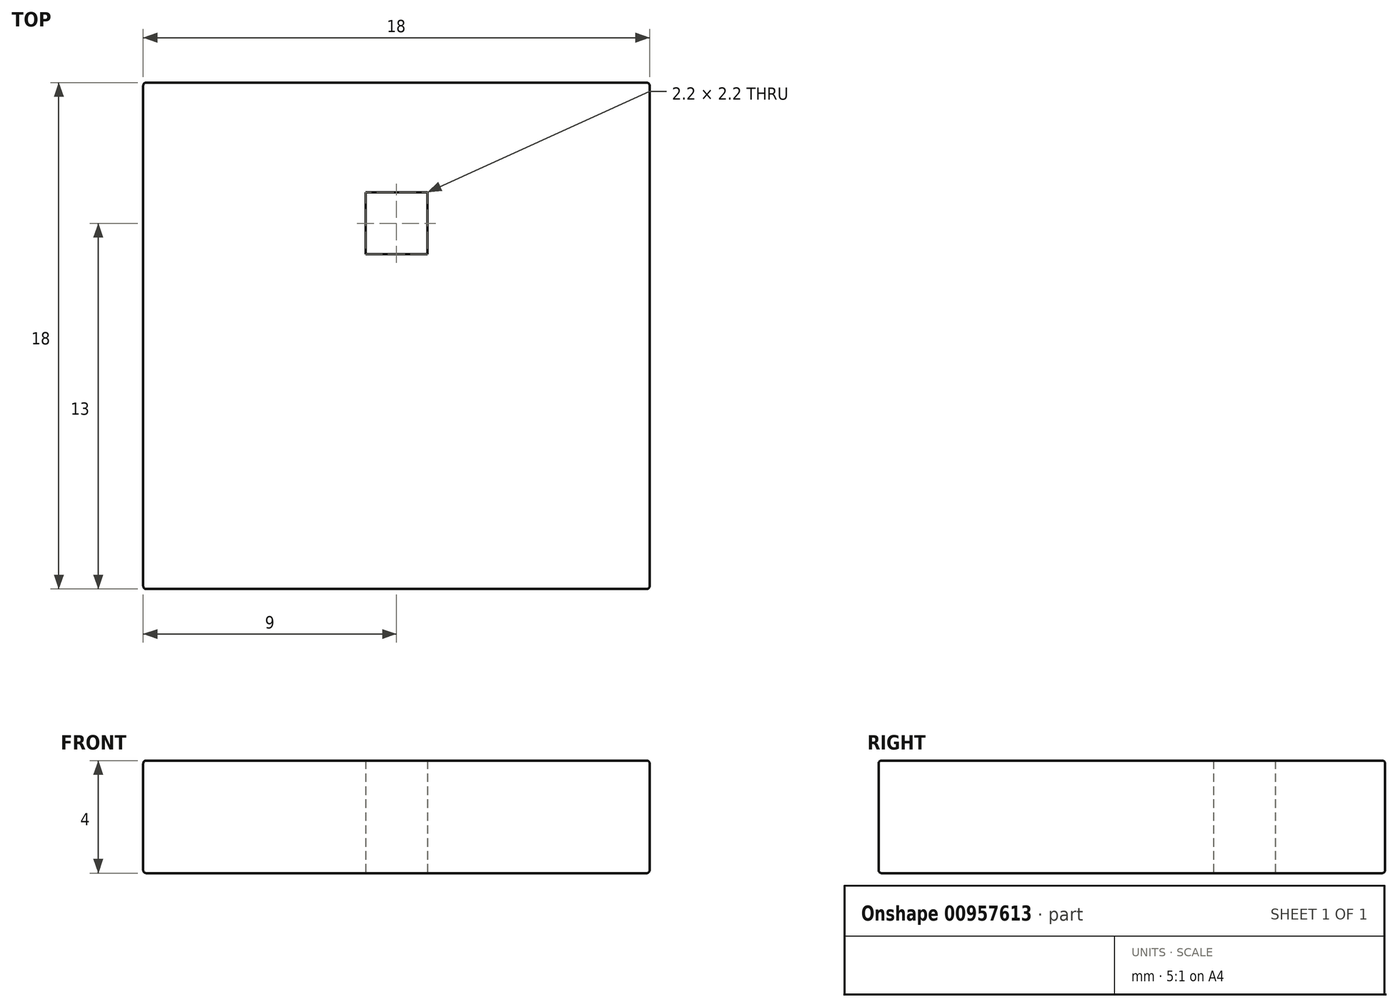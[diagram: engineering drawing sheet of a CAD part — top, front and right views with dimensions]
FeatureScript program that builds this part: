
annotation { "Feature Type Name" : "Feature", "Feature Type Description" : "" }
export const myFeature = defineFeature(function(context is Context, id is Id, definition is map)
    precondition{}
    {
        {
            var Q0;
            Q0=qCreatedBy(makeId("Top.planeOp"),FACE);
            var sketch = newSketch(context, id + "F0", { "sketchPlane" : qUnion([Q0])});
            skLineSegment(sketch, "E0.bottom", {"start": v(-9, 9) * mm, "end": v(9, 9) * mm});
            skLineSegment(sketch, "E0.top", {"start": v(-9, -9) * mm, "end": v(9, -9) * mm});
            skLineSegment(sketch, "E0.left", {"start": v(-9, 9) * mm, "end": v(-9, -9) * mm});
            skLineSegment(sketch, "E0.right", {"start": v(9, 9) * mm, "end": v(9, -9) * mm});
            skPoint(sketch, "E0.middle", {"position": v(0, 0) * mm});
            skLineSegment(sketch, "E1", {"start": v(-8, 9) * mm, "end": v(-8, -9) * mm});
            skLineSegment(sketch, "E2", {"start": v(-7.1, 9) * mm, "end": v(-7.1, -9) * mm});
            skLineSegment(sketch, "E3", {"start": v(-6.9, 9) * mm, "end": v(-6.9, -9) * mm});
            skLineSegment(sketch, "E4", {"start": v(-5.1, 9) * mm, "end": v(-5.1, -9) * mm});
            skLineSegment(sketch, "E5", {"start": v(-4.9, 9) * mm, "end": v(-4.9, -9) * mm});
            skLineSegment(sketch, "E6", {"start": v(-3.1, 9) * mm, "end": v(-3.1, -9) * mm});
            skLineSegment(sketch, "E7", {"start": v(-2.9, 9) * mm, "end": v(-2.9, -9) * mm});
            skLineSegment(sketch, "E8", {"start": v(-1.1, 9) * mm, "end": v(-1.1, -9) * mm});
            skLineSegment(sketch, "E9", {"start": v(-0.9, 9) * mm, "end": v(-0.9, -9) * mm});
            skLineSegment(sketch, "E10", {"start": v(0.9, 9) * mm, "end": v(0.9, -9) * mm});
            skLineSegment(sketch, "E11", {"start": v(1.1, 9) * mm, "end": v(1.1, -9) * mm});
            skLineSegment(sketch, "E12", {"start": v(2.9, 9) * mm, "end": v(2.9, -9) * mm});
            skLineSegment(sketch, "E13", {"start": v(3.1, 9) * mm, "end": v(3.1, -9) * mm});
            skLineSegment(sketch, "E14", {"start": v(4.9, 9) * mm, "end": v(4.9, -9) * mm});
            skLineSegment(sketch, "E15", {"start": v(5.1, 9) * mm, "end": v(5.1, -9) * mm});
            skLineSegment(sketch, "E16", {"start": v(6.9, 9) * mm, "end": v(6.9, -9) * mm});
            skLineSegment(sketch, "E17", {"start": v(7.1, 9) * mm, "end": v(7.1, -9) * mm});
            skLineSegment(sketch, "E18", {"start": v(8, 9) * mm, "end": v(8, -9) * mm});
            skLineSegment(sketch, "E19", {"start": v(9, 8) * mm, "end": v(-9, 8) * mm});
            skLineSegment(sketch, "E20", {"start": v(9, 7.1) * mm, "end": v(-9, 7.1) * mm});
            skLineSegment(sketch, "E21", {"start": v(9, 6.9) * mm, "end": v(-9, 6.9) * mm});
            skLineSegment(sketch, "E22", {"start": v(9, 5.1) * mm, "end": v(-9, 5.1) * mm});
            skLineSegment(sketch, "E23", {"start": v(9, 4.9) * mm, "end": v(-9, 4.9) * mm});
            skLineSegment(sketch, "E24", {"start": v(9, 3.1) * mm, "end": v(-9, 3.1) * mm});
            skLineSegment(sketch, "E25", {"start": v(9, 2.9) * mm, "end": v(-9, 2.9) * mm});
            skLineSegment(sketch, "E26", {"start": v(9, 1.1) * mm, "end": v(-9, 1.1) * mm});
            skLineSegment(sketch, "E27", {"start": v(9, 0.9) * mm, "end": v(-9, 0.9) * mm});
            skLineSegment(sketch, "E28", {"start": v(9, -0.9) * mm, "end": v(-9, -0.9) * mm});
            skLineSegment(sketch, "E29", {"start": v(9, -1.1) * mm, "end": v(-9, -1.1) * mm});
            skLineSegment(sketch, "E30", {"start": v(9, -2.9) * mm, "end": v(-9, -2.9) * mm});
            skLineSegment(sketch, "E31", {"start": v(9, -3.1) * mm, "end": v(-9, -3.1) * mm});
            skLineSegment(sketch, "E32", {"start": v(9, -4.9) * mm, "end": v(-9, -4.9) * mm});
            skLineSegment(sketch, "E33", {"start": v(9, -5.1) * mm, "end": v(-9, -5.1) * mm});
            skLineSegment(sketch, "E34", {"start": v(9, -6.9) * mm, "end": v(-9, -6.9) * mm});
            skLineSegment(sketch, "E35", {"start": v(9, -7.1) * mm, "end": v(-9, -7.1) * mm});
            skLineSegment(sketch, "E36", {"start": v(9, -8) * mm, "end": v(-9, -8) * mm});
            skSolve(sketch);
        }
        {
            var Q0;
            {var subQ0=sQuery(id+"F0.wireOp",EDGE,"E30");var subQ1=sQuery(id+"F0.wireOp",EDGE,"E10");var subQ2=makeQuery(id+"F0.imprint","INTERSECT",VERTEX,{"derivedFrom":[subQ1,subQ0]});Q0=makeQuery(id+"F0.imprint","IMPRINT",FACE,{"disambiguationData":[TD([[makeQuery(id+"F0.imprint","IMPRINT",EDGE,{"disambiguationData":[TD([[subQ2,-1.0]])],"derivedFrom":subQ1}),1.0]])]});}
            var Q1;
            {var subQ0=sQuery(id+"F0.wireOp",EDGE,"E26");var subQ1=sQuery(id+"F0.wireOp",EDGE,"E11");var subQ2=makeQuery(id+"F0.imprint","INTERSECT",VERTEX,{"derivedFrom":[subQ1,subQ0]});Q1=makeQuery(id+"F0.imprint","IMPRINT",FACE,{"disambiguationData":[TD([[makeQuery(id+"F0.imprint","IMPRINT",EDGE,{"disambiguationData":[TD([[subQ2,-1.0]])],"derivedFrom":subQ1}),1.0]])]});}
            var Q2;
            {var subQ0=sQuery(id+"F0.wireOp",EDGE,"E25");var subQ1=sQuery(id+"F0.wireOp",EDGE,"E8");var subQ2=makeQuery(id+"F0.imprint","INTERSECT",VERTEX,{"derivedFrom":[subQ1,subQ0]});Q2=makeQuery(id+"F0.imprint","IMPRINT",FACE,{"disambiguationData":[TD([[makeQuery(id+"F0.imprint","IMPRINT",EDGE,{"disambiguationData":[TD([[subQ2,-1.0]])],"derivedFrom":subQ1}),1.0]])]});}
            var Q3;
            {var subQ0=sQuery(id+"F0.wireOp",EDGE,"E30");var subQ1=sQuery(id+"F0.wireOp",EDGE,"E15");var subQ2=makeQuery(id+"F0.imprint","INTERSECT",VERTEX,{"derivedFrom":[subQ1,subQ0]});Q3=makeQuery(id+"F0.imprint","IMPRINT",FACE,{"disambiguationData":[TD([[makeQuery(id+"F0.imprint","IMPRINT",EDGE,{"disambiguationData":[TD([[subQ2,-1.0]])],"derivedFrom":subQ1}),1.0]])]});}
            var Q4;
            {var subQ0=sQuery(id+"F0.wireOp",EDGE,"E35");var subQ1=sQuery(id+"F0.wireOp",EDGE,"E12");var subQ2=makeQuery(id+"F0.imprint","INTERSECT",VERTEX,{"derivedFrom":[subQ1,subQ0]});Q4=makeQuery(id+"F0.imprint","IMPRINT",FACE,{"disambiguationData":[TD([[makeQuery(id+"F0.imprint","IMPRINT",EDGE,{"disambiguationData":[TD([[subQ2,-1.0]])],"derivedFrom":subQ1}),1.0]])]});}
            var Q5;
            {var subQ0=sQuery(id+"F0.wireOp",EDGE,"E35");var subQ1=sQuery(id+"F0.wireOp",EDGE,"E14");var subQ2=makeQuery(id+"F0.imprint","INTERSECT",VERTEX,{"derivedFrom":[subQ1,subQ0]});Q5=makeQuery(id+"F0.imprint","IMPRINT",FACE,{"disambiguationData":[TD([[makeQuery(id+"F0.imprint","IMPRINT",EDGE,{"disambiguationData":[TD([[subQ2,-1.0]])],"derivedFrom":subQ1}),1.0]])]});}
            var Q6;
            {var subQ0=sQuery(id+"F0.wireOp",EDGE,"E32");var subQ1=sQuery(id+"F0.wireOp",EDGE,"E10");var subQ2=makeQuery(id+"F0.imprint","INTERSECT",VERTEX,{"derivedFrom":[subQ1,subQ0]});Q6=makeQuery(id+"F0.imprint","IMPRINT",FACE,{"disambiguationData":[TD([[makeQuery(id+"F0.imprint","IMPRINT",EDGE,{"disambiguationData":[TD([[subQ2,-1.0]])],"derivedFrom":subQ1}),1.0]])]});}
            var Q7;
            {var subQ0=sQuery(id+"F0.wireOp",EDGE,"E23");var subQ1=sQuery(id+"F0.wireOp",EDGE,"E14");var subQ2=makeQuery(id+"F0.imprint","INTERSECT",VERTEX,{"derivedFrom":[subQ1,subQ0]});Q7=makeQuery(id+"F0.imprint","IMPRINT",FACE,{"disambiguationData":[TD([[makeQuery(id+"F0.imprint","IMPRINT",EDGE,{"disambiguationData":[TD([[subQ2,-1.0]])],"derivedFrom":subQ1}),1.0]])]});}
            var Q8;
            {var subQ0=sQuery(id+"F0.wireOp",EDGE,"E23");var subQ1=sQuery(id+"F0.wireOp",EDGE,"E16");var subQ2=makeQuery(id+"F0.imprint","INTERSECT",VERTEX,{"derivedFrom":[subQ1,subQ0]});Q8=makeQuery(id+"F0.imprint","IMPRINT",FACE,{"disambiguationData":[TD([[makeQuery(id+"F0.imprint","IMPRINT",EDGE,{"disambiguationData":[TD([[subQ2,-1.0]])],"derivedFrom":subQ1}),1.0]])]});}
            var Q9;
            {var subQ0=sQuery(id+"F0.wireOp",EDGE,"E27");var subQ1=sQuery(id+"F0.wireOp",EDGE,"E10");var subQ2=makeQuery(id+"F0.imprint","INTERSECT",VERTEX,{"derivedFrom":[subQ1,subQ0]});Q9=makeQuery(id+"F0.imprint","IMPRINT",FACE,{"disambiguationData":[TD([[makeQuery(id+"F0.imprint","IMPRINT",EDGE,{"disambiguationData":[TD([[subQ2,-1.0]])],"derivedFrom":subQ1}),1.0]])]});}
            var Q10;
            {var subQ0=sQuery(id+"F0.wireOp",EDGE,"E31");var subQ1=sQuery(id+"F0.wireOp",EDGE,"E2");var subQ2=makeQuery(id+"F0.imprint","INTERSECT",VERTEX,{"derivedFrom":[subQ1,subQ0]});Q10=makeQuery(id+"F0.imprint","IMPRINT",FACE,{"disambiguationData":[TD([[makeQuery(id+"F0.imprint","IMPRINT",EDGE,{"disambiguationData":[TD([[subQ2,-1.0]])],"derivedFrom":subQ1}),1.0]])]});}
            var Q11;
            {var subQ0=sQuery(id+"F0.wireOp",EDGE,"E30");var subQ1=sQuery(id+"F0.wireOp",EDGE,"E13");var subQ2=makeQuery(id+"F0.imprint","INTERSECT",VERTEX,{"derivedFrom":[subQ1,subQ0]});Q11=makeQuery(id+"F0.imprint","IMPRINT",FACE,{"disambiguationData":[TD([[makeQuery(id+"F0.imprint","IMPRINT",EDGE,{"disambiguationData":[TD([[subQ2,-1.0]])],"derivedFrom":subQ1}),1.0]])]});}
            var Q12;
            {var subQ0=sQuery(id+"F0.wireOp",EDGE,"E33");var subQ1=sQuery(id+"F0.wireOp",EDGE,"E16");var subQ2=makeQuery(id+"F0.imprint","INTERSECT",VERTEX,{"derivedFrom":[subQ1,subQ0]});Q12=makeQuery(id+"F0.imprint","IMPRINT",FACE,{"disambiguationData":[TD([[makeQuery(id+"F0.imprint","IMPRINT",EDGE,{"disambiguationData":[TD([[subQ2,-1.0]])],"derivedFrom":subQ1}),1.0]])]});}
            var Q13;
            {var subQ0=sQuery(id+"F0.wireOp",EDGE,"E29");var subQ1=sQuery(id+"F0.wireOp",EDGE,"E8");var subQ2=makeQuery(id+"F0.imprint","INTERSECT",VERTEX,{"derivedFrom":[subQ1,subQ0]});Q13=makeQuery(id+"F0.imprint","IMPRINT",FACE,{"disambiguationData":[TD([[makeQuery(id+"F0.imprint","IMPRINT",EDGE,{"disambiguationData":[TD([[subQ2,-1.0]])],"derivedFrom":subQ1}),1.0]])]});}
            var Q14;
            {var subQ0=sQuery(id+"F0.wireOp",EDGE,"E26");var subQ1=sQuery(id+"F0.wireOp",EDGE,"E1");var subQ2=makeQuery(id+"F0.imprint","INTERSECT",VERTEX,{"derivedFrom":[subQ1,subQ0]});Q14=makeQuery(id+"F0.imprint","IMPRINT",FACE,{"disambiguationData":[TD([[makeQuery(id+"F0.imprint","IMPRINT",EDGE,{"disambiguationData":[TD([[subQ2,-1.0]])],"derivedFrom":subQ1}),1.0]])]});}
            var Q15;
            {var subQ0=sQuery(id+"F0.wireOp",EDGE,"E30");var subQ1=sQuery(id+"F0.wireOp",EDGE,"E12");var subQ2=makeQuery(id+"F0.imprint","INTERSECT",VERTEX,{"derivedFrom":[subQ1,subQ0]});Q15=makeQuery(id+"F0.imprint","IMPRINT",FACE,{"disambiguationData":[TD([[makeQuery(id+"F0.imprint","IMPRINT",EDGE,{"disambiguationData":[TD([[subQ2,-1.0]])],"derivedFrom":subQ1}),1.0]])]});}
            var Q16;
            {var subQ0=sQuery(id+"F0.wireOp",EDGE,"E29");var subQ1=sQuery(id+"F0.wireOp",EDGE,"E12");var subQ2=makeQuery(id+"F0.imprint","INTERSECT",VERTEX,{"derivedFrom":[subQ1,subQ0]});Q16=makeQuery(id+"F0.imprint","IMPRINT",FACE,{"disambiguationData":[TD([[makeQuery(id+"F0.imprint","IMPRINT",EDGE,{"disambiguationData":[TD([[subQ2,-1.0]])],"derivedFrom":subQ1}),1.0]])]});}
            var Q17;
            {var subQ0=sQuery(id+"F0.wireOp",EDGE,"E31");var subQ1=sQuery(id+"F0.wireOp",EDGE,"E6");var subQ2=makeQuery(id+"F0.imprint","INTERSECT",VERTEX,{"derivedFrom":[subQ1,subQ0]});Q17=makeQuery(id+"F0.imprint","IMPRINT",FACE,{"disambiguationData":[TD([[makeQuery(id+"F0.imprint","IMPRINT",EDGE,{"disambiguationData":[TD([[subQ2,-1.0]])],"derivedFrom":subQ1}),1.0]])]});}
            var Q18;
            {var subQ0=sQuery(id+"F0.wireOp",EDGE,"E29");var subQ1=sQuery(id+"F0.wireOp",EDGE,"E10");var subQ2=makeQuery(id+"F0.imprint","INTERSECT",VERTEX,{"derivedFrom":[subQ1,subQ0]});Q18=makeQuery(id+"F0.imprint","IMPRINT",FACE,{"disambiguationData":[TD([[makeQuery(id+"F0.imprint","IMPRINT",EDGE,{"disambiguationData":[TD([[subQ2,-1.0]])],"derivedFrom":subQ1}),1.0]])]});}
            var Q19;
            {var subQ0=sQuery(id+"F0.wireOp",EDGE,"E25");var subQ1=sQuery(id+"F0.wireOp",EDGE,"E16");var subQ2=makeQuery(id+"F0.imprint","INTERSECT",VERTEX,{"derivedFrom":[subQ1,subQ0]});Q19=makeQuery(id+"F0.imprint","IMPRINT",FACE,{"disambiguationData":[TD([[makeQuery(id+"F0.imprint","IMPRINT",EDGE,{"disambiguationData":[TD([[subQ2,-1.0]])],"derivedFrom":subQ1}),1.0]])]});}
            var Q20;
            {var subQ0=sQuery(id+"F0.wireOp",EDGE,"E35");var subQ1=sQuery(id+"F0.wireOp",EDGE,"E16");var subQ2=makeQuery(id+"F0.imprint","INTERSECT",VERTEX,{"derivedFrom":[subQ1,subQ0]});Q20=makeQuery(id+"F0.imprint","IMPRINT",FACE,{"disambiguationData":[TD([[makeQuery(id+"F0.imprint","IMPRINT",EDGE,{"disambiguationData":[TD([[subQ2,-1.0]])],"derivedFrom":subQ1}),1.0]])]});}
            var Q21;
            {var subQ0=sQuery(id+"F0.wireOp",EDGE,"E31");var subQ1=sQuery(id+"F0.wireOp",EDGE,"E12");var subQ2=makeQuery(id+"F0.imprint","INTERSECT",VERTEX,{"derivedFrom":[subQ1,subQ0]});Q21=makeQuery(id+"F0.imprint","IMPRINT",FACE,{"disambiguationData":[TD([[makeQuery(id+"F0.imprint","IMPRINT",EDGE,{"disambiguationData":[TD([[subQ2,-1.0]])],"derivedFrom":subQ1}),1.0]])]});}
            var Q22;
            {var subQ0=sQuery(id+"F0.wireOp",EDGE,"E24");var subQ1=sQuery(id+"F0.wireOp",EDGE,"E1");var subQ2=makeQuery(id+"F0.imprint","INTERSECT",VERTEX,{"derivedFrom":[subQ1,subQ0]});Q22=makeQuery(id+"F0.imprint","IMPRINT",FACE,{"disambiguationData":[TD([[makeQuery(id+"F0.imprint","IMPRINT",EDGE,{"disambiguationData":[TD([[subQ2,-1.0]])],"derivedFrom":subQ1}),1.0]])]});}
            var Q23;
            {var subQ0=sQuery(id+"F0.wireOp",EDGE,"E27");var subQ1=sQuery(id+"F0.wireOp",EDGE,"E16");var subQ2=makeQuery(id+"F0.imprint","INTERSECT",VERTEX,{"derivedFrom":[subQ1,subQ0]});Q23=makeQuery(id+"F0.imprint","IMPRINT",FACE,{"disambiguationData":[TD([[makeQuery(id+"F0.imprint","IMPRINT",EDGE,{"disambiguationData":[TD([[subQ2,-1.0]])],"derivedFrom":subQ1}),1.0]])]});}
            var Q24;
            {var subQ0=sQuery(id+"F0.wireOp",EDGE,"E26");var subQ1=sQuery(id+"F0.wireOp",EDGE,"E9");var subQ2=makeQuery(id+"F0.imprint","INTERSECT",VERTEX,{"derivedFrom":[subQ1,subQ0]});Q24=makeQuery(id+"F0.imprint","IMPRINT",FACE,{"disambiguationData":[TD([[makeQuery(id+"F0.imprint","IMPRINT",EDGE,{"disambiguationData":[TD([[subQ2,-1.0]])],"derivedFrom":subQ1}),1.0]])]});}
            var Q25;
            {var subQ0=sQuery(id+"F0.wireOp",EDGE,"E35");var subQ1=sQuery(id+"F0.wireOp",EDGE,"E2");var subQ2=makeQuery(id+"F0.imprint","INTERSECT",VERTEX,{"derivedFrom":[subQ1,subQ0]});Q25=makeQuery(id+"F0.imprint","IMPRINT",FACE,{"disambiguationData":[TD([[makeQuery(id+"F0.imprint","IMPRINT",EDGE,{"disambiguationData":[TD([[subQ2,-1.0]])],"derivedFrom":subQ1}),1.0]])]});}
            var Q26;
            {var subQ0=sQuery(id+"F0.wireOp",EDGE,"E22");var subQ1=sQuery(id+"F0.wireOp",EDGE,"E16");var subQ2=makeQuery(id+"F0.imprint","INTERSECT",VERTEX,{"derivedFrom":[subQ1,subQ0]});Q26=makeQuery(id+"F0.imprint","IMPRINT",FACE,{"disambiguationData":[TD([[makeQuery(id+"F0.imprint","IMPRINT",EDGE,{"disambiguationData":[TD([[subQ2,-1.0]])],"derivedFrom":subQ1}),1.0]])]});}
            var Q27;
            {var subQ0=sQuery(id+"F0.wireOp",EDGE,"E35");var subQ1=sQuery(id+"F0.wireOp",EDGE,"E8");var subQ2=makeQuery(id+"F0.imprint","INTERSECT",VERTEX,{"derivedFrom":[subQ1,subQ0]});Q27=makeQuery(id+"F0.imprint","IMPRINT",FACE,{"disambiguationData":[TD([[makeQuery(id+"F0.imprint","IMPRINT",EDGE,{"disambiguationData":[TD([[subQ2,-1.0]])],"derivedFrom":subQ1}),1.0]])]});}
            var Q28;
            {var subQ0=sQuery(id+"F0.wireOp",EDGE,"E24");var subQ1=sQuery(id+"F0.wireOp",EDGE,"E7");var subQ2=makeQuery(id+"F0.imprint","INTERSECT",VERTEX,{"derivedFrom":[subQ1,subQ0]});Q28=makeQuery(id+"F0.imprint","IMPRINT",FACE,{"disambiguationData":[TD([[makeQuery(id+"F0.imprint","IMPRINT",EDGE,{"disambiguationData":[TD([[subQ2,-1.0]])],"derivedFrom":subQ1}),1.0]])]});}
            var Q29;
            {var subQ0=sQuery(id+"F0.wireOp",EDGE,"E21");var subQ1=sQuery(id+"F0.wireOp",EDGE,"E16");var subQ2=makeQuery(id+"F0.imprint","INTERSECT",VERTEX,{"derivedFrom":[subQ1,subQ0]});Q29=makeQuery(id+"F0.imprint","IMPRINT",FACE,{"disambiguationData":[TD([[makeQuery(id+"F0.imprint","IMPRINT",EDGE,{"disambiguationData":[TD([[subQ2,-1.0]])],"derivedFrom":subQ1}),1.0]])]});}
            var Q30;
            {var subQ0=sQuery(id+"F0.wireOp",EDGE,"E32");var subQ1=sQuery(id+"F0.wireOp",EDGE,"E11");var subQ2=makeQuery(id+"F0.imprint","INTERSECT",VERTEX,{"derivedFrom":[subQ1,subQ0]});Q30=makeQuery(id+"F0.imprint","IMPRINT",FACE,{"disambiguationData":[TD([[makeQuery(id+"F0.imprint","IMPRINT",EDGE,{"disambiguationData":[TD([[subQ2,-1.0]])],"derivedFrom":subQ1}),1.0]])]});}
            var Q31;
            {var subQ0=sQuery(id+"F0.wireOp",EDGE,"E33");var subQ1=sQuery(id+"F0.wireOp",EDGE,"E8");var subQ2=makeQuery(id+"F0.imprint","INTERSECT",VERTEX,{"derivedFrom":[subQ1,subQ0]});Q31=makeQuery(id+"F0.imprint","IMPRINT",FACE,{"disambiguationData":[TD([[makeQuery(id+"F0.imprint","IMPRINT",EDGE,{"disambiguationData":[TD([[subQ2,-1.0]])],"derivedFrom":subQ1}),1.0]])]});}
            var Q32;
            {var subQ0=sQuery(id+"F0.wireOp",EDGE,"E30");var subQ1=sQuery(id+"F0.wireOp",EDGE,"E9");var subQ2=makeQuery(id+"F0.imprint","INTERSECT",VERTEX,{"derivedFrom":[subQ1,subQ0]});Q32=makeQuery(id+"F0.imprint","IMPRINT",FACE,{"disambiguationData":[TD([[makeQuery(id+"F0.imprint","IMPRINT",EDGE,{"disambiguationData":[TD([[subQ2,-1.0]])],"derivedFrom":subQ1}),1.0]])]});}
            var Q33;
            {var subQ0=sQuery(id+"F0.wireOp",EDGE,"E27");var subQ1=sQuery(id+"F0.wireOp",EDGE,"E2");var subQ2=makeQuery(id+"F0.imprint","INTERSECT",VERTEX,{"derivedFrom":[subQ1,subQ0]});Q33=makeQuery(id+"F0.imprint","IMPRINT",FACE,{"disambiguationData":[TD([[makeQuery(id+"F0.imprint","IMPRINT",EDGE,{"disambiguationData":[TD([[subQ2,-1.0]])],"derivedFrom":subQ1}),1.0]])]});}
            var Q34;
            {var subQ0=sQuery(id+"F0.wireOp",EDGE,"E30");var subQ1=sQuery(id+"F0.wireOp",EDGE,"E11");var subQ2=makeQuery(id+"F0.imprint","INTERSECT",VERTEX,{"derivedFrom":[subQ1,subQ0]});Q34=makeQuery(id+"F0.imprint","IMPRINT",FACE,{"disambiguationData":[TD([[makeQuery(id+"F0.imprint","IMPRINT",EDGE,{"disambiguationData":[TD([[subQ2,-1.0]])],"derivedFrom":subQ1}),1.0]])]});}
            var Q35;
            {var subQ0=sQuery(id+"F0.wireOp",EDGE,"E26");var subQ1=sQuery(id+"F0.wireOp",EDGE,"E5");var subQ2=makeQuery(id+"F0.imprint","INTERSECT",VERTEX,{"derivedFrom":[subQ1,subQ0]});Q35=makeQuery(id+"F0.imprint","IMPRINT",FACE,{"disambiguationData":[TD([[makeQuery(id+"F0.imprint","IMPRINT",EDGE,{"disambiguationData":[TD([[subQ2,-1.0]])],"derivedFrom":subQ1}),1.0]])]});}
            var Q36;
            {var subQ0=sQuery(id+"F0.wireOp",EDGE,"E31");var subQ1=sQuery(id+"F0.wireOp",EDGE,"E8");var subQ2=makeQuery(id+"F0.imprint","INTERSECT",VERTEX,{"derivedFrom":[subQ1,subQ0]});Q36=makeQuery(id+"F0.imprint","IMPRINT",FACE,{"disambiguationData":[TD([[makeQuery(id+"F0.imprint","IMPRINT",EDGE,{"disambiguationData":[TD([[subQ2,-1.0]])],"derivedFrom":subQ1}),1.0]])]});}
            var Q37;
            {var subQ0=sQuery(id+"F0.wireOp",EDGE,"E32");var subQ1=sQuery(id+"F0.wireOp",EDGE,"E7");var subQ2=makeQuery(id+"F0.imprint","INTERSECT",VERTEX,{"derivedFrom":[subQ1,subQ0]});Q37=makeQuery(id+"F0.imprint","IMPRINT",FACE,{"disambiguationData":[TD([[makeQuery(id+"F0.imprint","IMPRINT",EDGE,{"disambiguationData":[TD([[subQ2,-1.0]])],"derivedFrom":subQ1}),1.0]])]});}
            var Q38;
            {var subQ0=sQuery(id+"F0.wireOp",EDGE,"E24");var subQ1=sQuery(id+"F0.wireOp",EDGE,"E17");var subQ2=makeQuery(id+"F0.imprint","INTERSECT",VERTEX,{"derivedFrom":[subQ1,subQ0]});Q38=makeQuery(id+"F0.imprint","IMPRINT",FACE,{"disambiguationData":[TD([[makeQuery(id+"F0.imprint","IMPRINT",EDGE,{"disambiguationData":[TD([[subQ2,-1.0]])],"derivedFrom":subQ1}),1.0]])]});}
            var Q39;
            {var subQ0=sQuery(id+"F0.wireOp",EDGE,"E26");var subQ1=sQuery(id+"F0.wireOp",EDGE,"E14");var subQ2=makeQuery(id+"F0.imprint","INTERSECT",VERTEX,{"derivedFrom":[subQ1,subQ0]});Q39=makeQuery(id+"F0.imprint","IMPRINT",FACE,{"disambiguationData":[TD([[makeQuery(id+"F0.imprint","IMPRINT",EDGE,{"disambiguationData":[TD([[subQ2,-1.0]])],"derivedFrom":subQ1}),1.0]])]});}
            var Q40;
            {var subQ0=sQuery(id+"F0.wireOp",EDGE,"E31");var subQ1=sQuery(id+"F0.wireOp",EDGE,"E14");var subQ2=makeQuery(id+"F0.imprint","INTERSECT",VERTEX,{"derivedFrom":[subQ1,subQ0]});Q40=makeQuery(id+"F0.imprint","IMPRINT",FACE,{"disambiguationData":[TD([[makeQuery(id+"F0.imprint","IMPRINT",EDGE,{"disambiguationData":[TD([[subQ2,-1.0]])],"derivedFrom":subQ1}),1.0]])]});}
            var Q41;
            {var subQ0=sQuery(id+"F0.wireOp",EDGE,"E24");var subQ1=sQuery(id+"F0.wireOp",EDGE,"E5");var subQ2=makeQuery(id+"F0.imprint","INTERSECT",VERTEX,{"derivedFrom":[subQ1,subQ0]});Q41=makeQuery(id+"F0.imprint","IMPRINT",FACE,{"disambiguationData":[TD([[makeQuery(id+"F0.imprint","IMPRINT",EDGE,{"disambiguationData":[TD([[subQ2,-1.0]])],"derivedFrom":subQ1}),1.0]])]});}
            var Q42;
            {var subQ0=sQuery(id+"F0.wireOp",EDGE,"E26");var subQ1=sQuery(id+"F0.wireOp",EDGE,"E12");var subQ2=makeQuery(id+"F0.imprint","INTERSECT",VERTEX,{"derivedFrom":[subQ1,subQ0]});Q42=makeQuery(id+"F0.imprint","IMPRINT",FACE,{"disambiguationData":[TD([[makeQuery(id+"F0.imprint","IMPRINT",EDGE,{"disambiguationData":[TD([[subQ2,-1.0]])],"derivedFrom":subQ1}),1.0]])]});}
            var Q43;
            {var subQ0=sQuery(id+"F0.wireOp",EDGE,"E30");var subQ1=sQuery(id+"F0.wireOp",EDGE,"E5");var subQ2=makeQuery(id+"F0.imprint","INTERSECT",VERTEX,{"derivedFrom":[subQ1,subQ0]});Q43=makeQuery(id+"F0.imprint","IMPRINT",FACE,{"disambiguationData":[TD([[makeQuery(id+"F0.imprint","IMPRINT",EDGE,{"disambiguationData":[TD([[subQ2,-1.0]])],"derivedFrom":subQ1}),1.0]])]});}
            var Q44;
            {var subQ0=sQuery(id+"F0.wireOp",EDGE,"E33");var subQ1=sQuery(id+"F0.wireOp",EDGE,"E14");var subQ2=makeQuery(id+"F0.imprint","INTERSECT",VERTEX,{"derivedFrom":[subQ1,subQ0]});Q44=makeQuery(id+"F0.imprint","IMPRINT",FACE,{"disambiguationData":[TD([[makeQuery(id+"F0.imprint","IMPRINT",EDGE,{"disambiguationData":[TD([[subQ2,-1.0]])],"derivedFrom":subQ1}),1.0]])]});}
            var Q45;
            {var subQ0=sQuery(id+"F0.wireOp",EDGE,"E32");var subQ1=sQuery(id+"F0.wireOp",EDGE,"E9");var subQ2=makeQuery(id+"F0.imprint","INTERSECT",VERTEX,{"derivedFrom":[subQ1,subQ0]});Q45=makeQuery(id+"F0.imprint","IMPRINT",FACE,{"disambiguationData":[TD([[makeQuery(id+"F0.imprint","IMPRINT",EDGE,{"disambiguationData":[TD([[subQ2,-1.0]])],"derivedFrom":subQ1}),1.0]])]});}
            var Q46;
            {var subQ0=sQuery(id+"F0.wireOp",EDGE,"E25");var subQ1=sQuery(id+"F0.wireOp",EDGE,"E6");var subQ2=makeQuery(id+"F0.imprint","INTERSECT",VERTEX,{"derivedFrom":[subQ1,subQ0]});Q46=makeQuery(id+"F0.imprint","IMPRINT",FACE,{"disambiguationData":[TD([[makeQuery(id+"F0.imprint","IMPRINT",EDGE,{"disambiguationData":[TD([[subQ2,-1.0]])],"derivedFrom":subQ1}),1.0]])]});}
            var Q47;
            {var subQ0=sQuery(id+"F0.wireOp",EDGE,"E19");var subQ1=sQuery(id+"F0.wireOp",EDGE,"E16");var subQ2=makeQuery(id+"F0.imprint","INTERSECT",VERTEX,{"derivedFrom":[subQ1,subQ0]});Q47=makeQuery(id+"F0.imprint","IMPRINT",FACE,{"disambiguationData":[TD([[makeQuery(id+"F0.imprint","IMPRINT",EDGE,{"disambiguationData":[TD([[subQ2,-1.0]])],"derivedFrom":subQ1}),1.0]])]});}
            var Q48;
            {var subQ0=sQuery(id+"F0.wireOp",EDGE,"E19");var subQ1=sQuery(id+"F0.wireOp",EDGE,"E10");var subQ2=makeQuery(id+"F0.imprint","INTERSECT",VERTEX,{"derivedFrom":[subQ1,subQ0]});Q48=makeQuery(id+"F0.imprint","IMPRINT",FACE,{"disambiguationData":[TD([[makeQuery(id+"F0.imprint","IMPRINT",EDGE,{"disambiguationData":[TD([[subQ2,-1.0]])],"derivedFrom":subQ1}),1.0]])]});}
            var Q49;
            {var subQ0=sQuery(id+"F0.wireOp",EDGE,"E19");var subQ1=sQuery(id+"F0.wireOp",EDGE,"E2");var subQ2=makeQuery(id+"F0.imprint","INTERSECT",VERTEX,{"derivedFrom":[subQ1,subQ0]});Q49=makeQuery(id+"F0.imprint","IMPRINT",FACE,{"disambiguationData":[TD([[makeQuery(id+"F0.imprint","IMPRINT",EDGE,{"disambiguationData":[TD([[subQ2,-1.0]])],"derivedFrom":subQ1}),1.0]])]});}
            var Q50;
            {var subQ0=sQuery(id+"F0.wireOp",EDGE,"E32");var subQ1=sQuery(id+"F0.wireOp",EDGE,"E17");var subQ2=makeQuery(id+"F0.imprint","INTERSECT",VERTEX,{"derivedFrom":[subQ1,subQ0]});Q50=makeQuery(id+"F0.imprint","IMPRINT",FACE,{"disambiguationData":[TD([[makeQuery(id+"F0.imprint","IMPRINT",EDGE,{"disambiguationData":[TD([[subQ2,-1.0]])],"derivedFrom":subQ1}),1.0]])]});}
            var Q51;
            {var subQ0=sQuery(id+"F0.wireOp",EDGE,"E30");var subQ1=sQuery(id+"F0.wireOp",EDGE,"E17");var subQ2=makeQuery(id+"F0.imprint","INTERSECT",VERTEX,{"derivedFrom":[subQ1,subQ0]});Q51=makeQuery(id+"F0.imprint","IMPRINT",FACE,{"disambiguationData":[TD([[makeQuery(id+"F0.imprint","IMPRINT",EDGE,{"disambiguationData":[TD([[subQ2,-1.0]])],"derivedFrom":subQ1}),1.0]])]});}
            var Q52;
            {var subQ0=sQuery(id+"F0.wireOp",EDGE,"E33");var subQ1=sQuery(id+"F0.wireOp",EDGE,"E12");var subQ2=makeQuery(id+"F0.imprint","INTERSECT",VERTEX,{"derivedFrom":[subQ1,subQ0]});Q52=makeQuery(id+"F0.imprint","IMPRINT",FACE,{"disambiguationData":[TD([[makeQuery(id+"F0.imprint","IMPRINT",EDGE,{"disambiguationData":[TD([[subQ2,-1.0]])],"derivedFrom":subQ1}),1.0]])]});}
            var Q53;
            {var subQ0=sQuery(id+"F0.wireOp",EDGE,"E22");var subQ1=sQuery(id+"F0.wireOp",EDGE,"E13");var subQ2=makeQuery(id+"F0.imprint","INTERSECT",VERTEX,{"derivedFrom":[subQ1,subQ0]});Q53=makeQuery(id+"F0.imprint","IMPRINT",FACE,{"disambiguationData":[TD([[makeQuery(id+"F0.imprint","IMPRINT",EDGE,{"disambiguationData":[TD([[subQ2,-1.0]])],"derivedFrom":subQ1}),1.0]])]});}
            var Q54;
            {var subQ0=sQuery(id+"F0.wireOp",EDGE,"E19");var subQ1=sQuery(id+"F0.wireOp",EDGE,"E14");var subQ2=makeQuery(id+"F0.imprint","INTERSECT",VERTEX,{"derivedFrom":[subQ1,subQ0]});Q54=makeQuery(id+"F0.imprint","IMPRINT",FACE,{"disambiguationData":[TD([[makeQuery(id+"F0.imprint","IMPRINT",EDGE,{"disambiguationData":[TD([[subQ2,-1.0]])],"derivedFrom":subQ1}),1.0]])]});}
            var Q55;
            {var subQ0=sQuery(id+"F0.wireOp",EDGE,"E32");var subQ1=sQuery(id+"F0.wireOp",EDGE,"E16");var subQ2=makeQuery(id+"F0.imprint","INTERSECT",VERTEX,{"derivedFrom":[subQ1,subQ0]});Q55=makeQuery(id+"F0.imprint","IMPRINT",FACE,{"disambiguationData":[TD([[makeQuery(id+"F0.imprint","IMPRINT",EDGE,{"disambiguationData":[TD([[subQ2,-1.0]])],"derivedFrom":subQ1}),1.0]])]});}
            var Q56;
            {var subQ0=sQuery(id+"F0.wireOp",EDGE,"E32");var subQ1=sQuery(id+"F0.wireOp",EDGE,"E3");var subQ2=makeQuery(id+"F0.imprint","INTERSECT",VERTEX,{"derivedFrom":[subQ1,subQ0]});Q56=makeQuery(id+"F0.imprint","IMPRINT",FACE,{"disambiguationData":[TD([[makeQuery(id+"F0.imprint","IMPRINT",EDGE,{"disambiguationData":[TD([[subQ2,-1.0]])],"derivedFrom":subQ1}),1.0]])]});}
            var Q57;
            {var subQ0=sQuery(id+"F0.wireOp",EDGE,"E32");var subQ1=sQuery(id+"F0.wireOp",EDGE,"E6");var subQ2=makeQuery(id+"F0.imprint","INTERSECT",VERTEX,{"derivedFrom":[subQ1,subQ0]});Q57=makeQuery(id+"F0.imprint","IMPRINT",FACE,{"disambiguationData":[TD([[makeQuery(id+"F0.imprint","IMPRINT",EDGE,{"disambiguationData":[TD([[subQ2,-1.0]])],"derivedFrom":subQ1}),1.0]])]});}
            var Q58;
            {var subQ0=sQuery(id+"F0.wireOp",EDGE,"E35");var subQ1=sQuery(id+"F0.wireOp",EDGE,"E10");var subQ2=makeQuery(id+"F0.imprint","INTERSECT",VERTEX,{"derivedFrom":[subQ1,subQ0]});Q58=makeQuery(id+"F0.imprint","IMPRINT",FACE,{"disambiguationData":[TD([[makeQuery(id+"F0.imprint","IMPRINT",EDGE,{"disambiguationData":[TD([[subQ2,-1.0]])],"derivedFrom":subQ1}),1.0]])]});}
            var Q59;
            {var subQ0=sQuery(id+"F0.wireOp",EDGE,"E23");var subQ1=sQuery(id+"F0.wireOp",EDGE,"E12");var subQ2=makeQuery(id+"F0.imprint","INTERSECT",VERTEX,{"derivedFrom":[subQ1,subQ0]});Q59=makeQuery(id+"F0.imprint","IMPRINT",FACE,{"disambiguationData":[TD([[makeQuery(id+"F0.imprint","IMPRINT",EDGE,{"disambiguationData":[TD([[subQ2,-1.0]])],"derivedFrom":subQ1}),1.0]])]});}
            var Q60;
            {var subQ0=sQuery(id+"F0.wireOp",EDGE,"E32");var subQ1=sQuery(id+"F0.wireOp",EDGE,"E5");var subQ2=makeQuery(id+"F0.imprint","INTERSECT",VERTEX,{"derivedFrom":[subQ1,subQ0]});Q60=makeQuery(id+"F0.imprint","IMPRINT",FACE,{"disambiguationData":[TD([[makeQuery(id+"F0.imprint","IMPRINT",EDGE,{"disambiguationData":[TD([[subQ2,-1.0]])],"derivedFrom":subQ1}),1.0]])]});}
            var Q61;
            {var subQ0=sQuery(id+"F0.wireOp",EDGE,"E33");var subQ1=sQuery(id+"F0.wireOp",EDGE,"E6");var subQ2=makeQuery(id+"F0.imprint","INTERSECT",VERTEX,{"derivedFrom":[subQ1,subQ0]});Q61=makeQuery(id+"F0.imprint","IMPRINT",FACE,{"disambiguationData":[TD([[makeQuery(id+"F0.imprint","IMPRINT",EDGE,{"disambiguationData":[TD([[subQ2,-1.0]])],"derivedFrom":subQ1}),1.0]])]});}
            var Q62;
            {var subQ0=sQuery(id+"F0.wireOp",EDGE,"E30");var subQ1=sQuery(id+"F0.wireOp",EDGE,"E7");var subQ2=makeQuery(id+"F0.imprint","INTERSECT",VERTEX,{"derivedFrom":[subQ1,subQ0]});Q62=makeQuery(id+"F0.imprint","IMPRINT",FACE,{"disambiguationData":[TD([[makeQuery(id+"F0.imprint","IMPRINT",EDGE,{"disambiguationData":[TD([[subQ2,-1.0]])],"derivedFrom":subQ1}),1.0]])]});}
            var Q63;
            {var subQ0=sQuery(id+"F0.wireOp",EDGE,"E33");var subQ1=sQuery(id+"F0.wireOp",EDGE,"E10");var subQ2=makeQuery(id+"F0.imprint","INTERSECT",VERTEX,{"derivedFrom":[subQ1,subQ0]});Q63=makeQuery(id+"F0.imprint","IMPRINT",FACE,{"disambiguationData":[TD([[makeQuery(id+"F0.imprint","IMPRINT",EDGE,{"disambiguationData":[TD([[subQ2,-1.0]])],"derivedFrom":subQ1}),1.0]])]});}
            var Q64;
            {var subQ0=sQuery(id+"F0.wireOp",EDGE,"E30");var subQ1=sQuery(id+"F0.wireOp",EDGE,"E14");var subQ2=makeQuery(id+"F0.imprint","INTERSECT",VERTEX,{"derivedFrom":[subQ1,subQ0]});Q64=makeQuery(id+"F0.imprint","IMPRINT",FACE,{"disambiguationData":[TD([[makeQuery(id+"F0.imprint","IMPRINT",EDGE,{"disambiguationData":[TD([[subQ2,-1.0]])],"derivedFrom":subQ1}),1.0]])]});}
            var Q65;
            {var subQ0=sQuery(id+"F0.wireOp",EDGE,"E26");var subQ1=sQuery(id+"F0.wireOp",EDGE,"E13");var subQ2=makeQuery(id+"F0.imprint","INTERSECT",VERTEX,{"derivedFrom":[subQ1,subQ0]});Q65=makeQuery(id+"F0.imprint","IMPRINT",FACE,{"disambiguationData":[TD([[makeQuery(id+"F0.imprint","IMPRINT",EDGE,{"disambiguationData":[TD([[subQ2,-1.0]])],"derivedFrom":subQ1}),1.0]])]});}
            var Q66;
            {var subQ0=sQuery(id+"F0.wireOp",EDGE,"E26");var subQ1=sQuery(id+"F0.wireOp",EDGE,"E16");var subQ2=makeQuery(id+"F0.imprint","INTERSECT",VERTEX,{"derivedFrom":[subQ1,subQ0]});Q66=makeQuery(id+"F0.imprint","IMPRINT",FACE,{"disambiguationData":[TD([[makeQuery(id+"F0.imprint","IMPRINT",EDGE,{"disambiguationData":[TD([[subQ2,-1.0]])],"derivedFrom":subQ1}),1.0]])]});}
            var Q67;
            {var subQ0=sQuery(id+"F0.wireOp",EDGE,"E32");var subQ1=sQuery(id+"F0.wireOp",EDGE,"E14");var subQ2=makeQuery(id+"F0.imprint","INTERSECT",VERTEX,{"derivedFrom":[subQ1,subQ0]});Q67=makeQuery(id+"F0.imprint","IMPRINT",FACE,{"disambiguationData":[TD([[makeQuery(id+"F0.imprint","IMPRINT",EDGE,{"disambiguationData":[TD([[subQ2,-1.0]])],"derivedFrom":subQ1}),1.0]])]});}
            var Q68;
            {var subQ0=sQuery(id+"F0.wireOp",EDGE,"E24");var subQ1=sQuery(id+"F0.wireOp",EDGE,"E11");var subQ2=makeQuery(id+"F0.imprint","INTERSECT",VERTEX,{"derivedFrom":[subQ1,subQ0]});Q68=makeQuery(id+"F0.imprint","IMPRINT",FACE,{"disambiguationData":[TD([[makeQuery(id+"F0.imprint","IMPRINT",EDGE,{"disambiguationData":[TD([[subQ2,-1.0]])],"derivedFrom":subQ1}),1.0]])]});}
            var Q69;
            {var subQ0=sQuery(id+"F0.wireOp",EDGE,"E30");var subQ1=sQuery(id+"F0.wireOp",EDGE,"E3");var subQ2=makeQuery(id+"F0.imprint","INTERSECT",VERTEX,{"derivedFrom":[subQ1,subQ0]});Q69=makeQuery(id+"F0.imprint","IMPRINT",FACE,{"disambiguationData":[TD([[makeQuery(id+"F0.imprint","IMPRINT",EDGE,{"disambiguationData":[TD([[subQ2,-1.0]])],"derivedFrom":subQ1}),1.0]])]});}
            var Q70;
            {var subQ0=sQuery(id+"F0.wireOp",EDGE,"E22");var subQ1=sQuery(id+"F0.wireOp",EDGE,"E14");var subQ2=makeQuery(id+"F0.imprint","INTERSECT",VERTEX,{"derivedFrom":[subQ1,subQ0]});Q70=makeQuery(id+"F0.imprint","IMPRINT",FACE,{"disambiguationData":[TD([[makeQuery(id+"F0.imprint","IMPRINT",EDGE,{"disambiguationData":[TD([[subQ2,-1.0]])],"derivedFrom":subQ1}),1.0]])]});}
            var Q71;
            {var subQ0=sQuery(id+"F0.wireOp",EDGE,"E22");var subQ1=sQuery(id+"F0.wireOp",EDGE,"E15");var subQ2=makeQuery(id+"F0.imprint","INTERSECT",VERTEX,{"derivedFrom":[subQ1,subQ0]});Q71=makeQuery(id+"F0.imprint","IMPRINT",FACE,{"disambiguationData":[TD([[makeQuery(id+"F0.imprint","IMPRINT",EDGE,{"disambiguationData":[TD([[subQ2,-1.0]])],"derivedFrom":subQ1}),1.0]])]});}
            var Q72;
            {var subQ0=sQuery(id+"F0.wireOp",EDGE,"E29");var subQ1=sQuery(id+"F0.wireOp",EDGE,"E16");var subQ2=makeQuery(id+"F0.imprint","INTERSECT",VERTEX,{"derivedFrom":[subQ1,subQ0]});Q72=makeQuery(id+"F0.imprint","IMPRINT",FACE,{"disambiguationData":[TD([[makeQuery(id+"F0.imprint","IMPRINT",EDGE,{"disambiguationData":[TD([[subQ2,-1.0]])],"derivedFrom":subQ1}),1.0]])]});}
            var Q73;
            {var subQ0=sQuery(id+"F0.wireOp",EDGE,"E22");var subQ1=sQuery(id+"F0.wireOp",EDGE,"E17");var subQ2=makeQuery(id+"F0.imprint","INTERSECT",VERTEX,{"derivedFrom":[subQ1,subQ0]});Q73=makeQuery(id+"F0.imprint","IMPRINT",FACE,{"disambiguationData":[TD([[makeQuery(id+"F0.imprint","IMPRINT",EDGE,{"disambiguationData":[TD([[subQ2,-1.0]])],"derivedFrom":subQ1}),1.0]])]});}
            var Q74;
            {var subQ0=sQuery(id+"F0.wireOp",EDGE,"E30");var subQ1=sQuery(id+"F0.wireOp",EDGE,"E6");var subQ2=makeQuery(id+"F0.imprint","INTERSECT",VERTEX,{"derivedFrom":[subQ1,subQ0]});Q74=makeQuery(id+"F0.imprint","IMPRINT",FACE,{"disambiguationData":[TD([[makeQuery(id+"F0.imprint","IMPRINT",EDGE,{"disambiguationData":[TD([[subQ2,-1.0]])],"derivedFrom":subQ1}),1.0]])]});}
            var Q75;
            {var subQ0=sQuery(id+"F0.wireOp",EDGE,"E21");var subQ1=sQuery(id+"F0.wireOp",EDGE,"E10");var subQ2=makeQuery(id+"F0.imprint","INTERSECT",VERTEX,{"derivedFrom":[subQ1,subQ0]});Q75=makeQuery(id+"F0.imprint","IMPRINT",FACE,{"disambiguationData":[TD([[makeQuery(id+"F0.imprint","IMPRINT",EDGE,{"disambiguationData":[TD([[subQ2,-1.0]])],"derivedFrom":subQ1}),1.0]])]});}
            var Q76;
            {var subQ0=sQuery(id+"F0.wireOp",EDGE,"E24");var subQ1=sQuery(id+"F0.wireOp",EDGE,"E6");var subQ2=makeQuery(id+"F0.imprint","INTERSECT",VERTEX,{"derivedFrom":[subQ1,subQ0]});Q76=makeQuery(id+"F0.imprint","IMPRINT",FACE,{"disambiguationData":[TD([[makeQuery(id+"F0.imprint","IMPRINT",EDGE,{"disambiguationData":[TD([[subQ2,-1.0]])],"derivedFrom":subQ1}),1.0]])]});}
            var Q77;
            {var subQ0=sQuery(id+"F0.wireOp",EDGE,"E32");var subQ1=sQuery(id+"F0.wireOp",EDGE,"E1");var subQ2=makeQuery(id+"F0.imprint","INTERSECT",VERTEX,{"derivedFrom":[subQ1,subQ0]});Q77=makeQuery(id+"F0.imprint","IMPRINT",FACE,{"disambiguationData":[TD([[makeQuery(id+"F0.imprint","IMPRINT",EDGE,{"disambiguationData":[TD([[subQ2,-1.0]])],"derivedFrom":subQ1}),1.0]])]});}
            var Q78;
            {var subQ0=sQuery(id+"F0.wireOp",EDGE,"E24");var subQ1=sQuery(id+"F0.wireOp",EDGE,"E12");var subQ2=makeQuery(id+"F0.imprint","INTERSECT",VERTEX,{"derivedFrom":[subQ1,subQ0]});Q78=makeQuery(id+"F0.imprint","IMPRINT",FACE,{"disambiguationData":[TD([[makeQuery(id+"F0.imprint","IMPRINT",EDGE,{"disambiguationData":[TD([[subQ2,-1.0]])],"derivedFrom":subQ1}),1.0]])]});}
            var Q79;
            {var subQ0=sQuery(id+"F0.wireOp",EDGE,"E25");var subQ1=sQuery(id+"F0.wireOp",EDGE,"E14");var subQ2=makeQuery(id+"F0.imprint","INTERSECT",VERTEX,{"derivedFrom":[subQ1,subQ0]});Q79=makeQuery(id+"F0.imprint","IMPRINT",FACE,{"disambiguationData":[TD([[makeQuery(id+"F0.imprint","IMPRINT",EDGE,{"disambiguationData":[TD([[subQ2,-1.0]])],"derivedFrom":subQ1}),1.0]])]});}
            var Q80;
            {var subQ0=sQuery(id+"F0.wireOp",EDGE,"E26");var subQ1=sQuery(id+"F0.wireOp",EDGE,"E6");var subQ2=makeQuery(id+"F0.imprint","INTERSECT",VERTEX,{"derivedFrom":[subQ1,subQ0]});Q80=makeQuery(id+"F0.imprint","IMPRINT",FACE,{"disambiguationData":[TD([[makeQuery(id+"F0.imprint","IMPRINT",EDGE,{"disambiguationData":[TD([[subQ2,-1.0]])],"derivedFrom":subQ1}),1.0]])]});}
            var Q81;
            {var subQ0=sQuery(id+"F0.wireOp",EDGE,"E24");var subQ1=sQuery(id+"F0.wireOp",EDGE,"E13");var subQ2=makeQuery(id+"F0.imprint","INTERSECT",VERTEX,{"derivedFrom":[subQ1,subQ0]});Q81=makeQuery(id+"F0.imprint","IMPRINT",FACE,{"disambiguationData":[TD([[makeQuery(id+"F0.imprint","IMPRINT",EDGE,{"disambiguationData":[TD([[subQ2,-1.0]])],"derivedFrom":subQ1}),1.0]])]});}
            var Q82;
            {var subQ0=sQuery(id+"F0.wireOp",EDGE,"E31");var subQ1=sQuery(id+"F0.wireOp",EDGE,"E10");var subQ2=makeQuery(id+"F0.imprint","INTERSECT",VERTEX,{"derivedFrom":[subQ1,subQ0]});Q82=makeQuery(id+"F0.imprint","IMPRINT",FACE,{"disambiguationData":[TD([[makeQuery(id+"F0.imprint","IMPRINT",EDGE,{"disambiguationData":[TD([[subQ2,-1.0]])],"derivedFrom":subQ1}),1.0]])]});}
            var Q83;
            {var subQ0=sQuery(id+"F0.wireOp",EDGE,"E26");var subQ1=sQuery(id+"F0.wireOp",EDGE,"E8");var subQ2=makeQuery(id+"F0.imprint","INTERSECT",VERTEX,{"derivedFrom":[subQ1,subQ0]});Q83=makeQuery(id+"F0.imprint","IMPRINT",FACE,{"disambiguationData":[TD([[makeQuery(id+"F0.imprint","IMPRINT",EDGE,{"disambiguationData":[TD([[subQ2,-1.0]])],"derivedFrom":subQ1}),1.0]])]});}
            var Q84;
            {var subQ0=sQuery(id+"F0.wireOp",EDGE,"E32");var subQ1=sQuery(id+"F0.wireOp",EDGE,"E12");var subQ2=makeQuery(id+"F0.imprint","INTERSECT",VERTEX,{"derivedFrom":[subQ1,subQ0]});Q84=makeQuery(id+"F0.imprint","IMPRINT",FACE,{"disambiguationData":[TD([[makeQuery(id+"F0.imprint","IMPRINT",EDGE,{"disambiguationData":[TD([[subQ2,-1.0]])],"derivedFrom":subQ1}),1.0]])]});}
            var Q85;
            {var subQ0=sQuery(id+"F0.wireOp",EDGE,"E23");var subQ1=sQuery(id+"F0.wireOp",EDGE,"E6");var subQ2=makeQuery(id+"F0.imprint","INTERSECT",VERTEX,{"derivedFrom":[subQ1,subQ0]});Q85=makeQuery(id+"F0.imprint","IMPRINT",FACE,{"disambiguationData":[TD([[makeQuery(id+"F0.imprint","IMPRINT",EDGE,{"disambiguationData":[TD([[subQ2,-1.0]])],"derivedFrom":subQ1}),1.0]])]});}
            var Q86;
            {var subQ0=sQuery(id+"F0.wireOp",EDGE,"E32");var subQ1=sQuery(id+"F0.wireOp",EDGE,"E8");var subQ2=makeQuery(id+"F0.imprint","INTERSECT",VERTEX,{"derivedFrom":[subQ1,subQ0]});Q86=makeQuery(id+"F0.imprint","IMPRINT",FACE,{"disambiguationData":[TD([[makeQuery(id+"F0.imprint","IMPRINT",EDGE,{"disambiguationData":[TD([[subQ2,-1.0]])],"derivedFrom":subQ1}),1.0]])]});}
            var Q87;
            {var subQ0=sQuery(id+"F0.wireOp",EDGE,"E27");var subQ1=sQuery(id+"F0.wireOp",EDGE,"E14");var subQ2=makeQuery(id+"F0.imprint","INTERSECT",VERTEX,{"derivedFrom":[subQ1,subQ0]});Q87=makeQuery(id+"F0.imprint","IMPRINT",FACE,{"disambiguationData":[TD([[makeQuery(id+"F0.imprint","IMPRINT",EDGE,{"disambiguationData":[TD([[subQ2,-1.0]])],"derivedFrom":subQ1}),1.0]])]});}
            var Q88;
            {var subQ0=sQuery(id+"F0.wireOp",EDGE,"E22");var subQ1=sQuery(id+"F0.wireOp",EDGE,"E1");var subQ2=makeQuery(id+"F0.imprint","INTERSECT",VERTEX,{"derivedFrom":[subQ1,subQ0]});Q88=makeQuery(id+"F0.imprint","IMPRINT",FACE,{"disambiguationData":[TD([[makeQuery(id+"F0.imprint","IMPRINT",EDGE,{"disambiguationData":[TD([[subQ2,-1.0]])],"derivedFrom":subQ1}),1.0]])]});}
            var Q89;
            {var subQ0=sQuery(id+"F0.wireOp",EDGE,"E26");var subQ1=sQuery(id+"F0.wireOp",EDGE,"E17");var subQ2=makeQuery(id+"F0.imprint","INTERSECT",VERTEX,{"derivedFrom":[subQ1,subQ0]});Q89=makeQuery(id+"F0.imprint","IMPRINT",FACE,{"disambiguationData":[TD([[makeQuery(id+"F0.imprint","IMPRINT",EDGE,{"disambiguationData":[TD([[subQ2,-1.0]])],"derivedFrom":subQ1}),1.0]])]});}
            var Q90;
            {var subQ0=sQuery(id+"F0.wireOp",EDGE,"E32");var subQ1=sQuery(id+"F0.wireOp",EDGE,"E15");var subQ2=makeQuery(id+"F0.imprint","INTERSECT",VERTEX,{"derivedFrom":[subQ1,subQ0]});Q90=makeQuery(id+"F0.imprint","IMPRINT",FACE,{"disambiguationData":[TD([[makeQuery(id+"F0.imprint","IMPRINT",EDGE,{"disambiguationData":[TD([[subQ2,-1.0]])],"derivedFrom":subQ1}),1.0]])]});}
            var Q91;
            {var subQ0=sQuery(id+"F0.wireOp",EDGE,"E25");var subQ1=sQuery(id+"F0.wireOp",EDGE,"E12");var subQ2=makeQuery(id+"F0.imprint","INTERSECT",VERTEX,{"derivedFrom":[subQ1,subQ0]});Q91=makeQuery(id+"F0.imprint","IMPRINT",FACE,{"disambiguationData":[TD([[makeQuery(id+"F0.imprint","IMPRINT",EDGE,{"disambiguationData":[TD([[subQ2,-1.0]])],"derivedFrom":subQ1}),1.0]])]});}
            var Q92;
            {var subQ0=sQuery(id+"F0.wireOp",EDGE,"E26");var subQ1=sQuery(id+"F0.wireOp",EDGE,"E7");var subQ2=makeQuery(id+"F0.imprint","INTERSECT",VERTEX,{"derivedFrom":[subQ1,subQ0]});Q92=makeQuery(id+"F0.imprint","IMPRINT",FACE,{"disambiguationData":[TD([[makeQuery(id+"F0.imprint","IMPRINT",EDGE,{"disambiguationData":[TD([[subQ2,-1.0]])],"derivedFrom":subQ1}),1.0]])]});}
            var Q93;
            {var subQ0=sQuery(id+"F0.wireOp",EDGE,"E22");var subQ1=sQuery(id+"F0.wireOp",EDGE,"E6");var subQ2=makeQuery(id+"F0.imprint","INTERSECT",VERTEX,{"derivedFrom":[subQ1,subQ0]});Q93=makeQuery(id+"F0.imprint","IMPRINT",FACE,{"disambiguationData":[TD([[makeQuery(id+"F0.imprint","IMPRINT",EDGE,{"disambiguationData":[TD([[subQ2,-1.0]])],"derivedFrom":subQ1}),1.0]])]});}
            var Q94;
            {var subQ0=sQuery(id+"F0.wireOp",EDGE,"E33");var subQ1=sQuery(id+"F0.wireOp",EDGE,"E2");var subQ2=makeQuery(id+"F0.imprint","INTERSECT",VERTEX,{"derivedFrom":[subQ1,subQ0]});Q94=makeQuery(id+"F0.imprint","IMPRINT",FACE,{"disambiguationData":[TD([[makeQuery(id+"F0.imprint","IMPRINT",EDGE,{"disambiguationData":[TD([[subQ2,-1.0]])],"derivedFrom":subQ1}),1.0]])]});}
            var Q95;
            {var subQ0=sQuery(id+"F0.wireOp",EDGE,"E21");var subQ1=sQuery(id+"F0.wireOp",EDGE,"E8");var subQ2=makeQuery(id+"F0.imprint","INTERSECT",VERTEX,{"derivedFrom":[subQ1,subQ0]});Q95=makeQuery(id+"F0.imprint","IMPRINT",FACE,{"disambiguationData":[TD([[makeQuery(id+"F0.imprint","IMPRINT",EDGE,{"disambiguationData":[TD([[subQ2,-1.0]])],"derivedFrom":subQ1}),1.0]])]});}
            var Q96;
            {var subQ0=sQuery(id+"F0.wireOp",EDGE,"E22");var subQ1=sQuery(id+"F0.wireOp",EDGE,"E11");var subQ2=makeQuery(id+"F0.imprint","INTERSECT",VERTEX,{"derivedFrom":[subQ1,subQ0]});Q96=makeQuery(id+"F0.imprint","IMPRINT",FACE,{"disambiguationData":[TD([[makeQuery(id+"F0.imprint","IMPRINT",EDGE,{"disambiguationData":[TD([[subQ2,-1.0]])],"derivedFrom":subQ1}),1.0]])]});}
            var Q97;
            {var subQ0=sQuery(id+"F0.wireOp",EDGE,"E32");var subQ1=sQuery(id+"F0.wireOp",EDGE,"E13");var subQ2=makeQuery(id+"F0.imprint","INTERSECT",VERTEX,{"derivedFrom":[subQ1,subQ0]});Q97=makeQuery(id+"F0.imprint","IMPRINT",FACE,{"disambiguationData":[TD([[makeQuery(id+"F0.imprint","IMPRINT",EDGE,{"disambiguationData":[TD([[subQ2,-1.0]])],"derivedFrom":subQ1}),1.0]])]});}
            var Q98;
            {var subQ0=sQuery(id+"F0.wireOp",EDGE,"E21");var subQ1=sQuery(id+"F0.wireOp",EDGE,"E14");var subQ2=makeQuery(id+"F0.imprint","INTERSECT",VERTEX,{"derivedFrom":[subQ1,subQ0]});Q98=makeQuery(id+"F0.imprint","IMPRINT",FACE,{"disambiguationData":[TD([[makeQuery(id+"F0.imprint","IMPRINT",EDGE,{"disambiguationData":[TD([[subQ2,-1.0]])],"derivedFrom":subQ1}),1.0]])]});}
            var Q99;
            {var subQ0=sQuery(id+"F0.wireOp",EDGE,"E29");var subQ1=sQuery(id+"F0.wireOp",EDGE,"E6");var subQ2=makeQuery(id+"F0.imprint","INTERSECT",VERTEX,{"derivedFrom":[subQ1,subQ0]});Q99=makeQuery(id+"F0.imprint","IMPRINT",FACE,{"disambiguationData":[TD([[makeQuery(id+"F0.imprint","IMPRINT",EDGE,{"disambiguationData":[TD([[subQ2,-1.0]])],"derivedFrom":subQ1}),1.0]])]});}
            var Q100;
            {var subQ0=sQuery(id+"F0.wireOp",EDGE,"E30");var subQ1=sQuery(id+"F0.wireOp",EDGE,"E1");var subQ2=makeQuery(id+"F0.imprint","INTERSECT",VERTEX,{"derivedFrom":[subQ1,subQ0]});Q100=makeQuery(id+"F0.imprint","IMPRINT",FACE,{"disambiguationData":[TD([[makeQuery(id+"F0.imprint","IMPRINT",EDGE,{"disambiguationData":[TD([[subQ2,-1.0]])],"derivedFrom":subQ1}),1.0]])]});}
            var Q101;
            {var subQ0=sQuery(id+"F0.wireOp",EDGE,"E35");var subQ1=sQuery(id+"F0.wireOp",EDGE,"E6");var subQ2=makeQuery(id+"F0.imprint","INTERSECT",VERTEX,{"derivedFrom":[subQ1,subQ0]});Q101=makeQuery(id+"F0.imprint","IMPRINT",FACE,{"disambiguationData":[TD([[makeQuery(id+"F0.imprint","IMPRINT",EDGE,{"disambiguationData":[TD([[subQ2,-1.0]])],"derivedFrom":subQ1}),1.0]])]});}
            var Q102;
            {var subQ0=sQuery(id+"F0.wireOp",EDGE,"E19");var subQ1=sQuery(id+"F0.wireOp",EDGE,"E6");var subQ2=makeQuery(id+"F0.imprint","INTERSECT",VERTEX,{"derivedFrom":[subQ1,subQ0]});Q102=makeQuery(id+"F0.imprint","IMPRINT",FACE,{"disambiguationData":[TD([[makeQuery(id+"F0.imprint","IMPRINT",EDGE,{"disambiguationData":[TD([[subQ2,-1.0]])],"derivedFrom":subQ1}),1.0]])]});}
            var Q103;
            {var subQ0=sQuery(id+"F0.wireOp",EDGE,"E30");var subQ1=sQuery(id+"F0.wireOp",EDGE,"E8");var subQ2=makeQuery(id+"F0.imprint","INTERSECT",VERTEX,{"derivedFrom":[subQ1,subQ0]});Q103=makeQuery(id+"F0.imprint","IMPRINT",FACE,{"disambiguationData":[TD([[makeQuery(id+"F0.imprint","IMPRINT",EDGE,{"disambiguationData":[TD([[subQ2,-1.0]])],"derivedFrom":subQ1}),1.0]])]});}
            var Q104;
            {var subQ0=sQuery(id+"F0.wireOp",EDGE,"E30");var subQ1=sQuery(id+"F0.wireOp",EDGE,"E2");var subQ2=makeQuery(id+"F0.imprint","INTERSECT",VERTEX,{"derivedFrom":[subQ1,subQ0]});Q104=makeQuery(id+"F0.imprint","IMPRINT",FACE,{"disambiguationData":[TD([[makeQuery(id+"F0.imprint","IMPRINT",EDGE,{"disambiguationData":[TD([[subQ2,-1.0]])],"derivedFrom":subQ1}),1.0]])]});}
            var Q105;
            {var subQ0=sQuery(id+"F0.wireOp",EDGE,"E21");var subQ1=sQuery(id+"F0.wireOp",EDGE,"E2");var subQ2=makeQuery(id+"F0.imprint","INTERSECT",VERTEX,{"derivedFrom":[subQ1,subQ0]});Q105=makeQuery(id+"F0.imprint","IMPRINT",FACE,{"disambiguationData":[TD([[makeQuery(id+"F0.imprint","IMPRINT",EDGE,{"disambiguationData":[TD([[subQ2,-1.0]])],"derivedFrom":subQ1}),1.0]])]});}
            var Q106;
            {var subQ0=sQuery(id+"F0.wireOp",EDGE,"E27");var subQ1=sQuery(id+"F0.wireOp",EDGE,"E6");var subQ2=makeQuery(id+"F0.imprint","INTERSECT",VERTEX,{"derivedFrom":[subQ1,subQ0]});Q106=makeQuery(id+"F0.imprint","IMPRINT",FACE,{"disambiguationData":[TD([[makeQuery(id+"F0.imprint","IMPRINT",EDGE,{"disambiguationData":[TD([[subQ2,-1.0]])],"derivedFrom":subQ1}),1.0]])]});}
            var Q107;
            {var subQ0=sQuery(id+"F0.wireOp",EDGE,"E19");var subQ1=sQuery(id+"F0.wireOp",EDGE,"E8");var subQ2=makeQuery(id+"F0.imprint","INTERSECT",VERTEX,{"derivedFrom":[subQ1,subQ0]});Q107=makeQuery(id+"F0.imprint","IMPRINT",FACE,{"disambiguationData":[TD([[makeQuery(id+"F0.imprint","IMPRINT",EDGE,{"disambiguationData":[TD([[subQ2,-1.0]])],"derivedFrom":subQ1}),1.0]])]});}
            var Q108;
            {var subQ0=sQuery(id+"F0.wireOp",EDGE,"E30");var subQ1=sQuery(id+"F0.wireOp",EDGE,"E16");var subQ2=makeQuery(id+"F0.imprint","INTERSECT",VERTEX,{"derivedFrom":[subQ1,subQ0]});Q108=makeQuery(id+"F0.imprint","IMPRINT",FACE,{"disambiguationData":[TD([[makeQuery(id+"F0.imprint","IMPRINT",EDGE,{"disambiguationData":[TD([[subQ2,-1.0]])],"derivedFrom":subQ1}),1.0]])]});}
            var Q109;
            {var subQ0=sQuery(id+"F0.wireOp",EDGE,"E24");var subQ1=sQuery(id+"F0.wireOp",EDGE,"E16");var subQ2=makeQuery(id+"F0.imprint","INTERSECT",VERTEX,{"derivedFrom":[subQ1,subQ0]});Q109=makeQuery(id+"F0.imprint","IMPRINT",FACE,{"disambiguationData":[TD([[makeQuery(id+"F0.imprint","IMPRINT",EDGE,{"disambiguationData":[TD([[subQ2,-1.0]])],"derivedFrom":subQ1}),1.0]])]});}
            var Q110;
            {var subQ0=sQuery(id+"F0.wireOp",EDGE,"E19");var subQ1=sQuery(id+"F0.wireOp",EDGE,"E12");var subQ2=makeQuery(id+"F0.imprint","INTERSECT",VERTEX,{"derivedFrom":[subQ1,subQ0]});Q110=makeQuery(id+"F0.imprint","IMPRINT",FACE,{"disambiguationData":[TD([[makeQuery(id+"F0.imprint","IMPRINT",EDGE,{"disambiguationData":[TD([[subQ2,-1.0]])],"derivedFrom":subQ1}),1.0]])]});}
            var Q111;
            {var subQ0=sQuery(id+"F0.wireOp",EDGE,"E27");var subQ1=sQuery(id+"F0.wireOp",EDGE,"E8");var subQ2=makeQuery(id+"F0.imprint","INTERSECT",VERTEX,{"derivedFrom":[subQ1,subQ0]});Q111=makeQuery(id+"F0.imprint","IMPRINT",FACE,{"disambiguationData":[TD([[makeQuery(id+"F0.imprint","IMPRINT",EDGE,{"disambiguationData":[TD([[subQ2,-1.0]])],"derivedFrom":subQ1}),1.0]])]});}
            var Q112;
            {var subQ0=sQuery(id+"F0.wireOp",EDGE,"E22");var subQ1=sQuery(id+"F0.wireOp",EDGE,"E7");var subQ2=makeQuery(id+"F0.imprint","INTERSECT",VERTEX,{"derivedFrom":[subQ1,subQ0]});Q112=makeQuery(id+"F0.imprint","IMPRINT",FACE,{"disambiguationData":[TD([[makeQuery(id+"F0.imprint","IMPRINT",EDGE,{"disambiguationData":[TD([[subQ2,-1.0]])],"derivedFrom":subQ1}),1.0]])]});}
            var Q113;
            {var subQ0=sQuery(id+"F0.wireOp",EDGE,"E26");var subQ1=sQuery(id+"F0.wireOp",EDGE,"E10");var subQ2=makeQuery(id+"F0.imprint","INTERSECT",VERTEX,{"derivedFrom":[subQ1,subQ0]});Q113=makeQuery(id+"F0.imprint","IMPRINT",FACE,{"disambiguationData":[TD([[makeQuery(id+"F0.imprint","IMPRINT",EDGE,{"disambiguationData":[TD([[subQ2,-1.0]])],"derivedFrom":subQ1}),1.0]])]});}
            var Q114;
            {var subQ0=sQuery(id+"F0.wireOp",EDGE,"E25");var subQ1=sQuery(id+"F0.wireOp",EDGE,"E10");var subQ2=makeQuery(id+"F0.imprint","INTERSECT",VERTEX,{"derivedFrom":[subQ1,subQ0]});Q114=makeQuery(id+"F0.imprint","IMPRINT",FACE,{"disambiguationData":[TD([[makeQuery(id+"F0.imprint","IMPRINT",EDGE,{"disambiguationData":[TD([[subQ2,-1.0]])],"derivedFrom":subQ1}),1.0]])]});}
            var Q115;
            {var subQ0=sQuery(id+"F0.wireOp",EDGE,"E21");var subQ1=sQuery(id+"F0.wireOp",EDGE,"E6");var subQ2=makeQuery(id+"F0.imprint","INTERSECT",VERTEX,{"derivedFrom":[subQ1,subQ0]});Q115=makeQuery(id+"F0.imprint","IMPRINT",FACE,{"disambiguationData":[TD([[makeQuery(id+"F0.imprint","IMPRINT",EDGE,{"disambiguationData":[TD([[subQ2,-1.0]])],"derivedFrom":subQ1}),1.0]])]});}
            var Q116;
            {var subQ0=sQuery(id+"F0.wireOp",EDGE,"E29");var subQ1=sQuery(id+"F0.wireOp",EDGE,"E2");var subQ2=makeQuery(id+"F0.imprint","INTERSECT",VERTEX,{"derivedFrom":[subQ1,subQ0]});Q116=makeQuery(id+"F0.imprint","IMPRINT",FACE,{"disambiguationData":[TD([[makeQuery(id+"F0.imprint","IMPRINT",EDGE,{"disambiguationData":[TD([[subQ2,-1.0]])],"derivedFrom":subQ1}),1.0]])]});}
            var Q117;
            {var subQ0=sQuery(id+"F0.wireOp",EDGE,"E27");var subQ1=sQuery(id+"F0.wireOp",EDGE,"E12");var subQ2=makeQuery(id+"F0.imprint","INTERSECT",VERTEX,{"derivedFrom":[subQ1,subQ0]});Q117=makeQuery(id+"F0.imprint","IMPRINT",FACE,{"disambiguationData":[TD([[makeQuery(id+"F0.imprint","IMPRINT",EDGE,{"disambiguationData":[TD([[subQ2,-1.0]])],"derivedFrom":subQ1}),1.0]])]});}
            var Q118;
            {var subQ0=sQuery(id+"F0.wireOp",EDGE,"E32");var subQ1=sQuery(id+"F0.wireOp",EDGE,"E2");var subQ2=makeQuery(id+"F0.imprint","INTERSECT",VERTEX,{"derivedFrom":[subQ1,subQ0]});Q118=makeQuery(id+"F0.imprint","IMPRINT",FACE,{"disambiguationData":[TD([[makeQuery(id+"F0.imprint","IMPRINT",EDGE,{"disambiguationData":[TD([[subQ2,-1.0]])],"derivedFrom":subQ1}),1.0]])]});}
            var Q119;
            {var subQ0=sQuery(id+"F0.wireOp",EDGE,"E22");var subQ1=sQuery(id+"F0.wireOp",EDGE,"E12");var subQ2=makeQuery(id+"F0.imprint","INTERSECT",VERTEX,{"derivedFrom":[subQ1,subQ0]});Q119=makeQuery(id+"F0.imprint","IMPRINT",FACE,{"disambiguationData":[TD([[makeQuery(id+"F0.imprint","IMPRINT",EDGE,{"disambiguationData":[TD([[subQ2,-1.0]])],"derivedFrom":subQ1}),1.0]])]});}
            var Q120;
            {var subQ0=sQuery(id+"F0.wireOp",EDGE,"E26");var subQ1=sQuery(id+"F0.wireOp",EDGE,"E15");var subQ2=makeQuery(id+"F0.imprint","INTERSECT",VERTEX,{"derivedFrom":[subQ1,subQ0]});Q120=makeQuery(id+"F0.imprint","IMPRINT",FACE,{"disambiguationData":[TD([[makeQuery(id+"F0.imprint","IMPRINT",EDGE,{"disambiguationData":[TD([[subQ2,-1.0]])],"derivedFrom":subQ1}),1.0]])]});}
            var Q121;
            {var subQ0=sQuery(id+"F0.wireOp",EDGE,"E24");var subQ1=sQuery(id+"F0.wireOp",EDGE,"E14");var subQ2=makeQuery(id+"F0.imprint","INTERSECT",VERTEX,{"derivedFrom":[subQ1,subQ0]});Q121=makeQuery(id+"F0.imprint","IMPRINT",FACE,{"disambiguationData":[TD([[makeQuery(id+"F0.imprint","IMPRINT",EDGE,{"disambiguationData":[TD([[subQ2,-1.0]])],"derivedFrom":subQ1}),1.0]])]});}
            var Q122;
            {var subQ0=sQuery(id+"F0.wireOp",EDGE,"E21");var subQ1=sQuery(id+"F0.wireOp",EDGE,"E12");var subQ2=makeQuery(id+"F0.imprint","INTERSECT",VERTEX,{"derivedFrom":[subQ1,subQ0]});Q122=makeQuery(id+"F0.imprint","IMPRINT",FACE,{"disambiguationData":[TD([[makeQuery(id+"F0.imprint","IMPRINT",EDGE,{"disambiguationData":[TD([[subQ2,-1.0]])],"derivedFrom":subQ1}),1.0]])]});}
            var Q123;
            {var subQ0=sQuery(id+"F0.wireOp",EDGE,"E22");var subQ1=sQuery(id+"F0.wireOp",EDGE,"E5");var subQ2=makeQuery(id+"F0.imprint","INTERSECT",VERTEX,{"derivedFrom":[subQ1,subQ0]});Q123=makeQuery(id+"F0.imprint","IMPRINT",FACE,{"disambiguationData":[TD([[makeQuery(id+"F0.imprint","IMPRINT",EDGE,{"disambiguationData":[TD([[subQ2,-1.0]])],"derivedFrom":subQ1}),1.0]])]});}
            var Q124;
            {var subQ0=sQuery(id+"F0.wireOp",EDGE,"E24");var subQ1=sQuery(id+"F0.wireOp",EDGE,"E15");var subQ2=makeQuery(id+"F0.imprint","INTERSECT",VERTEX,{"derivedFrom":[subQ1,subQ0]});Q124=makeQuery(id+"F0.imprint","IMPRINT",FACE,{"disambiguationData":[TD([[makeQuery(id+"F0.imprint","IMPRINT",EDGE,{"disambiguationData":[TD([[subQ2,-1.0]])],"derivedFrom":subQ1}),1.0]])]});}
            var Q125;
            {var subQ0=sQuery(id+"F0.wireOp",EDGE,"E29");var subQ1=sQuery(id+"F0.wireOp",EDGE,"E14");var subQ2=makeQuery(id+"F0.imprint","INTERSECT",VERTEX,{"derivedFrom":[subQ1,subQ0]});Q125=makeQuery(id+"F0.imprint","IMPRINT",FACE,{"disambiguationData":[TD([[makeQuery(id+"F0.imprint","IMPRINT",EDGE,{"disambiguationData":[TD([[subQ2,-1.0]])],"derivedFrom":subQ1}),1.0]])]});}
            var Q126;
            {var subQ0=sQuery(id+"F0.wireOp",EDGE,"E31");var subQ1=sQuery(id+"F0.wireOp",EDGE,"E16");var subQ2=makeQuery(id+"F0.imprint","INTERSECT",VERTEX,{"derivedFrom":[subQ1,subQ0]});Q126=makeQuery(id+"F0.imprint","IMPRINT",FACE,{"disambiguationData":[TD([[makeQuery(id+"F0.imprint","IMPRINT",EDGE,{"disambiguationData":[TD([[subQ2,-1.0]])],"derivedFrom":subQ1}),1.0]])]});}
            var Q127;
            {var subQ0=sQuery(id+"F0.wireOp",EDGE,"E34");var subQ1=sQuery(id+"F0.wireOp",EDGE,"E15");var subQ2=makeQuery(id+"F0.imprint","INTERSECT",VERTEX,{"derivedFrom":[subQ1,subQ0]});Q127=makeQuery(id+"F0.imprint","IMPRINT",FACE,{"disambiguationData":[TD([[makeQuery(id+"F0.imprint","IMPRINT",EDGE,{"disambiguationData":[TD([[subQ2,-1.0]])],"derivedFrom":subQ1}),1.0]])]});}
            var Q128;
            {var subQ0=sQuery(id+"F0.wireOp",EDGE,"E20");var subQ1=sQuery(id+"F0.wireOp",EDGE,"E6");var subQ2=makeQuery(id+"F0.imprint","INTERSECT",VERTEX,{"derivedFrom":[subQ1,subQ0]});Q128=makeQuery(id+"F0.imprint","IMPRINT",FACE,{"disambiguationData":[TD([[makeQuery(id+"F0.imprint","IMPRINT",EDGE,{"disambiguationData":[TD([[subQ2,-1.0]])],"derivedFrom":subQ1}),1.0]])]});}
            var Q129;
            {var subQ0=sQuery(id+"F0.wireOp",EDGE,"E22");var subQ1=sQuery(id+"F0.wireOp",EDGE,"E0.right");var subQ2=makeQuery(id+"F0.imprint","INTERSECT",VERTEX,{"derivedFrom":[subQ1,subQ0]});Q129=makeQuery(id+"F0.imprint","IMPRINT",FACE,{"disambiguationData":[TD([[makeQuery(id+"F0.imprint","IMPRINT",EDGE,{"disambiguationData":[TD([[subQ2,-1.0]])],"derivedFrom":subQ1}),-1.0]])]});}
            var Q130;
            {var subQ0=sQuery(id+"F0.wireOp",EDGE,"E7");var subQ1=sQuery(id+"F0.wireOp",EDGE,"E0.bottom");var subQ2=makeQuery(id+"F0.imprint","INTERSECT",VERTEX,{"derivedFrom":[subQ1,subQ0]});Q130=makeQuery(id+"F0.imprint","IMPRINT",FACE,{"disambiguationData":[TD([[makeQuery(id+"F0.imprint","IMPRINT",EDGE,{"disambiguationData":[TD([[subQ2,-1.0]])],"derivedFrom":subQ1}),-1.0]])]});}
            var Q131;
            {var subQ0=sQuery(id+"F0.wireOp",EDGE,"E20");var subQ1=sQuery(id+"F0.wireOp",EDGE,"E15");var subQ2=makeQuery(id+"F0.imprint","INTERSECT",VERTEX,{"derivedFrom":[subQ1,subQ0]});Q131=makeQuery(id+"F0.imprint","IMPRINT",FACE,{"disambiguationData":[TD([[makeQuery(id+"F0.imprint","IMPRINT",EDGE,{"disambiguationData":[TD([[subQ2,-1.0]])],"derivedFrom":subQ1}),1.0]])]});}
            var Q132;
            {var subQ0=sQuery(id+"F0.wireOp",EDGE,"E30");var subQ1=sQuery(id+"F0.wireOp",EDGE,"E0.left");var subQ2=makeQuery(id+"F0.imprint","INTERSECT",VERTEX,{"derivedFrom":[subQ1,subQ0]});Q132=makeQuery(id+"F0.imprint","IMPRINT",FACE,{"disambiguationData":[TD([[makeQuery(id+"F0.imprint","IMPRINT",EDGE,{"disambiguationData":[TD([[subQ2,-1.0]])],"derivedFrom":subQ1}),1.0]])]});}
            var Q133;
            {var subQ0=sQuery(id+"F0.wireOp",EDGE,"E20");var subQ1=sQuery(id+"F0.wireOp",EDGE,"E1");var subQ2=makeQuery(id+"F0.imprint","INTERSECT",VERTEX,{"derivedFrom":[subQ1,subQ0]});Q133=makeQuery(id+"F0.imprint","IMPRINT",FACE,{"disambiguationData":[TD([[makeQuery(id+"F0.imprint","IMPRINT",EDGE,{"disambiguationData":[TD([[subQ2,-1.0]])],"derivedFrom":subQ1}),1.0]])]});}
            var Q134;
            {var subQ0=sQuery(id+"F0.wireOp",EDGE,"E28");var subQ1=sQuery(id+"F0.wireOp",EDGE,"E12");var subQ2=makeQuery(id+"F0.imprint","INTERSECT",VERTEX,{"derivedFrom":[subQ1,subQ0]});Q134=makeQuery(id+"F0.imprint","IMPRINT",FACE,{"disambiguationData":[TD([[makeQuery(id+"F0.imprint","IMPRINT",EDGE,{"disambiguationData":[TD([[subQ2,-1.0]])],"derivedFrom":subQ1}),1.0]])]});}
            var Q135;
            {var subQ0=sQuery(id+"F0.wireOp",EDGE,"E35");var subQ1=sQuery(id+"F0.wireOp",EDGE,"E0.left");var subQ2=makeQuery(id+"F0.imprint","INTERSECT",VERTEX,{"derivedFrom":[subQ1,subQ0]});Q135=makeQuery(id+"F0.imprint","IMPRINT",FACE,{"disambiguationData":[TD([[makeQuery(id+"F0.imprint","IMPRINT",EDGE,{"disambiguationData":[TD([[subQ2,-1.0]])],"derivedFrom":subQ1}),1.0]])]});}
            var Q136;
            {var subQ0=sQuery(id+"F0.wireOp",EDGE,"E34");var subQ1=sQuery(id+"F0.wireOp",EDGE,"E17");var subQ2=makeQuery(id+"F0.imprint","INTERSECT",VERTEX,{"derivedFrom":[subQ1,subQ0]});Q136=makeQuery(id+"F0.imprint","IMPRINT",FACE,{"disambiguationData":[TD([[makeQuery(id+"F0.imprint","IMPRINT",EDGE,{"disambiguationData":[TD([[subQ2,-1.0]])],"derivedFrom":subQ1}),1.0]])]});}
            var Q137;
            {var subQ0=sQuery(id+"F0.wireOp",EDGE,"E28");var subQ1=sQuery(id+"F0.wireOp",EDGE,"E11");var subQ2=makeQuery(id+"F0.imprint","INTERSECT",VERTEX,{"derivedFrom":[subQ1,subQ0]});Q137=makeQuery(id+"F0.imprint","IMPRINT",FACE,{"disambiguationData":[TD([[makeQuery(id+"F0.imprint","IMPRINT",EDGE,{"disambiguationData":[TD([[subQ2,-1.0]])],"derivedFrom":subQ1}),1.0]])]});}
            var Q138;
            {var subQ0=sQuery(id+"F0.wireOp",EDGE,"E35");var subQ1=sQuery(id+"F0.wireOp",EDGE,"E0.right");var subQ2=makeQuery(id+"F0.imprint","INTERSECT",VERTEX,{"derivedFrom":[subQ1,subQ0]});Q138=makeQuery(id+"F0.imprint","IMPRINT",FACE,{"disambiguationData":[TD([[makeQuery(id+"F0.imprint","IMPRINT",EDGE,{"disambiguationData":[TD([[subQ2,-1.0]])],"derivedFrom":subQ1}),-1.0]])]});}
            var Q139;
            {var subQ0=sQuery(id+"F0.wireOp",EDGE,"E28");var subQ1=sQuery(id+"F0.wireOp",EDGE,"E10");var subQ2=makeQuery(id+"F0.imprint","INTERSECT",VERTEX,{"derivedFrom":[subQ1,subQ0]});Q139=makeQuery(id+"F0.imprint","IMPRINT",FACE,{"disambiguationData":[TD([[makeQuery(id+"F0.imprint","IMPRINT",EDGE,{"disambiguationData":[TD([[subQ2,-1.0]])],"derivedFrom":subQ1}),1.0]])]});}
            var Q140;
            {var subQ0=sQuery(id+"F0.wireOp",EDGE,"E17");var subQ1=sQuery(id+"F0.wireOp",EDGE,"E0.bottom");var subQ2=makeQuery(id+"F0.imprint","INTERSECT",VERTEX,{"derivedFrom":[subQ1,subQ0]});Q140=makeQuery(id+"F0.imprint","IMPRINT",FACE,{"disambiguationData":[TD([[makeQuery(id+"F0.imprint","IMPRINT",EDGE,{"disambiguationData":[TD([[subQ2,-1.0]])],"derivedFrom":subQ1}),-1.0]])]});}
            var Q141;
            {var subQ0=sQuery(id+"F0.wireOp",EDGE,"E13");var subQ1=sQuery(id+"F0.wireOp",EDGE,"E0.bottom");var subQ2=makeQuery(id+"F0.imprint","INTERSECT",VERTEX,{"derivedFrom":[subQ1,subQ0]});Q141=makeQuery(id+"F0.imprint","IMPRINT",FACE,{"disambiguationData":[TD([[makeQuery(id+"F0.imprint","IMPRINT",EDGE,{"disambiguationData":[TD([[subQ2,-1.0]])],"derivedFrom":subQ1}),-1.0]])]});}
            var Q142;
            {var subQ0=sQuery(id+"F0.wireOp",EDGE,"E20");var subQ1=sQuery(id+"F0.wireOp",EDGE,"E5");var subQ2=makeQuery(id+"F0.imprint","INTERSECT",VERTEX,{"derivedFrom":[subQ1,subQ0]});Q142=makeQuery(id+"F0.imprint","IMPRINT",FACE,{"disambiguationData":[TD([[makeQuery(id+"F0.imprint","IMPRINT",EDGE,{"disambiguationData":[TD([[subQ2,-1.0]])],"derivedFrom":subQ1}),1.0]])]});}
            var Q143;
            {var subQ0=sQuery(id+"F0.wireOp",EDGE,"E20");var subQ1=sQuery(id+"F0.wireOp",EDGE,"E16");var subQ2=makeQuery(id+"F0.imprint","INTERSECT",VERTEX,{"derivedFrom":[subQ1,subQ0]});Q143=makeQuery(id+"F0.imprint","IMPRINT",FACE,{"disambiguationData":[TD([[makeQuery(id+"F0.imprint","IMPRINT",EDGE,{"disambiguationData":[TD([[subQ2,-1.0]])],"derivedFrom":subQ1}),1.0]])]});}
            var Q144;
            {var subQ0=sQuery(id+"F0.wireOp",EDGE,"E16");var subQ1=sQuery(id+"F0.wireOp",EDGE,"E0.bottom");var subQ2=makeQuery(id+"F0.imprint","INTERSECT",VERTEX,{"derivedFrom":[subQ1,subQ0]});Q144=makeQuery(id+"F0.imprint","IMPRINT",FACE,{"disambiguationData":[TD([[makeQuery(id+"F0.imprint","IMPRINT",EDGE,{"disambiguationData":[TD([[subQ2,-1.0]])],"derivedFrom":subQ1}),-1.0]])]});}
            var Q145;
            {var subQ0=sQuery(id+"F0.wireOp",EDGE,"E33");var subQ1=sQuery(id+"F0.wireOp",EDGE,"E0.right");var subQ2=makeQuery(id+"F0.imprint","INTERSECT",VERTEX,{"derivedFrom":[subQ1,subQ0]});Q145=makeQuery(id+"F0.imprint","IMPRINT",FACE,{"disambiguationData":[TD([[makeQuery(id+"F0.imprint","IMPRINT",EDGE,{"disambiguationData":[TD([[subQ2,-1.0]])],"derivedFrom":subQ1}),-1.0]])]});}
            var Q146;
            {var subQ0=sQuery(id+"F0.wireOp",EDGE,"E28");var subQ1=sQuery(id+"F0.wireOp",EDGE,"E3");var subQ2=makeQuery(id+"F0.imprint","INTERSECT",VERTEX,{"derivedFrom":[subQ1,subQ0]});Q146=makeQuery(id+"F0.imprint","IMPRINT",FACE,{"disambiguationData":[TD([[makeQuery(id+"F0.imprint","IMPRINT",EDGE,{"disambiguationData":[TD([[subQ2,-1.0]])],"derivedFrom":subQ1}),1.0]])]});}
            var Q147;
            {var subQ0=sQuery(id+"F0.wireOp",EDGE,"E28");var subQ1=sQuery(id+"F0.wireOp",EDGE,"E6");var subQ2=makeQuery(id+"F0.imprint","INTERSECT",VERTEX,{"derivedFrom":[subQ1,subQ0]});Q147=makeQuery(id+"F0.imprint","IMPRINT",FACE,{"disambiguationData":[TD([[makeQuery(id+"F0.imprint","IMPRINT",EDGE,{"disambiguationData":[TD([[subQ2,-1.0]])],"derivedFrom":subQ1}),1.0]])]});}
            var Q148;
            {var subQ0=sQuery(id+"F0.wireOp",EDGE,"E28");var subQ1=sQuery(id+"F0.wireOp",EDGE,"E1");var subQ2=makeQuery(id+"F0.imprint","INTERSECT",VERTEX,{"derivedFrom":[subQ1,subQ0]});Q148=makeQuery(id+"F0.imprint","IMPRINT",FACE,{"disambiguationData":[TD([[makeQuery(id+"F0.imprint","IMPRINT",EDGE,{"disambiguationData":[TD([[subQ2,-1.0]])],"derivedFrom":subQ1}),1.0]])]});}
            var Q149;
            {var subQ0=sQuery(id+"F0.wireOp",EDGE,"E20");var subQ1=sQuery(id+"F0.wireOp",EDGE,"E10");var subQ2=makeQuery(id+"F0.imprint","INTERSECT",VERTEX,{"derivedFrom":[subQ1,subQ0]});Q149=makeQuery(id+"F0.imprint","IMPRINT",FACE,{"disambiguationData":[TD([[makeQuery(id+"F0.imprint","IMPRINT",EDGE,{"disambiguationData":[TD([[subQ2,-1.0]])],"derivedFrom":subQ1}),1.0]])]});}
            var Q150;
            {var subQ0=sQuery(id+"F0.wireOp",EDGE,"E20");var subQ1=sQuery(id+"F0.wireOp",EDGE,"E14");var subQ2=makeQuery(id+"F0.imprint","INTERSECT",VERTEX,{"derivedFrom":[subQ1,subQ0]});Q150=makeQuery(id+"F0.imprint","IMPRINT",FACE,{"disambiguationData":[TD([[makeQuery(id+"F0.imprint","IMPRINT",EDGE,{"disambiguationData":[TD([[subQ2,-1.0]])],"derivedFrom":subQ1}),1.0]])]});}
            var Q151;
            {var subQ0=sQuery(id+"F0.wireOp",EDGE,"E4");var subQ1=sQuery(id+"F0.wireOp",EDGE,"E0.bottom");var subQ2=makeQuery(id+"F0.imprint","INTERSECT",VERTEX,{"derivedFrom":[subQ1,subQ0]});Q151=makeQuery(id+"F0.imprint","IMPRINT",FACE,{"disambiguationData":[TD([[makeQuery(id+"F0.imprint","IMPRINT",EDGE,{"disambiguationData":[TD([[subQ2,-1.0]])],"derivedFrom":subQ1}),-1.0]])]});}
            var Q152;
            {var subQ0=sQuery(id+"F0.wireOp",EDGE,"E14");var subQ1=sQuery(id+"F0.wireOp",EDGE,"E0.bottom");var subQ2=makeQuery(id+"F0.imprint","INTERSECT",VERTEX,{"derivedFrom":[subQ1,subQ0]});Q152=makeQuery(id+"F0.imprint","IMPRINT",FACE,{"disambiguationData":[TD([[makeQuery(id+"F0.imprint","IMPRINT",EDGE,{"disambiguationData":[TD([[subQ2,-1.0]])],"derivedFrom":subQ1}),-1.0]])]});}
            var Q153;
            {var subQ0=sQuery(id+"F0.wireOp",EDGE,"E7");var subQ1=sQuery(id+"F0.wireOp",EDGE,"E0.top");var subQ2=makeQuery(id+"F0.imprint","INTERSECT",VERTEX,{"derivedFrom":[subQ1,subQ0]});Q153=makeQuery(id+"F0.imprint","IMPRINT",FACE,{"disambiguationData":[TD([[makeQuery(id+"F0.imprint","IMPRINT",EDGE,{"disambiguationData":[TD([[subQ2,-1.0]])],"derivedFrom":subQ1}),1.0]])]});}
            var Q154;
            {var subQ0=sQuery(id+"F0.wireOp",EDGE,"E30");var subQ1=sQuery(id+"F0.wireOp",EDGE,"E4");var subQ2=makeQuery(id+"F0.imprint","INTERSECT",VERTEX,{"derivedFrom":[subQ1,subQ0]});Q154=makeQuery(id+"F0.imprint","IMPRINT",FACE,{"disambiguationData":[TD([[makeQuery(id+"F0.imprint","IMPRINT",EDGE,{"disambiguationData":[TD([[subQ2,-1.0]])],"derivedFrom":subQ1}),1.0]])]});}
            var Q155;
            {var subQ0=sQuery(id+"F0.wireOp",EDGE,"E23");var subQ1=sQuery(id+"F0.wireOp",EDGE,"E0.right");var subQ2=makeQuery(id+"F0.imprint","INTERSECT",VERTEX,{"derivedFrom":[subQ1,subQ0]});Q155=makeQuery(id+"F0.imprint","IMPRINT",FACE,{"disambiguationData":[TD([[makeQuery(id+"F0.imprint","IMPRINT",EDGE,{"disambiguationData":[TD([[subQ2,-1.0]])],"derivedFrom":subQ1}),-1.0]])]});}
            var Q156;
            {var subQ0=sQuery(id+"F0.wireOp",EDGE,"E34");var subQ1=sQuery(id+"F0.wireOp",EDGE,"E16");var subQ2=makeQuery(id+"F0.imprint","INTERSECT",VERTEX,{"derivedFrom":[subQ1,subQ0]});Q156=makeQuery(id+"F0.imprint","IMPRINT",FACE,{"disambiguationData":[TD([[makeQuery(id+"F0.imprint","IMPRINT",EDGE,{"disambiguationData":[TD([[subQ2,-1.0]])],"derivedFrom":subQ1}),1.0]])]});}
            var Q157;
            {var subQ0=sQuery(id+"F0.wireOp",EDGE,"E32");var subQ1=sQuery(id+"F0.wireOp",EDGE,"E0.left");var subQ2=makeQuery(id+"F0.imprint","INTERSECT",VERTEX,{"derivedFrom":[subQ1,subQ0]});Q157=makeQuery(id+"F0.imprint","IMPRINT",FACE,{"disambiguationData":[TD([[makeQuery(id+"F0.imprint","IMPRINT",EDGE,{"disambiguationData":[TD([[subQ2,-1.0]])],"derivedFrom":subQ1}),1.0]])]});}
            var Q158;
            {var subQ0=sQuery(id+"F0.wireOp",EDGE,"E34");var subQ1=sQuery(id+"F0.wireOp",EDGE,"E7");var subQ2=makeQuery(id+"F0.imprint","INTERSECT",VERTEX,{"derivedFrom":[subQ1,subQ0]});Q158=makeQuery(id+"F0.imprint","IMPRINT",FACE,{"disambiguationData":[TD([[makeQuery(id+"F0.imprint","IMPRINT",EDGE,{"disambiguationData":[TD([[subQ2,-1.0]])],"derivedFrom":subQ1}),1.0]])]});}
            var Q159;
            {var subQ0=sQuery(id+"F0.wireOp",EDGE,"E14");var subQ1=sQuery(id+"F0.wireOp",EDGE,"E0.top");var subQ2=makeQuery(id+"F0.imprint","INTERSECT",VERTEX,{"derivedFrom":[subQ1,subQ0]});Q159=makeQuery(id+"F0.imprint","IMPRINT",FACE,{"disambiguationData":[TD([[makeQuery(id+"F0.imprint","IMPRINT",EDGE,{"disambiguationData":[TD([[subQ2,-1.0]])],"derivedFrom":subQ1}),1.0]])]});}
            var Q160;
            {var subQ0=sQuery(id+"F0.wireOp",EDGE,"E34");var subQ1=sQuery(id+"F0.wireOp",EDGE,"E1");var subQ2=makeQuery(id+"F0.imprint","INTERSECT",VERTEX,{"derivedFrom":[subQ1,subQ0]});Q160=makeQuery(id+"F0.imprint","IMPRINT",FACE,{"disambiguationData":[TD([[makeQuery(id+"F0.imprint","IMPRINT",EDGE,{"disambiguationData":[TD([[subQ2,-1.0]])],"derivedFrom":subQ1}),1.0]])]});}
            var Q161;
            {var subQ0=sQuery(id+"F0.wireOp",EDGE,"E21");var subQ1=sQuery(id+"F0.wireOp",EDGE,"E0.right");var subQ2=makeQuery(id+"F0.imprint","INTERSECT",VERTEX,{"derivedFrom":[subQ1,subQ0]});Q161=makeQuery(id+"F0.imprint","IMPRINT",FACE,{"disambiguationData":[TD([[makeQuery(id+"F0.imprint","IMPRINT",EDGE,{"disambiguationData":[TD([[subQ2,-1.0]])],"derivedFrom":subQ1}),-1.0]])]});}
            var Q162;
            {var subQ0=sQuery(id+"F0.wireOp",EDGE,"E16");var subQ1=sQuery(id+"F0.wireOp",EDGE,"E0.top");var subQ2=makeQuery(id+"F0.imprint","INTERSECT",VERTEX,{"derivedFrom":[subQ1,subQ0]});Q162=makeQuery(id+"F0.imprint","IMPRINT",FACE,{"disambiguationData":[TD([[makeQuery(id+"F0.imprint","IMPRINT",EDGE,{"disambiguationData":[TD([[subQ2,-1.0]])],"derivedFrom":subQ1}),1.0]])]});}
            var Q163;
            {var subQ0=sQuery(id+"F0.wireOp",EDGE,"E31");var subQ1=sQuery(id+"F0.wireOp",EDGE,"E4");var subQ2=makeQuery(id+"F0.imprint","INTERSECT",VERTEX,{"derivedFrom":[subQ1,subQ0]});Q163=makeQuery(id+"F0.imprint","IMPRINT",FACE,{"disambiguationData":[TD([[makeQuery(id+"F0.imprint","IMPRINT",EDGE,{"disambiguationData":[TD([[subQ2,-1.0]])],"derivedFrom":subQ1}),1.0]])]});}
            var Q164;
            {var subQ0=sQuery(id+"F0.wireOp",EDGE,"E32");var subQ1=sQuery(id+"F0.wireOp",EDGE,"E4");var subQ2=makeQuery(id+"F0.imprint","INTERSECT",VERTEX,{"derivedFrom":[subQ1,subQ0]});Q164=makeQuery(id+"F0.imprint","IMPRINT",FACE,{"disambiguationData":[TD([[makeQuery(id+"F0.imprint","IMPRINT",EDGE,{"disambiguationData":[TD([[subQ2,-1.0]])],"derivedFrom":subQ1}),1.0]])]});}
            var Q165;
            {var subQ0=sQuery(id+"F0.wireOp",EDGE,"E33");var subQ1=sQuery(id+"F0.wireOp",EDGE,"E0.left");var subQ2=makeQuery(id+"F0.imprint","INTERSECT",VERTEX,{"derivedFrom":[subQ1,subQ0]});Q165=makeQuery(id+"F0.imprint","IMPRINT",FACE,{"disambiguationData":[TD([[makeQuery(id+"F0.imprint","IMPRINT",EDGE,{"disambiguationData":[TD([[subQ2,-1.0]])],"derivedFrom":subQ1}),1.0]])]});}
            var Q166;
            {var subQ0=sQuery(id+"F0.wireOp",EDGE,"E20");var subQ1=sQuery(id+"F0.wireOp",EDGE,"E3");var subQ2=makeQuery(id+"F0.imprint","INTERSECT",VERTEX,{"derivedFrom":[subQ1,subQ0]});Q166=makeQuery(id+"F0.imprint","IMPRINT",FACE,{"disambiguationData":[TD([[makeQuery(id+"F0.imprint","IMPRINT",EDGE,{"disambiguationData":[TD([[subQ2,-1.0]])],"derivedFrom":subQ1}),1.0]])]});}
            var Q167;
            {var subQ0=sQuery(id+"F0.wireOp",EDGE,"E20");var subQ1=sQuery(id+"F0.wireOp",EDGE,"E17");var subQ2=makeQuery(id+"F0.imprint","INTERSECT",VERTEX,{"derivedFrom":[subQ1,subQ0]});Q167=makeQuery(id+"F0.imprint","IMPRINT",FACE,{"disambiguationData":[TD([[makeQuery(id+"F0.imprint","IMPRINT",EDGE,{"disambiguationData":[TD([[subQ2,-1.0]])],"derivedFrom":subQ1}),1.0]])]});}
            var Q168;
            {var subQ0=sQuery(id+"F0.wireOp",EDGE,"E28");var subQ1=sQuery(id+"F0.wireOp",EDGE,"E13");var subQ2=makeQuery(id+"F0.imprint","INTERSECT",VERTEX,{"derivedFrom":[subQ1,subQ0]});Q168=makeQuery(id+"F0.imprint","IMPRINT",FACE,{"disambiguationData":[TD([[makeQuery(id+"F0.imprint","IMPRINT",EDGE,{"disambiguationData":[TD([[subQ2,-1.0]])],"derivedFrom":subQ1}),1.0]])]});}
            var Q169;
            {var subQ0=sQuery(id+"F0.wireOp",EDGE,"E35");var subQ1=sQuery(id+"F0.wireOp",EDGE,"E4");var subQ2=makeQuery(id+"F0.imprint","INTERSECT",VERTEX,{"derivedFrom":[subQ1,subQ0]});Q169=makeQuery(id+"F0.imprint","IMPRINT",FACE,{"disambiguationData":[TD([[makeQuery(id+"F0.imprint","IMPRINT",EDGE,{"disambiguationData":[TD([[subQ2,-1.0]])],"derivedFrom":subQ1}),1.0]])]});}
            var Q170;
            {var subQ0=sQuery(id+"F0.wireOp",EDGE,"E34");var subQ1=sQuery(id+"F0.wireOp",EDGE,"E11");var subQ2=makeQuery(id+"F0.imprint","INTERSECT",VERTEX,{"derivedFrom":[subQ1,subQ0]});Q170=makeQuery(id+"F0.imprint","IMPRINT",FACE,{"disambiguationData":[TD([[makeQuery(id+"F0.imprint","IMPRINT",EDGE,{"disambiguationData":[TD([[subQ2,-1.0]])],"derivedFrom":subQ1}),1.0]])]});}
            var Q171;
            {var subQ0=sQuery(id+"F0.wireOp",EDGE,"E11");var subQ1=sQuery(id+"F0.wireOp",EDGE,"E0.bottom");var subQ2=makeQuery(id+"F0.imprint","INTERSECT",VERTEX,{"derivedFrom":[subQ1,subQ0]});Q171=makeQuery(id+"F0.imprint","IMPRINT",FACE,{"disambiguationData":[TD([[makeQuery(id+"F0.imprint","IMPRINT",EDGE,{"disambiguationData":[TD([[subQ2,-1.0]])],"derivedFrom":subQ1}),-1.0]])]});}
            var Q172;
            {var subQ0=sQuery(id+"F0.wireOp",EDGE,"E23");var subQ1=sQuery(id+"F0.wireOp",EDGE,"E0.left");var subQ2=makeQuery(id+"F0.imprint","INTERSECT",VERTEX,{"derivedFrom":[subQ1,subQ0]});Q172=makeQuery(id+"F0.imprint","IMPRINT",FACE,{"disambiguationData":[TD([[makeQuery(id+"F0.imprint","IMPRINT",EDGE,{"disambiguationData":[TD([[subQ2,-1.0]])],"derivedFrom":subQ1}),1.0]])]});}
            var Q173;
            {var subQ0=sQuery(id+"F0.wireOp",EDGE,"E26");var subQ1=sQuery(id+"F0.wireOp",EDGE,"E0.left");var subQ2=makeQuery(id+"F0.imprint","INTERSECT",VERTEX,{"derivedFrom":[subQ1,subQ0]});Q173=makeQuery(id+"F0.imprint","IMPRINT",FACE,{"disambiguationData":[TD([[makeQuery(id+"F0.imprint","IMPRINT",EDGE,{"disambiguationData":[TD([[subQ2,-1.0]])],"derivedFrom":subQ1}),1.0]])]});}
            var Q174;
            {var subQ0=sQuery(id+"F0.wireOp",EDGE,"E24");var subQ1=sQuery(id+"F0.wireOp",EDGE,"E0.left");var subQ2=makeQuery(id+"F0.imprint","INTERSECT",VERTEX,{"derivedFrom":[subQ1,subQ0]});Q174=makeQuery(id+"F0.imprint","IMPRINT",FACE,{"disambiguationData":[TD([[makeQuery(id+"F0.imprint","IMPRINT",EDGE,{"disambiguationData":[TD([[subQ2,-1.0]])],"derivedFrom":subQ1}),1.0]])]});}
            var Q175;
            {var subQ0=sQuery(id+"F0.wireOp",EDGE,"E31");var subQ1=sQuery(id+"F0.wireOp",EDGE,"E0.left");var subQ2=makeQuery(id+"F0.imprint","INTERSECT",VERTEX,{"derivedFrom":[subQ1,subQ0]});Q175=makeQuery(id+"F0.imprint","IMPRINT",FACE,{"disambiguationData":[TD([[makeQuery(id+"F0.imprint","IMPRINT",EDGE,{"disambiguationData":[TD([[subQ2,-1.0]])],"derivedFrom":subQ1}),1.0]])]});}
            var Q176;
            {var subQ0=sQuery(id+"F0.wireOp",EDGE,"E20");var subQ1=sQuery(id+"F0.wireOp",EDGE,"E0.right");var subQ2=makeQuery(id+"F0.imprint","INTERSECT",VERTEX,{"derivedFrom":[subQ1,subQ0]});Q176=makeQuery(id+"F0.imprint","IMPRINT",FACE,{"disambiguationData":[TD([[makeQuery(id+"F0.imprint","IMPRINT",EDGE,{"disambiguationData":[TD([[subQ2,-1.0]])],"derivedFrom":subQ1}),-1.0]])]});}
            var Q177;
            {var subQ0=sQuery(id+"F0.wireOp",EDGE,"E8");var subQ1=sQuery(id+"F0.wireOp",EDGE,"E0.bottom");var subQ2=makeQuery(id+"F0.imprint","INTERSECT",VERTEX,{"derivedFrom":[subQ1,subQ0]});Q177=makeQuery(id+"F0.imprint","IMPRINT",FACE,{"disambiguationData":[TD([[makeQuery(id+"F0.imprint","IMPRINT",EDGE,{"disambiguationData":[TD([[subQ2,-1.0]])],"derivedFrom":subQ1}),-1.0]])]});}
            var Q178;
            {var subQ0=sQuery(id+"F0.wireOp",EDGE,"E30");var subQ1=sQuery(id+"F0.wireOp",EDGE,"E0.right");var subQ2=makeQuery(id+"F0.imprint","INTERSECT",VERTEX,{"derivedFrom":[subQ1,subQ0]});Q178=makeQuery(id+"F0.imprint","IMPRINT",FACE,{"disambiguationData":[TD([[makeQuery(id+"F0.imprint","IMPRINT",EDGE,{"disambiguationData":[TD([[subQ2,-1.0]])],"derivedFrom":subQ1}),-1.0]])]});}
            var Q179;
            {var subQ0=sQuery(id+"F0.wireOp",EDGE,"E20");var subQ1=sQuery(id+"F0.wireOp",EDGE,"E9");var subQ2=makeQuery(id+"F0.imprint","INTERSECT",VERTEX,{"derivedFrom":[subQ1,subQ0]});Q179=makeQuery(id+"F0.imprint","IMPRINT",FACE,{"disambiguationData":[TD([[makeQuery(id+"F0.imprint","IMPRINT",EDGE,{"disambiguationData":[TD([[subQ2,-1.0]])],"derivedFrom":subQ1}),1.0]])]});}
            var Q180;
            {var subQ0=sQuery(id+"F0.wireOp",EDGE,"E20");var subQ1=sQuery(id+"F0.wireOp",EDGE,"E4");var subQ2=makeQuery(id+"F0.imprint","INTERSECT",VERTEX,{"derivedFrom":[subQ1,subQ0]});Q180=makeQuery(id+"F0.imprint","IMPRINT",FACE,{"disambiguationData":[TD([[makeQuery(id+"F0.imprint","IMPRINT",EDGE,{"disambiguationData":[TD([[subQ2,-1.0]])],"derivedFrom":subQ1}),1.0]])]});}
            var Q181;
            {var subQ0=sQuery(id+"F0.wireOp",EDGE,"E19");var subQ1=sQuery(id+"F0.wireOp",EDGE,"E0.left");var subQ2=makeQuery(id+"F0.imprint","INTERSECT",VERTEX,{"derivedFrom":[subQ1,subQ0]});Q181=makeQuery(id+"F0.imprint","IMPRINT",FACE,{"disambiguationData":[TD([[makeQuery(id+"F0.imprint","IMPRINT",EDGE,{"disambiguationData":[TD([[subQ2,-1.0]])],"derivedFrom":subQ1}),1.0]])]});}
            var Q182;
            {var subQ0=sQuery(id+"F0.wireOp",EDGE,"E22");var subQ1=sQuery(id+"F0.wireOp",EDGE,"E0.left");var subQ2=makeQuery(id+"F0.imprint","INTERSECT",VERTEX,{"derivedFrom":[subQ1,subQ0]});Q182=makeQuery(id+"F0.imprint","IMPRINT",FACE,{"disambiguationData":[TD([[makeQuery(id+"F0.imprint","IMPRINT",EDGE,{"disambiguationData":[TD([[subQ2,-1.0]])],"derivedFrom":subQ1}),1.0]])]});}
            var Q183;
            {var subQ0=sQuery(id+"F0.wireOp",EDGE,"E34");var subQ1=sQuery(id+"F0.wireOp",EDGE,"E0.left");var subQ2=makeQuery(id+"F0.imprint","INTERSECT",VERTEX,{"derivedFrom":[subQ1,subQ0]});Q183=makeQuery(id+"F0.imprint","IMPRINT",FACE,{"disambiguationData":[TD([[makeQuery(id+"F0.imprint","IMPRINT",EDGE,{"disambiguationData":[TD([[subQ2,-1.0]])],"derivedFrom":subQ1}),1.0]])]});}
            var Q184;
            {var subQ0=sQuery(id+"F0.wireOp",EDGE,"E34");var subQ1=sQuery(id+"F0.wireOp",EDGE,"E10");var subQ2=makeQuery(id+"F0.imprint","INTERSECT",VERTEX,{"derivedFrom":[subQ1,subQ0]});Q184=makeQuery(id+"F0.imprint","IMPRINT",FACE,{"disambiguationData":[TD([[makeQuery(id+"F0.imprint","IMPRINT",EDGE,{"disambiguationData":[TD([[subQ2,-1.0]])],"derivedFrom":subQ1}),1.0]])]});}
            var Q185;
            {var subQ0=sQuery(id+"F0.wireOp",EDGE,"E20");var subQ1=sQuery(id+"F0.wireOp",EDGE,"E8");var subQ2=makeQuery(id+"F0.imprint","INTERSECT",VERTEX,{"derivedFrom":[subQ1,subQ0]});Q185=makeQuery(id+"F0.imprint","IMPRINT",FACE,{"disambiguationData":[TD([[makeQuery(id+"F0.imprint","IMPRINT",EDGE,{"disambiguationData":[TD([[subQ2,-1.0]])],"derivedFrom":subQ1}),1.0]])]});}
            var Q186;
            {var subQ0=sQuery(id+"F0.wireOp",EDGE,"E25");var subQ1=sQuery(id+"F0.wireOp",EDGE,"E0.left");var subQ2=makeQuery(id+"F0.imprint","INTERSECT",VERTEX,{"derivedFrom":[subQ1,subQ0]});Q186=makeQuery(id+"F0.imprint","IMPRINT",FACE,{"disambiguationData":[TD([[makeQuery(id+"F0.imprint","IMPRINT",EDGE,{"disambiguationData":[TD([[subQ2,-1.0]])],"derivedFrom":subQ1}),1.0]])]});}
            var Q187;
            {var subQ0=sQuery(id+"F0.wireOp",EDGE,"E26");var subQ1=sQuery(id+"F0.wireOp",EDGE,"E0.right");var subQ2=makeQuery(id+"F0.imprint","INTERSECT",VERTEX,{"derivedFrom":[subQ1,subQ0]});Q187=makeQuery(id+"F0.imprint","IMPRINT",FACE,{"disambiguationData":[TD([[makeQuery(id+"F0.imprint","IMPRINT",EDGE,{"disambiguationData":[TD([[subQ2,-1.0]])],"derivedFrom":subQ1}),-1.0]])]});}
            var Q188;
            {var subQ0=sQuery(id+"F0.wireOp",EDGE,"E20");var subQ1=sQuery(id+"F0.wireOp",EDGE,"E11");var subQ2=makeQuery(id+"F0.imprint","INTERSECT",VERTEX,{"derivedFrom":[subQ1,subQ0]});Q188=makeQuery(id+"F0.imprint","IMPRINT",FACE,{"disambiguationData":[TD([[makeQuery(id+"F0.imprint","IMPRINT",EDGE,{"disambiguationData":[TD([[subQ2,-1.0]])],"derivedFrom":subQ1}),1.0]])]});}
            var Q189;
            {var subQ0=sQuery(id+"F0.wireOp",EDGE,"E34");var subQ1=sQuery(id+"F0.wireOp",EDGE,"E12");var subQ2=makeQuery(id+"F0.imprint","INTERSECT",VERTEX,{"derivedFrom":[subQ1,subQ0]});Q189=makeQuery(id+"F0.imprint","IMPRINT",FACE,{"disambiguationData":[TD([[makeQuery(id+"F0.imprint","IMPRINT",EDGE,{"disambiguationData":[TD([[subQ2,-1.0]])],"derivedFrom":subQ1}),1.0]])]});}
            var Q190;
            {var subQ0=sQuery(id+"F0.wireOp",EDGE,"E1");var subQ1=sQuery(id+"F0.wireOp",EDGE,"E0.top");var subQ2=makeQuery(id+"F0.imprint","INTERSECT",VERTEX,{"derivedFrom":[subQ1,subQ0]});Q190=makeQuery(id+"F0.imprint","IMPRINT",FACE,{"disambiguationData":[TD([[makeQuery(id+"F0.imprint","IMPRINT",EDGE,{"disambiguationData":[TD([[subQ2,-1.0]])],"derivedFrom":subQ1}),1.0]])]});}
            var Q191;
            {var subQ0=sQuery(id+"F0.wireOp",EDGE,"E8");var subQ1=sQuery(id+"F0.wireOp",EDGE,"E0.top");var subQ2=makeQuery(id+"F0.imprint","INTERSECT",VERTEX,{"derivedFrom":[subQ1,subQ0]});Q191=makeQuery(id+"F0.imprint","IMPRINT",FACE,{"disambiguationData":[TD([[makeQuery(id+"F0.imprint","IMPRINT",EDGE,{"disambiguationData":[TD([[subQ2,-1.0]])],"derivedFrom":subQ1}),1.0]])]});}
            var Q192;
            {var subQ0=sQuery(id+"F0.wireOp",EDGE,"E34");var subQ1=sQuery(id+"F0.wireOp",EDGE,"E8");var subQ2=makeQuery(id+"F0.imprint","INTERSECT",VERTEX,{"derivedFrom":[subQ1,subQ0]});Q192=makeQuery(id+"F0.imprint","IMPRINT",FACE,{"disambiguationData":[TD([[makeQuery(id+"F0.imprint","IMPRINT",EDGE,{"disambiguationData":[TD([[subQ2,-1.0]])],"derivedFrom":subQ1}),1.0]])]});}
            var Q193;
            {var subQ0=sQuery(id+"F0.wireOp",EDGE,"E29");var subQ1=sQuery(id+"F0.wireOp",EDGE,"E0.right");var subQ2=makeQuery(id+"F0.imprint","INTERSECT",VERTEX,{"derivedFrom":[subQ1,subQ0]});Q193=makeQuery(id+"F0.imprint","IMPRINT",FACE,{"disambiguationData":[TD([[makeQuery(id+"F0.imprint","IMPRINT",EDGE,{"disambiguationData":[TD([[subQ2,-1.0]])],"derivedFrom":subQ1}),-1.0]])]});}
            var Q194;
            {var subQ0=sQuery(id+"F0.wireOp",EDGE,"E28");var subQ1=sQuery(id+"F0.wireOp",EDGE,"E17");var subQ2=makeQuery(id+"F0.imprint","INTERSECT",VERTEX,{"derivedFrom":[subQ1,subQ0]});Q194=makeQuery(id+"F0.imprint","IMPRINT",FACE,{"disambiguationData":[TD([[makeQuery(id+"F0.imprint","IMPRINT",EDGE,{"disambiguationData":[TD([[subQ2,-1.0]])],"derivedFrom":subQ1}),1.0]])]});}
            var Q195;
            {var subQ0=sQuery(id+"F0.wireOp",EDGE,"E34");var subQ1=sQuery(id+"F0.wireOp",EDGE,"E2");var subQ2=makeQuery(id+"F0.imprint","INTERSECT",VERTEX,{"derivedFrom":[subQ1,subQ0]});Q195=makeQuery(id+"F0.imprint","IMPRINT",FACE,{"disambiguationData":[TD([[makeQuery(id+"F0.imprint","IMPRINT",EDGE,{"disambiguationData":[TD([[subQ2,-1.0]])],"derivedFrom":subQ1}),1.0]])]});}
            var Q196;
            {var subQ0=sQuery(id+"F0.wireOp",EDGE,"E15");var subQ1=sQuery(id+"F0.wireOp",EDGE,"E0.bottom");var subQ2=makeQuery(id+"F0.imprint","INTERSECT",VERTEX,{"derivedFrom":[subQ1,subQ0]});Q196=makeQuery(id+"F0.imprint","IMPRINT",FACE,{"disambiguationData":[TD([[makeQuery(id+"F0.imprint","IMPRINT",EDGE,{"disambiguationData":[TD([[subQ2,-1.0]])],"derivedFrom":subQ1}),-1.0]])]});}
            var Q197;
            {var subQ0=sQuery(id+"F0.wireOp",EDGE,"E28");var subQ1=sQuery(id+"F0.wireOp",EDGE,"E9");var subQ2=makeQuery(id+"F0.imprint","INTERSECT",VERTEX,{"derivedFrom":[subQ1,subQ0]});Q197=makeQuery(id+"F0.imprint","IMPRINT",FACE,{"disambiguationData":[TD([[makeQuery(id+"F0.imprint","IMPRINT",EDGE,{"disambiguationData":[TD([[subQ2,-1.0]])],"derivedFrom":subQ1}),1.0]])]});}
            var Q198;
            {var subQ0=sQuery(id+"F0.wireOp",EDGE,"E5");var subQ1=sQuery(id+"F0.wireOp",EDGE,"E0.bottom");var subQ2=makeQuery(id+"F0.imprint","INTERSECT",VERTEX,{"derivedFrom":[subQ1,subQ0]});Q198=makeQuery(id+"F0.imprint","IMPRINT",FACE,{"disambiguationData":[TD([[makeQuery(id+"F0.imprint","IMPRINT",EDGE,{"disambiguationData":[TD([[subQ2,-1.0]])],"derivedFrom":subQ1}),-1.0]])]});}
            var Q199;
            {var subQ0=sQuery(id+"F0.wireOp",EDGE,"E2");var subQ1=sQuery(id+"F0.wireOp",EDGE,"E0.bottom");var subQ2=makeQuery(id+"F0.imprint","INTERSECT",VERTEX,{"derivedFrom":[subQ1,subQ0]});Q199=makeQuery(id+"F0.imprint","IMPRINT",FACE,{"disambiguationData":[TD([[makeQuery(id+"F0.imprint","IMPRINT",EDGE,{"disambiguationData":[TD([[subQ2,-1.0]])],"derivedFrom":subQ1}),-1.0]])]});}
            var Q200;
            {var subQ0=sQuery(id+"F0.wireOp",EDGE,"E34");var subQ1=sQuery(id+"F0.wireOp",EDGE,"E14");var subQ2=makeQuery(id+"F0.imprint","INTERSECT",VERTEX,{"derivedFrom":[subQ1,subQ0]});Q200=makeQuery(id+"F0.imprint","IMPRINT",FACE,{"disambiguationData":[TD([[makeQuery(id+"F0.imprint","IMPRINT",EDGE,{"disambiguationData":[TD([[subQ2,-1.0]])],"derivedFrom":subQ1}),1.0]])]});}
            var Q201;
            {var subQ0=sQuery(id+"F0.wireOp",EDGE,"E3");var subQ1=sQuery(id+"F0.wireOp",EDGE,"E0.bottom");var subQ2=makeQuery(id+"F0.imprint","INTERSECT",VERTEX,{"derivedFrom":[subQ1,subQ0]});Q201=makeQuery(id+"F0.imprint","IMPRINT",FACE,{"disambiguationData":[TD([[makeQuery(id+"F0.imprint","IMPRINT",EDGE,{"disambiguationData":[TD([[subQ2,-1.0]])],"derivedFrom":subQ1}),-1.0]])]});}
            var Q202;
            {var subQ0=sQuery(id+"F0.wireOp",EDGE,"E28");var subQ1=sQuery(id+"F0.wireOp",EDGE,"E7");var subQ2=makeQuery(id+"F0.imprint","INTERSECT",VERTEX,{"derivedFrom":[subQ1,subQ0]});Q202=makeQuery(id+"F0.imprint","IMPRINT",FACE,{"disambiguationData":[TD([[makeQuery(id+"F0.imprint","IMPRINT",EDGE,{"disambiguationData":[TD([[subQ2,-1.0]])],"derivedFrom":subQ1}),1.0]])]});}
            var Q203;
            {var subQ0=sQuery(id+"F0.wireOp",EDGE,"E34");var subQ1=sQuery(id+"F0.wireOp",EDGE,"E9");var subQ2=makeQuery(id+"F0.imprint","INTERSECT",VERTEX,{"derivedFrom":[subQ1,subQ0]});Q203=makeQuery(id+"F0.imprint","IMPRINT",FACE,{"disambiguationData":[TD([[makeQuery(id+"F0.imprint","IMPRINT",EDGE,{"disambiguationData":[TD([[subQ2,-1.0]])],"derivedFrom":subQ1}),1.0]])]});}
            var Q204;
            {var subQ0=sQuery(id+"F0.wireOp",EDGE,"E13");var subQ1=sQuery(id+"F0.wireOp",EDGE,"E0.top");var subQ2=makeQuery(id+"F0.imprint","INTERSECT",VERTEX,{"derivedFrom":[subQ1,subQ0]});Q204=makeQuery(id+"F0.imprint","IMPRINT",FACE,{"disambiguationData":[TD([[makeQuery(id+"F0.imprint","IMPRINT",EDGE,{"disambiguationData":[TD([[subQ2,-1.0]])],"derivedFrom":subQ1}),1.0]])]});}
            var Q205;
            {var subQ0=sQuery(id+"F0.wireOp",EDGE,"E28");var subQ1=sQuery(id+"F0.wireOp",EDGE,"E0.left");var subQ2=makeQuery(id+"F0.imprint","INTERSECT",VERTEX,{"derivedFrom":[subQ1,subQ0]});Q205=makeQuery(id+"F0.imprint","IMPRINT",FACE,{"disambiguationData":[TD([[makeQuery(id+"F0.imprint","IMPRINT",EDGE,{"disambiguationData":[TD([[subQ2,-1.0]])],"derivedFrom":subQ1}),1.0]])]});}
            var Q206;
            {var subQ0=sQuery(id+"F0.wireOp",EDGE,"E29");var subQ1=sQuery(id+"F0.wireOp",EDGE,"E4");var subQ2=makeQuery(id+"F0.imprint","INTERSECT",VERTEX,{"derivedFrom":[subQ1,subQ0]});Q206=makeQuery(id+"F0.imprint","IMPRINT",FACE,{"disambiguationData":[TD([[makeQuery(id+"F0.imprint","IMPRINT",EDGE,{"disambiguationData":[TD([[subQ2,-1.0]])],"derivedFrom":subQ1}),1.0]])]});}
            var Q207;
            {var subQ0=sQuery(id+"F0.wireOp",EDGE,"E20");var subQ1=sQuery(id+"F0.wireOp",EDGE,"E2");var subQ2=makeQuery(id+"F0.imprint","INTERSECT",VERTEX,{"derivedFrom":[subQ1,subQ0]});Q207=makeQuery(id+"F0.imprint","IMPRINT",FACE,{"disambiguationData":[TD([[makeQuery(id+"F0.imprint","IMPRINT",EDGE,{"disambiguationData":[TD([[subQ2,-1.0]])],"derivedFrom":subQ1}),1.0]])]});}
            var Q208;
            {var subQ0=sQuery(id+"F0.wireOp",EDGE,"E27");var subQ1=sQuery(id+"F0.wireOp",EDGE,"E4");var subQ2=makeQuery(id+"F0.imprint","INTERSECT",VERTEX,{"derivedFrom":[subQ1,subQ0]});Q208=makeQuery(id+"F0.imprint","IMPRINT",FACE,{"disambiguationData":[TD([[makeQuery(id+"F0.imprint","IMPRINT",EDGE,{"disambiguationData":[TD([[subQ2,-1.0]])],"derivedFrom":subQ1}),1.0]])]});}
            var Q209;
            {var subQ0=sQuery(id+"F0.wireOp",EDGE,"E10");var subQ1=sQuery(id+"F0.wireOp",EDGE,"E0.top");var subQ2=makeQuery(id+"F0.imprint","INTERSECT",VERTEX,{"derivedFrom":[subQ1,subQ0]});Q209=makeQuery(id+"F0.imprint","IMPRINT",FACE,{"disambiguationData":[TD([[makeQuery(id+"F0.imprint","IMPRINT",EDGE,{"disambiguationData":[TD([[subQ2,-1.0]])],"derivedFrom":subQ1}),1.0]])]});}
            var Q210;
            {var subQ0=sQuery(id+"F0.wireOp",EDGE,"E21");var subQ1=sQuery(id+"F0.wireOp",EDGE,"E0.left");var subQ2=makeQuery(id+"F0.imprint","INTERSECT",VERTEX,{"derivedFrom":[subQ1,subQ0]});Q210=makeQuery(id+"F0.imprint","IMPRINT",FACE,{"disambiguationData":[TD([[makeQuery(id+"F0.imprint","IMPRINT",EDGE,{"disambiguationData":[TD([[subQ2,-1.0]])],"derivedFrom":subQ1}),1.0]])]});}
            var Q211;
            {var subQ0=sQuery(id+"F0.wireOp",EDGE,"E28");var subQ1=sQuery(id+"F0.wireOp",EDGE,"E15");var subQ2=makeQuery(id+"F0.imprint","INTERSECT",VERTEX,{"derivedFrom":[subQ1,subQ0]});Q211=makeQuery(id+"F0.imprint","IMPRINT",FACE,{"disambiguationData":[TD([[makeQuery(id+"F0.imprint","IMPRINT",EDGE,{"disambiguationData":[TD([[subQ2,-1.0]])],"derivedFrom":subQ1}),1.0]])]});}
            var Q212;
            {var subQ0=sQuery(id+"F0.wireOp",EDGE,"E9");var subQ1=sQuery(id+"F0.wireOp",EDGE,"E0.top");var subQ2=makeQuery(id+"F0.imprint","INTERSECT",VERTEX,{"derivedFrom":[subQ1,subQ0]});Q212=makeQuery(id+"F0.imprint","IMPRINT",FACE,{"disambiguationData":[TD([[makeQuery(id+"F0.imprint","IMPRINT",EDGE,{"disambiguationData":[TD([[subQ2,-1.0]])],"derivedFrom":subQ1}),1.0]])]});}
            var Q213;
            {var subQ0=sQuery(id+"F0.wireOp",EDGE,"E34");var subQ1=sQuery(id+"F0.wireOp",EDGE,"E13");var subQ2=makeQuery(id+"F0.imprint","INTERSECT",VERTEX,{"derivedFrom":[subQ1,subQ0]});Q213=makeQuery(id+"F0.imprint","IMPRINT",FACE,{"disambiguationData":[TD([[makeQuery(id+"F0.imprint","IMPRINT",EDGE,{"disambiguationData":[TD([[subQ2,-1.0]])],"derivedFrom":subQ1}),1.0]])]});}
            var Q214;
            {var subQ0=sQuery(id+"F0.wireOp",EDGE,"E29");var subQ1=sQuery(id+"F0.wireOp",EDGE,"E0.left");var subQ2=makeQuery(id+"F0.imprint","INTERSECT",VERTEX,{"derivedFrom":[subQ1,subQ0]});Q214=makeQuery(id+"F0.imprint","IMPRINT",FACE,{"disambiguationData":[TD([[makeQuery(id+"F0.imprint","IMPRINT",EDGE,{"disambiguationData":[TD([[subQ2,-1.0]])],"derivedFrom":subQ1}),1.0]])]});}
            var Q215;
            {var subQ0=sQuery(id+"F0.wireOp",EDGE,"E31");var subQ1=sQuery(id+"F0.wireOp",EDGE,"E0.right");var subQ2=makeQuery(id+"F0.imprint","INTERSECT",VERTEX,{"derivedFrom":[subQ1,subQ0]});Q215=makeQuery(id+"F0.imprint","IMPRINT",FACE,{"disambiguationData":[TD([[makeQuery(id+"F0.imprint","IMPRINT",EDGE,{"disambiguationData":[TD([[subQ2,-1.0]])],"derivedFrom":subQ1}),-1.0]])]});}
            var Q216;
            {var subQ0=sQuery(id+"F0.wireOp",EDGE,"E11");var subQ1=sQuery(id+"F0.wireOp",EDGE,"E0.top");var subQ2=makeQuery(id+"F0.imprint","INTERSECT",VERTEX,{"derivedFrom":[subQ1,subQ0]});Q216=makeQuery(id+"F0.imprint","IMPRINT",FACE,{"disambiguationData":[TD([[makeQuery(id+"F0.imprint","IMPRINT",EDGE,{"disambiguationData":[TD([[subQ2,-1.0]])],"derivedFrom":subQ1}),1.0]])]});}
            var Q217;
            {var subQ0=sQuery(id+"F0.wireOp",EDGE,"E4");var subQ1=sQuery(id+"F0.wireOp",EDGE,"E0.top");var subQ2=makeQuery(id+"F0.imprint","INTERSECT",VERTEX,{"derivedFrom":[subQ1,subQ0]});Q217=makeQuery(id+"F0.imprint","IMPRINT",FACE,{"disambiguationData":[TD([[makeQuery(id+"F0.imprint","IMPRINT",EDGE,{"disambiguationData":[TD([[subQ2,-1.0]])],"derivedFrom":subQ1}),1.0]])]});}
            var Q218;
            {var subQ0=sQuery(id+"F0.wireOp",EDGE,"E12");var subQ1=sQuery(id+"F0.wireOp",EDGE,"E0.top");var subQ2=makeQuery(id+"F0.imprint","INTERSECT",VERTEX,{"derivedFrom":[subQ1,subQ0]});Q218=makeQuery(id+"F0.imprint","IMPRINT",FACE,{"disambiguationData":[TD([[makeQuery(id+"F0.imprint","IMPRINT",EDGE,{"disambiguationData":[TD([[subQ2,-1.0]])],"derivedFrom":subQ1}),1.0]])]});}
            var Q219;
            {var subQ0=sQuery(id+"F0.wireOp",EDGE,"E28");var subQ1=sQuery(id+"F0.wireOp",EDGE,"E8");var subQ2=makeQuery(id+"F0.imprint","INTERSECT",VERTEX,{"derivedFrom":[subQ1,subQ0]});Q219=makeQuery(id+"F0.imprint","IMPRINT",FACE,{"disambiguationData":[TD([[makeQuery(id+"F0.imprint","IMPRINT",EDGE,{"disambiguationData":[TD([[subQ2,-1.0]])],"derivedFrom":subQ1}),1.0]])]});}
            var Q220;
            {var subQ0=sQuery(id+"F0.wireOp",EDGE,"E20");var subQ1=sQuery(id+"F0.wireOp",EDGE,"E7");var subQ2=makeQuery(id+"F0.imprint","INTERSECT",VERTEX,{"derivedFrom":[subQ1,subQ0]});Q220=makeQuery(id+"F0.imprint","IMPRINT",FACE,{"disambiguationData":[TD([[makeQuery(id+"F0.imprint","IMPRINT",EDGE,{"disambiguationData":[TD([[subQ2,-1.0]])],"derivedFrom":subQ1}),1.0]])]});}
            var Q221;
            {var subQ0=sQuery(id+"F0.wireOp",EDGE,"E2");var subQ1=sQuery(id+"F0.wireOp",EDGE,"E0.top");var subQ2=makeQuery(id+"F0.imprint","INTERSECT",VERTEX,{"derivedFrom":[subQ1,subQ0]});Q221=makeQuery(id+"F0.imprint","IMPRINT",FACE,{"disambiguationData":[TD([[makeQuery(id+"F0.imprint","IMPRINT",EDGE,{"disambiguationData":[TD([[subQ2,-1.0]])],"derivedFrom":subQ1}),1.0]])]});}
            var Q222;
            {var subQ0=sQuery(id+"F0.wireOp",EDGE,"E28");var subQ1=sQuery(id+"F0.wireOp",EDGE,"E2");var subQ2=makeQuery(id+"F0.imprint","INTERSECT",VERTEX,{"derivedFrom":[subQ1,subQ0]});Q222=makeQuery(id+"F0.imprint","IMPRINT",FACE,{"disambiguationData":[TD([[makeQuery(id+"F0.imprint","IMPRINT",EDGE,{"disambiguationData":[TD([[subQ2,-1.0]])],"derivedFrom":subQ1}),1.0]])]});}
            var Q223;
            {var subQ0=sQuery(id+"F0.wireOp",EDGE,"E28");var subQ1=sQuery(id+"F0.wireOp",EDGE,"E5");var subQ2=makeQuery(id+"F0.imprint","INTERSECT",VERTEX,{"derivedFrom":[subQ1,subQ0]});Q223=makeQuery(id+"F0.imprint","IMPRINT",FACE,{"disambiguationData":[TD([[makeQuery(id+"F0.imprint","IMPRINT",EDGE,{"disambiguationData":[TD([[subQ2,-1.0]])],"derivedFrom":subQ1}),1.0]])]});}
            var Q224;
            {var subQ0=sQuery(id+"F0.wireOp",EDGE,"E34");var subQ1=sQuery(id+"F0.wireOp",EDGE,"E6");var subQ2=makeQuery(id+"F0.imprint","INTERSECT",VERTEX,{"derivedFrom":[subQ1,subQ0]});Q224=makeQuery(id+"F0.imprint","IMPRINT",FACE,{"disambiguationData":[TD([[makeQuery(id+"F0.imprint","IMPRINT",EDGE,{"disambiguationData":[TD([[subQ2,-1.0]])],"derivedFrom":subQ1}),1.0]])]});}
            var Q225;
            {var subQ0=sQuery(id+"F0.wireOp",EDGE,"E17");var subQ1=sQuery(id+"F0.wireOp",EDGE,"E0.top");var subQ2=makeQuery(id+"F0.imprint","INTERSECT",VERTEX,{"derivedFrom":[subQ1,subQ0]});Q225=makeQuery(id+"F0.imprint","IMPRINT",FACE,{"disambiguationData":[TD([[makeQuery(id+"F0.imprint","IMPRINT",EDGE,{"disambiguationData":[TD([[subQ2,-1.0]])],"derivedFrom":subQ1}),1.0]])]});}
            var Q226;
            {var subQ0=sQuery(id+"F0.wireOp",EDGE,"E21");var subQ1=sQuery(id+"F0.wireOp",EDGE,"E4");var subQ2=makeQuery(id+"F0.imprint","INTERSECT",VERTEX,{"derivedFrom":[subQ1,subQ0]});Q226=makeQuery(id+"F0.imprint","IMPRINT",FACE,{"disambiguationData":[TD([[makeQuery(id+"F0.imprint","IMPRINT",EDGE,{"disambiguationData":[TD([[subQ2,-1.0]])],"derivedFrom":subQ1}),1.0]])]});}
            var Q227;
            {var subQ0=sQuery(id+"F0.wireOp",EDGE,"E19");var subQ1=sQuery(id+"F0.wireOp",EDGE,"E0.right");var subQ2=makeQuery(id+"F0.imprint","INTERSECT",VERTEX,{"derivedFrom":[subQ1,subQ0]});Q227=makeQuery(id+"F0.imprint","IMPRINT",FACE,{"disambiguationData":[TD([[makeQuery(id+"F0.imprint","IMPRINT",EDGE,{"disambiguationData":[TD([[subQ2,-1.0]])],"derivedFrom":subQ1}),-1.0]])]});}
            var Q228;
            {var subQ0=sQuery(id+"F0.wireOp",EDGE,"E5");var subQ1=sQuery(id+"F0.wireOp",EDGE,"E0.top");var subQ2=makeQuery(id+"F0.imprint","INTERSECT",VERTEX,{"derivedFrom":[subQ1,subQ0]});Q228=makeQuery(id+"F0.imprint","IMPRINT",FACE,{"disambiguationData":[TD([[makeQuery(id+"F0.imprint","IMPRINT",EDGE,{"disambiguationData":[TD([[subQ2,-1.0]])],"derivedFrom":subQ1}),1.0]])]});}
            var Q229;
            {var subQ0=sQuery(id+"F0.wireOp",EDGE,"E1");var subQ1=sQuery(id+"F0.wireOp",EDGE,"E0.bottom");var subQ2=makeQuery(id+"F0.imprint","INTERSECT",VERTEX,{"derivedFrom":[subQ1,subQ0]});Q229=makeQuery(id+"F0.imprint","IMPRINT",FACE,{"disambiguationData":[TD([[makeQuery(id+"F0.imprint","IMPRINT",EDGE,{"disambiguationData":[TD([[subQ2,-1.0]])],"derivedFrom":subQ1}),-1.0]])]});}
            var Q230;
            {var subQ0=sQuery(id+"F0.wireOp",EDGE,"E33");var subQ1=sQuery(id+"F0.wireOp",EDGE,"E4");var subQ2=makeQuery(id+"F0.imprint","INTERSECT",VERTEX,{"derivedFrom":[subQ1,subQ0]});Q230=makeQuery(id+"F0.imprint","IMPRINT",FACE,{"disambiguationData":[TD([[makeQuery(id+"F0.imprint","IMPRINT",EDGE,{"disambiguationData":[TD([[subQ2,-1.0]])],"derivedFrom":subQ1}),1.0]])]});}
            var Q231;
            {var subQ0=sQuery(id+"F0.wireOp",EDGE,"E19");var subQ1=sQuery(id+"F0.wireOp",EDGE,"E4");var subQ2=makeQuery(id+"F0.imprint","INTERSECT",VERTEX,{"derivedFrom":[subQ1,subQ0]});Q231=makeQuery(id+"F0.imprint","IMPRINT",FACE,{"disambiguationData":[TD([[makeQuery(id+"F0.imprint","IMPRINT",EDGE,{"disambiguationData":[TD([[subQ2,-1.0]])],"derivedFrom":subQ1}),1.0]])]});}
            var Q232;
            {var subQ0=sQuery(id+"F0.wireOp",EDGE,"E3");var subQ1=sQuery(id+"F0.wireOp",EDGE,"E0.top");var subQ2=makeQuery(id+"F0.imprint","INTERSECT",VERTEX,{"derivedFrom":[subQ1,subQ0]});Q232=makeQuery(id+"F0.imprint","IMPRINT",FACE,{"disambiguationData":[TD([[makeQuery(id+"F0.imprint","IMPRINT",EDGE,{"disambiguationData":[TD([[subQ2,-1.0]])],"derivedFrom":subQ1}),1.0]])]});}
            var Q233;
            {var subQ0=sQuery(id+"F0.wireOp",EDGE,"E28");var subQ1=sQuery(id+"F0.wireOp",EDGE,"E0.right");var subQ2=makeQuery(id+"F0.imprint","INTERSECT",VERTEX,{"derivedFrom":[subQ1,subQ0]});Q233=makeQuery(id+"F0.imprint","IMPRINT",FACE,{"disambiguationData":[TD([[makeQuery(id+"F0.imprint","IMPRINT",EDGE,{"disambiguationData":[TD([[subQ2,-1.0]])],"derivedFrom":subQ1}),-1.0]])]});}
            var Q234;
            {var subQ0=sQuery(id+"F0.wireOp",EDGE,"E32");var subQ1=sQuery(id+"F0.wireOp",EDGE,"E0.right");var subQ2=makeQuery(id+"F0.imprint","INTERSECT",VERTEX,{"derivedFrom":[subQ1,subQ0]});Q234=makeQuery(id+"F0.imprint","IMPRINT",FACE,{"disambiguationData":[TD([[makeQuery(id+"F0.imprint","IMPRINT",EDGE,{"disambiguationData":[TD([[subQ2,-1.0]])],"derivedFrom":subQ1}),-1.0]])]});}
            var Q235;
            {var subQ0=sQuery(id+"F0.wireOp",EDGE,"E27");var subQ1=sQuery(id+"F0.wireOp",EDGE,"E0.right");var subQ2=makeQuery(id+"F0.imprint","INTERSECT",VERTEX,{"derivedFrom":[subQ1,subQ0]});Q235=makeQuery(id+"F0.imprint","IMPRINT",FACE,{"disambiguationData":[TD([[makeQuery(id+"F0.imprint","IMPRINT",EDGE,{"disambiguationData":[TD([[subQ2,-1.0]])],"derivedFrom":subQ1}),-1.0]])]});}
            var Q236;
            {var subQ0=sQuery(id+"F0.wireOp",EDGE,"E6");var subQ1=sQuery(id+"F0.wireOp",EDGE,"E0.top");var subQ2=makeQuery(id+"F0.imprint","INTERSECT",VERTEX,{"derivedFrom":[subQ1,subQ0]});Q236=makeQuery(id+"F0.imprint","IMPRINT",FACE,{"disambiguationData":[TD([[makeQuery(id+"F0.imprint","IMPRINT",EDGE,{"disambiguationData":[TD([[subQ2,-1.0]])],"derivedFrom":subQ1}),1.0]])]});}
            var Q237;
            {var subQ0=sQuery(id+"F0.wireOp",EDGE,"E20");var subQ1=sQuery(id+"F0.wireOp",EDGE,"E0.left");var subQ2=makeQuery(id+"F0.imprint","INTERSECT",VERTEX,{"derivedFrom":[subQ1,subQ0]});Q237=makeQuery(id+"F0.imprint","IMPRINT",FACE,{"disambiguationData":[TD([[makeQuery(id+"F0.imprint","IMPRINT",EDGE,{"disambiguationData":[TD([[subQ2,-1.0]])],"derivedFrom":subQ1}),1.0]])]});}
            var Q238;
            {var subQ0=sQuery(id+"F0.wireOp",EDGE,"E27");var subQ1=sQuery(id+"F0.wireOp",EDGE,"E0.left");var subQ2=makeQuery(id+"F0.imprint","INTERSECT",VERTEX,{"derivedFrom":[subQ1,subQ0]});Q238=makeQuery(id+"F0.imprint","IMPRINT",FACE,{"disambiguationData":[TD([[makeQuery(id+"F0.imprint","IMPRINT",EDGE,{"disambiguationData":[TD([[subQ2,-1.0]])],"derivedFrom":subQ1}),1.0]])]});}
            var Q239;
            {var subQ0=sQuery(id+"F0.wireOp",EDGE,"E34");var subQ1=sQuery(id+"F0.wireOp",EDGE,"E5");var subQ2=makeQuery(id+"F0.imprint","INTERSECT",VERTEX,{"derivedFrom":[subQ1,subQ0]});Q239=makeQuery(id+"F0.imprint","IMPRINT",FACE,{"disambiguationData":[TD([[makeQuery(id+"F0.imprint","IMPRINT",EDGE,{"disambiguationData":[TD([[subQ2,-1.0]])],"derivedFrom":subQ1}),1.0]])]});}
            var Q240;
            {var subQ0=sQuery(id+"F0.wireOp",EDGE,"E9");var subQ1=sQuery(id+"F0.wireOp",EDGE,"E0.bottom");var subQ2=makeQuery(id+"F0.imprint","INTERSECT",VERTEX,{"derivedFrom":[subQ1,subQ0]});Q240=makeQuery(id+"F0.imprint","IMPRINT",FACE,{"disambiguationData":[TD([[makeQuery(id+"F0.imprint","IMPRINT",EDGE,{"disambiguationData":[TD([[subQ2,-1.0]])],"derivedFrom":subQ1}),-1.0]])]});}
            var Q241;
            {var subQ0=sQuery(id+"F0.wireOp",EDGE,"E28");var subQ1=sQuery(id+"F0.wireOp",EDGE,"E14");var subQ2=makeQuery(id+"F0.imprint","INTERSECT",VERTEX,{"derivedFrom":[subQ1,subQ0]});Q241=makeQuery(id+"F0.imprint","IMPRINT",FACE,{"disambiguationData":[TD([[makeQuery(id+"F0.imprint","IMPRINT",EDGE,{"disambiguationData":[TD([[subQ2,-1.0]])],"derivedFrom":subQ1}),1.0]])]});}
            var Q242;
            {var subQ0=sQuery(id+"F0.wireOp",EDGE,"E34");var subQ1=sQuery(id+"F0.wireOp",EDGE,"E0.right");var subQ2=makeQuery(id+"F0.imprint","INTERSECT",VERTEX,{"derivedFrom":[subQ1,subQ0]});Q242=makeQuery(id+"F0.imprint","IMPRINT",FACE,{"disambiguationData":[TD([[makeQuery(id+"F0.imprint","IMPRINT",EDGE,{"disambiguationData":[TD([[subQ2,-1.0]])],"derivedFrom":subQ1}),-1.0]])]});}
            var Q243;
            {var subQ0=sQuery(id+"F0.wireOp",EDGE,"E28");var subQ1=sQuery(id+"F0.wireOp",EDGE,"E16");var subQ2=makeQuery(id+"F0.imprint","INTERSECT",VERTEX,{"derivedFrom":[subQ1,subQ0]});Q243=makeQuery(id+"F0.imprint","IMPRINT",FACE,{"disambiguationData":[TD([[makeQuery(id+"F0.imprint","IMPRINT",EDGE,{"disambiguationData":[TD([[subQ2,-1.0]])],"derivedFrom":subQ1}),1.0]])]});}
            var Q244;
            {var subQ0=sQuery(id+"F0.wireOp",EDGE,"E24");var subQ1=sQuery(id+"F0.wireOp",EDGE,"E0.right");var subQ2=makeQuery(id+"F0.imprint","INTERSECT",VERTEX,{"derivedFrom":[subQ1,subQ0]});Q244=makeQuery(id+"F0.imprint","IMPRINT",FACE,{"disambiguationData":[TD([[makeQuery(id+"F0.imprint","IMPRINT",EDGE,{"disambiguationData":[TD([[subQ2,-1.0]])],"derivedFrom":subQ1}),-1.0]])]});}
            var Q245;
            {var subQ0=sQuery(id+"F0.wireOp",EDGE,"E20");var subQ1=sQuery(id+"F0.wireOp",EDGE,"E13");var subQ2=makeQuery(id+"F0.imprint","INTERSECT",VERTEX,{"derivedFrom":[subQ1,subQ0]});Q245=makeQuery(id+"F0.imprint","IMPRINT",FACE,{"disambiguationData":[TD([[makeQuery(id+"F0.imprint","IMPRINT",EDGE,{"disambiguationData":[TD([[subQ2,-1.0]])],"derivedFrom":subQ1}),1.0]])]});}
            var Q246;
            {var subQ0=sQuery(id+"F0.wireOp",EDGE,"E20");var subQ1=sQuery(id+"F0.wireOp",EDGE,"E12");var subQ2=makeQuery(id+"F0.imprint","INTERSECT",VERTEX,{"derivedFrom":[subQ1,subQ0]});Q246=makeQuery(id+"F0.imprint","IMPRINT",FACE,{"disambiguationData":[TD([[makeQuery(id+"F0.imprint","IMPRINT",EDGE,{"disambiguationData":[TD([[subQ2,-1.0]])],"derivedFrom":subQ1}),1.0]])]});}
            var Q247;
            {var subQ0=sQuery(id+"F0.wireOp",EDGE,"E12");var subQ1=sQuery(id+"F0.wireOp",EDGE,"E0.bottom");var subQ2=makeQuery(id+"F0.imprint","INTERSECT",VERTEX,{"derivedFrom":[subQ1,subQ0]});Q247=makeQuery(id+"F0.imprint","IMPRINT",FACE,{"disambiguationData":[TD([[makeQuery(id+"F0.imprint","IMPRINT",EDGE,{"disambiguationData":[TD([[subQ2,-1.0]])],"derivedFrom":subQ1}),-1.0]])]});}
            var Q248;
            {var subQ0=sQuery(id+"F0.wireOp",EDGE,"E6");var subQ1=sQuery(id+"F0.wireOp",EDGE,"E0.bottom");var subQ2=makeQuery(id+"F0.imprint","INTERSECT",VERTEX,{"derivedFrom":[subQ1,subQ0]});Q248=makeQuery(id+"F0.imprint","IMPRINT",FACE,{"disambiguationData":[TD([[makeQuery(id+"F0.imprint","IMPRINT",EDGE,{"disambiguationData":[TD([[subQ2,-1.0]])],"derivedFrom":subQ1}),-1.0]])]});}
            var Q249;
            {var subQ0=sQuery(id+"F0.wireOp",EDGE,"E10");var subQ1=sQuery(id+"F0.wireOp",EDGE,"E0.bottom");var subQ2=makeQuery(id+"F0.imprint","INTERSECT",VERTEX,{"derivedFrom":[subQ1,subQ0]});Q249=makeQuery(id+"F0.imprint","IMPRINT",FACE,{"disambiguationData":[TD([[makeQuery(id+"F0.imprint","IMPRINT",EDGE,{"disambiguationData":[TD([[subQ2,-1.0]])],"derivedFrom":subQ1}),-1.0]])]});}
            var Q250;
            {var subQ0=sQuery(id+"F0.wireOp",EDGE,"E34");var subQ1=sQuery(id+"F0.wireOp",EDGE,"E3");var subQ2=makeQuery(id+"F0.imprint","INTERSECT",VERTEX,{"derivedFrom":[subQ1,subQ0]});Q250=makeQuery(id+"F0.imprint","IMPRINT",FACE,{"disambiguationData":[TD([[makeQuery(id+"F0.imprint","IMPRINT",EDGE,{"disambiguationData":[TD([[subQ2,-1.0]])],"derivedFrom":subQ1}),1.0]])]});}
            var Q251;
            {var subQ0=sQuery(id+"F0.wireOp",EDGE,"E15");var subQ1=sQuery(id+"F0.wireOp",EDGE,"E0.top");var subQ2=makeQuery(id+"F0.imprint","INTERSECT",VERTEX,{"derivedFrom":[subQ1,subQ0]});Q251=makeQuery(id+"F0.imprint","IMPRINT",FACE,{"disambiguationData":[TD([[makeQuery(id+"F0.imprint","IMPRINT",EDGE,{"disambiguationData":[TD([[subQ2,-1.0]])],"derivedFrom":subQ1}),1.0]])]});}
            var Q252;
            {var subQ0=sQuery(id+"F0.wireOp",EDGE,"E28");var subQ1=sQuery(id+"F0.wireOp",EDGE,"E4");var subQ2=makeQuery(id+"F0.imprint","INTERSECT",VERTEX,{"derivedFrom":[subQ1,subQ0]});Q252=makeQuery(id+"F0.imprint","IMPRINT",FACE,{"disambiguationData":[TD([[makeQuery(id+"F0.imprint","IMPRINT",EDGE,{"disambiguationData":[TD([[subQ2,-1.0]])],"derivedFrom":subQ1}),1.0]])]});}
            var Q253;
            {var subQ0=sQuery(id+"F0.wireOp",EDGE,"E25");var subQ1=sQuery(id+"F0.wireOp",EDGE,"E0.right");var subQ2=makeQuery(id+"F0.imprint","INTERSECT",VERTEX,{"derivedFrom":[subQ1,subQ0]});Q253=makeQuery(id+"F0.imprint","IMPRINT",FACE,{"disambiguationData":[TD([[makeQuery(id+"F0.imprint","IMPRINT",EDGE,{"disambiguationData":[TD([[subQ2,-1.0]])],"derivedFrom":subQ1}),-1.0]])]});}
            var Q254;
            {var subQ0=sQuery(id+"F0.wireOp",EDGE,"E34");var subQ1=sQuery(id+"F0.wireOp",EDGE,"E4");var subQ2=makeQuery(id+"F0.imprint","INTERSECT",VERTEX,{"derivedFrom":[subQ1,subQ0]});Q254=makeQuery(id+"F0.imprint","IMPRINT",FACE,{"disambiguationData":[TD([[makeQuery(id+"F0.imprint","IMPRINT",EDGE,{"disambiguationData":[TD([[subQ2,-1.0]])],"derivedFrom":subQ1}),1.0]])]});}
            var Q255;
            {var subQ0=sQuery(id+"F0.wireOp",EDGE,"E0.right");var subQ1=sQuery(id+"F0.wireOp",EDGE,"E0.top");var subQ2=makeQuery(id+"F0.imprint","INTERSECT",VERTEX,{"derivedFrom":[subQ1,subQ0]});Q255=makeQuery(id+"F0.imprint","IMPRINT",FACE,{"disambiguationData":[TD([[makeQuery(id+"F0.imprint","IMPRINT",EDGE,{"disambiguationData":[TD([[subQ2,1.0]])],"derivedFrom":subQ1}),1.0]])]});}
            var Q256;
            {var subQ0=sQuery(id+"F0.wireOp",EDGE,"E0.right");var subQ1=sQuery(id+"F0.wireOp",EDGE,"E0.bottom");var subQ2=makeQuery(id+"F0.imprint","INTERSECT",VERTEX,{"derivedFrom":[subQ1,subQ0]});Q256=makeQuery(id+"F0.imprint","IMPRINT",FACE,{"disambiguationData":[TD([[makeQuery(id+"F0.imprint","IMPRINT",EDGE,{"disambiguationData":[TD([[subQ2,1.0]])],"derivedFrom":subQ1}),-1.0]])]});}
            var Q257;
            {var subQ0=sQuery(id+"F0.wireOp",EDGE,"E0.left");var subQ1=sQuery(id+"F0.wireOp",EDGE,"E0.top");var subQ2=makeQuery(id+"F0.imprint","INTERSECT",VERTEX,{"derivedFrom":[subQ1,subQ0]});Q257=makeQuery(id+"F0.imprint","IMPRINT",FACE,{"disambiguationData":[TD([[makeQuery(id+"F0.imprint","IMPRINT",EDGE,{"disambiguationData":[TD([[subQ2,-1.0]])],"derivedFrom":subQ1}),1.0]])]});}
            var Q258;
            {var subQ0=sQuery(id+"F0.wireOp",EDGE,"E0.left");var subQ1=sQuery(id+"F0.wireOp",EDGE,"E0.bottom");var subQ2=makeQuery(id+"F0.imprint","INTERSECT",VERTEX,{"derivedFrom":[subQ1,subQ0]});Q258=makeQuery(id+"F0.imprint","IMPRINT",FACE,{"disambiguationData":[TD([[makeQuery(id+"F0.imprint","IMPRINT",EDGE,{"disambiguationData":[TD([[subQ2,-1.0]])],"derivedFrom":subQ1}),-1.0]])]});}
            var Q259;
            {var subQ0=sQuery(id+"F0.wireOp",EDGE,"E21");var subQ1=sQuery(id+"F0.wireOp",EDGE,"E1");var subQ2=makeQuery(id+"F0.imprint","INTERSECT",VERTEX,{"derivedFrom":[subQ1,subQ0]});Q259=makeQuery(id+"F0.imprint","IMPRINT",FACE,{"disambiguationData":[TD([[makeQuery(id+"F0.imprint","IMPRINT",EDGE,{"disambiguationData":[TD([[subQ2,-1.0]])],"derivedFrom":subQ1}),1.0]])]});}
            var Q260;
            {var subQ0=sQuery(id+"F0.wireOp",EDGE,"E23");var subQ1=sQuery(id+"F0.wireOp",EDGE,"E1");var subQ2=makeQuery(id+"F0.imprint","INTERSECT",VERTEX,{"derivedFrom":[subQ1,subQ0]});Q260=makeQuery(id+"F0.imprint","IMPRINT",FACE,{"disambiguationData":[TD([[makeQuery(id+"F0.imprint","IMPRINT",EDGE,{"disambiguationData":[TD([[subQ2,-1.0]])],"derivedFrom":subQ1}),1.0]])]});}
            var Q261;
            {var subQ0=sQuery(id+"F0.wireOp",EDGE,"E31");var subQ1=sQuery(id+"F0.wireOp",EDGE,"E1");var subQ2=makeQuery(id+"F0.imprint","INTERSECT",VERTEX,{"derivedFrom":[subQ1,subQ0]});Q261=makeQuery(id+"F0.imprint","IMPRINT",FACE,{"disambiguationData":[TD([[makeQuery(id+"F0.imprint","IMPRINT",EDGE,{"disambiguationData":[TD([[subQ2,-1.0]])],"derivedFrom":subQ1}),1.0]])]});}
            var Q262;
            {var subQ0=sQuery(id+"F0.wireOp",EDGE,"E19");var subQ1=sQuery(id+"F0.wireOp",EDGE,"E1");var subQ2=makeQuery(id+"F0.imprint","INTERSECT",VERTEX,{"derivedFrom":[subQ1,subQ0]});Q262=makeQuery(id+"F0.imprint","IMPRINT",FACE,{"disambiguationData":[TD([[makeQuery(id+"F0.imprint","IMPRINT",EDGE,{"disambiguationData":[TD([[subQ2,-1.0]])],"derivedFrom":subQ1}),1.0]])]});}
            var Q263;
            {var subQ0=sQuery(id+"F0.wireOp",EDGE,"E35");var subQ1=sQuery(id+"F0.wireOp",EDGE,"E1");var subQ2=makeQuery(id+"F0.imprint","INTERSECT",VERTEX,{"derivedFrom":[subQ1,subQ0]});Q263=makeQuery(id+"F0.imprint","IMPRINT",FACE,{"disambiguationData":[TD([[makeQuery(id+"F0.imprint","IMPRINT",EDGE,{"disambiguationData":[TD([[subQ2,-1.0]])],"derivedFrom":subQ1}),1.0]])]});}
            var Q264;
            {var subQ0=sQuery(id+"F0.wireOp",EDGE,"E29");var subQ1=sQuery(id+"F0.wireOp",EDGE,"E1");var subQ2=makeQuery(id+"F0.imprint","INTERSECT",VERTEX,{"derivedFrom":[subQ1,subQ0]});Q264=makeQuery(id+"F0.imprint","IMPRINT",FACE,{"disambiguationData":[TD([[makeQuery(id+"F0.imprint","IMPRINT",EDGE,{"disambiguationData":[TD([[subQ2,-1.0]])],"derivedFrom":subQ1}),1.0]])]});}
            var Q265;
            {var subQ0=sQuery(id+"F0.wireOp",EDGE,"E33");var subQ1=sQuery(id+"F0.wireOp",EDGE,"E1");var subQ2=makeQuery(id+"F0.imprint","INTERSECT",VERTEX,{"derivedFrom":[subQ1,subQ0]});Q265=makeQuery(id+"F0.imprint","IMPRINT",FACE,{"disambiguationData":[TD([[makeQuery(id+"F0.imprint","IMPRINT",EDGE,{"disambiguationData":[TD([[subQ2,-1.0]])],"derivedFrom":subQ1}),1.0]])]});}
            var Q266;
            {var subQ0=sQuery(id+"F0.wireOp",EDGE,"E27");var subQ1=sQuery(id+"F0.wireOp",EDGE,"E1");var subQ2=makeQuery(id+"F0.imprint","INTERSECT",VERTEX,{"derivedFrom":[subQ1,subQ0]});Q266=makeQuery(id+"F0.imprint","IMPRINT",FACE,{"disambiguationData":[TD([[makeQuery(id+"F0.imprint","IMPRINT",EDGE,{"disambiguationData":[TD([[subQ2,-1.0]])],"derivedFrom":subQ1}),1.0]])]});}
            var Q267;
            {var subQ0=sQuery(id+"F0.wireOp",EDGE,"E25");var subQ1=sQuery(id+"F0.wireOp",EDGE,"E1");var subQ2=makeQuery(id+"F0.imprint","INTERSECT",VERTEX,{"derivedFrom":[subQ1,subQ0]});Q267=makeQuery(id+"F0.imprint","IMPRINT",FACE,{"disambiguationData":[TD([[makeQuery(id+"F0.imprint","IMPRINT",EDGE,{"disambiguationData":[TD([[subQ2,-1.0]])],"derivedFrom":subQ1}),1.0]])]});}
            var Q268;
            {var subQ0=sQuery(id+"F0.wireOp",EDGE,"E19");var subQ1=sQuery(id+"F0.wireOp",EDGE,"E17");var subQ2=makeQuery(id+"F0.imprint","INTERSECT",VERTEX,{"derivedFrom":[subQ1,subQ0]});Q268=makeQuery(id+"F0.imprint","IMPRINT",FACE,{"disambiguationData":[TD([[makeQuery(id+"F0.imprint","IMPRINT",EDGE,{"disambiguationData":[TD([[subQ2,-1.0]])],"derivedFrom":subQ1}),1.0]])]});}
            var Q269;
            {var subQ0=sQuery(id+"F0.wireOp",EDGE,"E21");var subQ1=sQuery(id+"F0.wireOp",EDGE,"E17");var subQ2=makeQuery(id+"F0.imprint","INTERSECT",VERTEX,{"derivedFrom":[subQ1,subQ0]});Q269=makeQuery(id+"F0.imprint","IMPRINT",FACE,{"disambiguationData":[TD([[makeQuery(id+"F0.imprint","IMPRINT",EDGE,{"disambiguationData":[TD([[subQ2,-1.0]])],"derivedFrom":subQ1}),1.0]])]});}
            var Q270;
            {var subQ0=sQuery(id+"F0.wireOp",EDGE,"E23");var subQ1=sQuery(id+"F0.wireOp",EDGE,"E17");var subQ2=makeQuery(id+"F0.imprint","INTERSECT",VERTEX,{"derivedFrom":[subQ1,subQ0]});Q270=makeQuery(id+"F0.imprint","IMPRINT",FACE,{"disambiguationData":[TD([[makeQuery(id+"F0.imprint","IMPRINT",EDGE,{"disambiguationData":[TD([[subQ2,-1.0]])],"derivedFrom":subQ1}),1.0]])]});}
            var Q271;
            {var subQ0=sQuery(id+"F0.wireOp",EDGE,"E25");var subQ1=sQuery(id+"F0.wireOp",EDGE,"E17");var subQ2=makeQuery(id+"F0.imprint","INTERSECT",VERTEX,{"derivedFrom":[subQ1,subQ0]});Q271=makeQuery(id+"F0.imprint","IMPRINT",FACE,{"disambiguationData":[TD([[makeQuery(id+"F0.imprint","IMPRINT",EDGE,{"disambiguationData":[TD([[subQ2,-1.0]])],"derivedFrom":subQ1}),1.0]])]});}
            var Q272;
            {var subQ0=sQuery(id+"F0.wireOp",EDGE,"E27");var subQ1=sQuery(id+"F0.wireOp",EDGE,"E17");var subQ2=makeQuery(id+"F0.imprint","INTERSECT",VERTEX,{"derivedFrom":[subQ1,subQ0]});Q272=makeQuery(id+"F0.imprint","IMPRINT",FACE,{"disambiguationData":[TD([[makeQuery(id+"F0.imprint","IMPRINT",EDGE,{"disambiguationData":[TD([[subQ2,-1.0]])],"derivedFrom":subQ1}),1.0]])]});}
            var Q273;
            {var subQ0=sQuery(id+"F0.wireOp",EDGE,"E29");var subQ1=sQuery(id+"F0.wireOp",EDGE,"E17");var subQ2=makeQuery(id+"F0.imprint","INTERSECT",VERTEX,{"derivedFrom":[subQ1,subQ0]});Q273=makeQuery(id+"F0.imprint","IMPRINT",FACE,{"disambiguationData":[TD([[makeQuery(id+"F0.imprint","IMPRINT",EDGE,{"disambiguationData":[TD([[subQ2,-1.0]])],"derivedFrom":subQ1}),1.0]])]});}
            var Q274;
            {var subQ0=sQuery(id+"F0.wireOp",EDGE,"E31");var subQ1=sQuery(id+"F0.wireOp",EDGE,"E17");var subQ2=makeQuery(id+"F0.imprint","INTERSECT",VERTEX,{"derivedFrom":[subQ1,subQ0]});Q274=makeQuery(id+"F0.imprint","IMPRINT",FACE,{"disambiguationData":[TD([[makeQuery(id+"F0.imprint","IMPRINT",EDGE,{"disambiguationData":[TD([[subQ2,-1.0]])],"derivedFrom":subQ1}),1.0]])]});}
            var Q275;
            {var subQ0=sQuery(id+"F0.wireOp",EDGE,"E33");var subQ1=sQuery(id+"F0.wireOp",EDGE,"E17");var subQ2=makeQuery(id+"F0.imprint","INTERSECT",VERTEX,{"derivedFrom":[subQ1,subQ0]});Q275=makeQuery(id+"F0.imprint","IMPRINT",FACE,{"disambiguationData":[TD([[makeQuery(id+"F0.imprint","IMPRINT",EDGE,{"disambiguationData":[TD([[subQ2,-1.0]])],"derivedFrom":subQ1}),1.0]])]});}
            var Q276;
            {var subQ0=sQuery(id+"F0.wireOp",EDGE,"E35");var subQ1=sQuery(id+"F0.wireOp",EDGE,"E17");var subQ2=makeQuery(id+"F0.imprint","INTERSECT",VERTEX,{"derivedFrom":[subQ1,subQ0]});Q276=makeQuery(id+"F0.imprint","IMPRINT",FACE,{"disambiguationData":[TD([[makeQuery(id+"F0.imprint","IMPRINT",EDGE,{"disambiguationData":[TD([[subQ2,-1.0]])],"derivedFrom":subQ1}),1.0]])]});}
            var Q277;
            {var subQ0=sQuery(id+"F0.wireOp",EDGE,"E21");var subQ1=sQuery(id+"F0.wireOp",EDGE,"E5");var subQ2=makeQuery(id+"F0.imprint","INTERSECT",VERTEX,{"derivedFrom":[subQ1,subQ0]});Q277=makeQuery(id+"F0.imprint","IMPRINT",FACE,{"disambiguationData":[TD([[makeQuery(id+"F0.imprint","IMPRINT",EDGE,{"disambiguationData":[TD([[subQ2,-1.0]])],"derivedFrom":subQ1}),1.0]])]});}
            var Q278;
            {var subQ0=sQuery(id+"F0.wireOp",EDGE,"E21");var subQ1=sQuery(id+"F0.wireOp",EDGE,"E7");var subQ2=makeQuery(id+"F0.imprint","INTERSECT",VERTEX,{"derivedFrom":[subQ1,subQ0]});Q278=makeQuery(id+"F0.imprint","IMPRINT",FACE,{"disambiguationData":[TD([[makeQuery(id+"F0.imprint","IMPRINT",EDGE,{"disambiguationData":[TD([[subQ2,-1.0]])],"derivedFrom":subQ1}),1.0]])]});}
            var Q279;
            {var subQ0=sQuery(id+"F0.wireOp",EDGE,"E21");var subQ1=sQuery(id+"F0.wireOp",EDGE,"E9");var subQ2=makeQuery(id+"F0.imprint","INTERSECT",VERTEX,{"derivedFrom":[subQ1,subQ0]});Q279=makeQuery(id+"F0.imprint","IMPRINT",FACE,{"disambiguationData":[TD([[makeQuery(id+"F0.imprint","IMPRINT",EDGE,{"disambiguationData":[TD([[subQ2,-1.0]])],"derivedFrom":subQ1}),1.0]])]});}
            var Q280;
            {var subQ0=sQuery(id+"F0.wireOp",EDGE,"E21");var subQ1=sQuery(id+"F0.wireOp",EDGE,"E11");var subQ2=makeQuery(id+"F0.imprint","INTERSECT",VERTEX,{"derivedFrom":[subQ1,subQ0]});Q280=makeQuery(id+"F0.imprint","IMPRINT",FACE,{"disambiguationData":[TD([[makeQuery(id+"F0.imprint","IMPRINT",EDGE,{"disambiguationData":[TD([[subQ2,-1.0]])],"derivedFrom":subQ1}),1.0]])]});}
            var Q281;
            {var subQ0=sQuery(id+"F0.wireOp",EDGE,"E21");var subQ1=sQuery(id+"F0.wireOp",EDGE,"E13");var subQ2=makeQuery(id+"F0.imprint","INTERSECT",VERTEX,{"derivedFrom":[subQ1,subQ0]});Q281=makeQuery(id+"F0.imprint","IMPRINT",FACE,{"disambiguationData":[TD([[makeQuery(id+"F0.imprint","IMPRINT",EDGE,{"disambiguationData":[TD([[subQ2,-1.0]])],"derivedFrom":subQ1}),1.0]])]});}
            var Q282;
            {var subQ0=sQuery(id+"F0.wireOp",EDGE,"E21");var subQ1=sQuery(id+"F0.wireOp",EDGE,"E15");var subQ2=makeQuery(id+"F0.imprint","INTERSECT",VERTEX,{"derivedFrom":[subQ1,subQ0]});Q282=makeQuery(id+"F0.imprint","IMPRINT",FACE,{"disambiguationData":[TD([[makeQuery(id+"F0.imprint","IMPRINT",EDGE,{"disambiguationData":[TD([[subQ2,-1.0]])],"derivedFrom":subQ1}),1.0]])]});}
            var Q283;
            {var subQ0=sQuery(id+"F0.wireOp",EDGE,"E19");var subQ1=sQuery(id+"F0.wireOp",EDGE,"E15");var subQ2=makeQuery(id+"F0.imprint","INTERSECT",VERTEX,{"derivedFrom":[subQ1,subQ0]});Q283=makeQuery(id+"F0.imprint","IMPRINT",FACE,{"disambiguationData":[TD([[makeQuery(id+"F0.imprint","IMPRINT",EDGE,{"disambiguationData":[TD([[subQ2,-1.0]])],"derivedFrom":subQ1}),1.0]])]});}
            var Q284;
            {var subQ0=sQuery(id+"F0.wireOp",EDGE,"E23");var subQ1=sQuery(id+"F0.wireOp",EDGE,"E15");var subQ2=makeQuery(id+"F0.imprint","INTERSECT",VERTEX,{"derivedFrom":[subQ1,subQ0]});Q284=makeQuery(id+"F0.imprint","IMPRINT",FACE,{"disambiguationData":[TD([[makeQuery(id+"F0.imprint","IMPRINT",EDGE,{"disambiguationData":[TD([[subQ2,-1.0]])],"derivedFrom":subQ1}),1.0]])]});}
            var Q285;
            {var subQ0=sQuery(id+"F0.wireOp",EDGE,"E25");var subQ1=sQuery(id+"F0.wireOp",EDGE,"E15");var subQ2=makeQuery(id+"F0.imprint","INTERSECT",VERTEX,{"derivedFrom":[subQ1,subQ0]});Q285=makeQuery(id+"F0.imprint","IMPRINT",FACE,{"disambiguationData":[TD([[makeQuery(id+"F0.imprint","IMPRINT",EDGE,{"disambiguationData":[TD([[subQ2,-1.0]])],"derivedFrom":subQ1}),1.0]])]});}
            var Q286;
            {var subQ0=sQuery(id+"F0.wireOp",EDGE,"E27");var subQ1=sQuery(id+"F0.wireOp",EDGE,"E15");var subQ2=makeQuery(id+"F0.imprint","INTERSECT",VERTEX,{"derivedFrom":[subQ1,subQ0]});Q286=makeQuery(id+"F0.imprint","IMPRINT",FACE,{"disambiguationData":[TD([[makeQuery(id+"F0.imprint","IMPRINT",EDGE,{"disambiguationData":[TD([[subQ2,-1.0]])],"derivedFrom":subQ1}),1.0]])]});}
            var Q287;
            {var subQ0=sQuery(id+"F0.wireOp",EDGE,"E29");var subQ1=sQuery(id+"F0.wireOp",EDGE,"E15");var subQ2=makeQuery(id+"F0.imprint","INTERSECT",VERTEX,{"derivedFrom":[subQ1,subQ0]});Q287=makeQuery(id+"F0.imprint","IMPRINT",FACE,{"disambiguationData":[TD([[makeQuery(id+"F0.imprint","IMPRINT",EDGE,{"disambiguationData":[TD([[subQ2,-1.0]])],"derivedFrom":subQ1}),1.0]])]});}
            var Q288;
            {var subQ0=sQuery(id+"F0.wireOp",EDGE,"E31");var subQ1=sQuery(id+"F0.wireOp",EDGE,"E15");var subQ2=makeQuery(id+"F0.imprint","INTERSECT",VERTEX,{"derivedFrom":[subQ1,subQ0]});Q288=makeQuery(id+"F0.imprint","IMPRINT",FACE,{"disambiguationData":[TD([[makeQuery(id+"F0.imprint","IMPRINT",EDGE,{"disambiguationData":[TD([[subQ2,-1.0]])],"derivedFrom":subQ1}),1.0]])]});}
            var Q289;
            {var subQ0=sQuery(id+"F0.wireOp",EDGE,"E33");var subQ1=sQuery(id+"F0.wireOp",EDGE,"E15");var subQ2=makeQuery(id+"F0.imprint","INTERSECT",VERTEX,{"derivedFrom":[subQ1,subQ0]});Q289=makeQuery(id+"F0.imprint","IMPRINT",FACE,{"disambiguationData":[TD([[makeQuery(id+"F0.imprint","IMPRINT",EDGE,{"disambiguationData":[TD([[subQ2,-1.0]])],"derivedFrom":subQ1}),1.0]])]});}
            var Q290;
            {var subQ0=sQuery(id+"F0.wireOp",EDGE,"E35");var subQ1=sQuery(id+"F0.wireOp",EDGE,"E15");var subQ2=makeQuery(id+"F0.imprint","INTERSECT",VERTEX,{"derivedFrom":[subQ1,subQ0]});Q290=makeQuery(id+"F0.imprint","IMPRINT",FACE,{"disambiguationData":[TD([[makeQuery(id+"F0.imprint","IMPRINT",EDGE,{"disambiguationData":[TD([[subQ2,-1.0]])],"derivedFrom":subQ1}),1.0]])]});}
            var Q291;
            {var subQ0=sQuery(id+"F0.wireOp",EDGE,"E23");var subQ1=sQuery(id+"F0.wireOp",EDGE,"E5");var subQ2=makeQuery(id+"F0.imprint","INTERSECT",VERTEX,{"derivedFrom":[subQ1,subQ0]});Q291=makeQuery(id+"F0.imprint","IMPRINT",FACE,{"disambiguationData":[TD([[makeQuery(id+"F0.imprint","IMPRINT",EDGE,{"disambiguationData":[TD([[subQ2,-1.0]])],"derivedFrom":subQ1}),1.0]])]});}
            var Q292;
            {var subQ0=sQuery(id+"F0.wireOp",EDGE,"E23");var subQ1=sQuery(id+"F0.wireOp",EDGE,"E7");var subQ2=makeQuery(id+"F0.imprint","INTERSECT",VERTEX,{"derivedFrom":[subQ1,subQ0]});Q292=makeQuery(id+"F0.imprint","IMPRINT",FACE,{"disambiguationData":[TD([[makeQuery(id+"F0.imprint","IMPRINT",EDGE,{"disambiguationData":[TD([[subQ2,-1.0]])],"derivedFrom":subQ1}),1.0]])]});}
            var Q293;
            {var subQ0=sQuery(id+"F0.wireOp",EDGE,"E23");var subQ1=sQuery(id+"F0.wireOp",EDGE,"E11");var subQ2=makeQuery(id+"F0.imprint","INTERSECT",VERTEX,{"derivedFrom":[subQ1,subQ0]});Q293=makeQuery(id+"F0.imprint","IMPRINT",FACE,{"disambiguationData":[TD([[makeQuery(id+"F0.imprint","IMPRINT",EDGE,{"disambiguationData":[TD([[subQ2,-1.0]])],"derivedFrom":subQ1}),1.0]])]});}
            var Q294;
            {var subQ0=sQuery(id+"F0.wireOp",EDGE,"E23");var subQ1=sQuery(id+"F0.wireOp",EDGE,"E13");var subQ2=makeQuery(id+"F0.imprint","INTERSECT",VERTEX,{"derivedFrom":[subQ1,subQ0]});Q294=makeQuery(id+"F0.imprint","IMPRINT",FACE,{"disambiguationData":[TD([[makeQuery(id+"F0.imprint","IMPRINT",EDGE,{"disambiguationData":[TD([[subQ2,-1.0]])],"derivedFrom":subQ1}),1.0]])]});}
            var Q295;
            {var subQ0=sQuery(id+"F0.wireOp",EDGE,"E19");var subQ1=sQuery(id+"F0.wireOp",EDGE,"E13");var subQ2=makeQuery(id+"F0.imprint","INTERSECT",VERTEX,{"derivedFrom":[subQ1,subQ0]});Q295=makeQuery(id+"F0.imprint","IMPRINT",FACE,{"disambiguationData":[TD([[makeQuery(id+"F0.imprint","IMPRINT",EDGE,{"disambiguationData":[TD([[subQ2,-1.0]])],"derivedFrom":subQ1}),1.0]])]});}
            var Q296;
            {var subQ0=sQuery(id+"F0.wireOp",EDGE,"E25");var subQ1=sQuery(id+"F0.wireOp",EDGE,"E13");var subQ2=makeQuery(id+"F0.imprint","INTERSECT",VERTEX,{"derivedFrom":[subQ1,subQ0]});Q296=makeQuery(id+"F0.imprint","IMPRINT",FACE,{"disambiguationData":[TD([[makeQuery(id+"F0.imprint","IMPRINT",EDGE,{"disambiguationData":[TD([[subQ2,-1.0]])],"derivedFrom":subQ1}),1.0]])]});}
            var Q297;
            {var subQ0=sQuery(id+"F0.wireOp",EDGE,"E25");var subQ1=sQuery(id+"F0.wireOp",EDGE,"E11");var subQ2=makeQuery(id+"F0.imprint","INTERSECT",VERTEX,{"derivedFrom":[subQ1,subQ0]});Q297=makeQuery(id+"F0.imprint","IMPRINT",FACE,{"disambiguationData":[TD([[makeQuery(id+"F0.imprint","IMPRINT",EDGE,{"disambiguationData":[TD([[subQ2,-1.0]])],"derivedFrom":subQ1}),1.0]])]});}
            var Q298;
            {var subQ0=sQuery(id+"F0.wireOp",EDGE,"E19");var subQ1=sQuery(id+"F0.wireOp",EDGE,"E7");var subQ2=makeQuery(id+"F0.imprint","INTERSECT",VERTEX,{"derivedFrom":[subQ1,subQ0]});Q298=makeQuery(id+"F0.imprint","IMPRINT",FACE,{"disambiguationData":[TD([[makeQuery(id+"F0.imprint","IMPRINT",EDGE,{"disambiguationData":[TD([[subQ2,-1.0]])],"derivedFrom":subQ1}),1.0]])]});}
            var Q299;
            {var subQ0=sQuery(id+"F0.wireOp",EDGE,"E33");var subQ1=sQuery(id+"F0.wireOp",EDGE,"E7");var subQ2=makeQuery(id+"F0.imprint","INTERSECT",VERTEX,{"derivedFrom":[subQ1,subQ0]});Q299=makeQuery(id+"F0.imprint","IMPRINT",FACE,{"disambiguationData":[TD([[makeQuery(id+"F0.imprint","IMPRINT",EDGE,{"disambiguationData":[TD([[subQ2,-1.0]])],"derivedFrom":subQ1}),1.0]])]});}
            var Q300;
            {var subQ0=sQuery(id+"F0.wireOp",EDGE,"E35");var subQ1=sQuery(id+"F0.wireOp",EDGE,"E7");var subQ2=makeQuery(id+"F0.imprint","INTERSECT",VERTEX,{"derivedFrom":[subQ1,subQ0]});Q300=makeQuery(id+"F0.imprint","IMPRINT",FACE,{"disambiguationData":[TD([[makeQuery(id+"F0.imprint","IMPRINT",EDGE,{"disambiguationData":[TD([[subQ2,-1.0]])],"derivedFrom":subQ1}),1.0]])]});}
            var Q301;
            {var subQ0=sQuery(id+"F0.wireOp",EDGE,"E27");var subQ1=sQuery(id+"F0.wireOp",EDGE,"E11");var subQ2=makeQuery(id+"F0.imprint","INTERSECT",VERTEX,{"derivedFrom":[subQ1,subQ0]});Q301=makeQuery(id+"F0.imprint","IMPRINT",FACE,{"disambiguationData":[TD([[makeQuery(id+"F0.imprint","IMPRINT",EDGE,{"disambiguationData":[TD([[subQ2,-1.0]])],"derivedFrom":subQ1}),1.0]])]});}
            var Q302;
            {var subQ0=sQuery(id+"F0.wireOp",EDGE,"E27");var subQ1=sQuery(id+"F0.wireOp",EDGE,"E13");var subQ2=makeQuery(id+"F0.imprint","INTERSECT",VERTEX,{"derivedFrom":[subQ1,subQ0]});Q302=makeQuery(id+"F0.imprint","IMPRINT",FACE,{"disambiguationData":[TD([[makeQuery(id+"F0.imprint","IMPRINT",EDGE,{"disambiguationData":[TD([[subQ2,-1.0]])],"derivedFrom":subQ1}),1.0]])]});}
            var Q303;
            {var subQ0=sQuery(id+"F0.wireOp",EDGE,"E19");var subQ1=sQuery(id+"F0.wireOp",EDGE,"E5");var subQ2=makeQuery(id+"F0.imprint","INTERSECT",VERTEX,{"derivedFrom":[subQ1,subQ0]});Q303=makeQuery(id+"F0.imprint","IMPRINT",FACE,{"disambiguationData":[TD([[makeQuery(id+"F0.imprint","IMPRINT",EDGE,{"disambiguationData":[TD([[subQ2,-1.0]])],"derivedFrom":subQ1}),1.0]])]});}
            var Q304;
            {var subQ0=sQuery(id+"F0.wireOp",EDGE,"E33");var subQ1=sQuery(id+"F0.wireOp",EDGE,"E5");var subQ2=makeQuery(id+"F0.imprint","INTERSECT",VERTEX,{"derivedFrom":[subQ1,subQ0]});Q304=makeQuery(id+"F0.imprint","IMPRINT",FACE,{"disambiguationData":[TD([[makeQuery(id+"F0.imprint","IMPRINT",EDGE,{"disambiguationData":[TD([[subQ2,-1.0]])],"derivedFrom":subQ1}),1.0]])]});}
            var Q305;
            {var subQ0=sQuery(id+"F0.wireOp",EDGE,"E19");var subQ1=sQuery(id+"F0.wireOp",EDGE,"E9");var subQ2=makeQuery(id+"F0.imprint","INTERSECT",VERTEX,{"derivedFrom":[subQ1,subQ0]});Q305=makeQuery(id+"F0.imprint","IMPRINT",FACE,{"disambiguationData":[TD([[makeQuery(id+"F0.imprint","IMPRINT",EDGE,{"disambiguationData":[TD([[subQ2,-1.0]])],"derivedFrom":subQ1}),1.0]])]});}
            var Q306;
            {var subQ0=sQuery(id+"F0.wireOp",EDGE,"E31");var subQ1=sQuery(id+"F0.wireOp",EDGE,"E9");var subQ2=makeQuery(id+"F0.imprint","INTERSECT",VERTEX,{"derivedFrom":[subQ1,subQ0]});Q306=makeQuery(id+"F0.imprint","IMPRINT",FACE,{"disambiguationData":[TD([[makeQuery(id+"F0.imprint","IMPRINT",EDGE,{"disambiguationData":[TD([[subQ2,-1.0]])],"derivedFrom":subQ1}),1.0]])]});}
            var Q307;
            {var subQ0=sQuery(id+"F0.wireOp",EDGE,"E35");var subQ1=sQuery(id+"F0.wireOp",EDGE,"E5");var subQ2=makeQuery(id+"F0.imprint","INTERSECT",VERTEX,{"derivedFrom":[subQ1,subQ0]});Q307=makeQuery(id+"F0.imprint","IMPRINT",FACE,{"disambiguationData":[TD([[makeQuery(id+"F0.imprint","IMPRINT",EDGE,{"disambiguationData":[TD([[subQ2,-1.0]])],"derivedFrom":subQ1}),1.0]])]});}
            var Q308;
            {var subQ0=sQuery(id+"F0.wireOp",EDGE,"E31");var subQ1=sQuery(id+"F0.wireOp",EDGE,"E5");var subQ2=makeQuery(id+"F0.imprint","INTERSECT",VERTEX,{"derivedFrom":[subQ1,subQ0]});Q308=makeQuery(id+"F0.imprint","IMPRINT",FACE,{"disambiguationData":[TD([[makeQuery(id+"F0.imprint","IMPRINT",EDGE,{"disambiguationData":[TD([[subQ2,-1.0]])],"derivedFrom":subQ1}),1.0]])]});}
            var Q309;
            {var subQ0=sQuery(id+"F0.wireOp",EDGE,"E31");var subQ1=sQuery(id+"F0.wireOp",EDGE,"E11");var subQ2=makeQuery(id+"F0.imprint","INTERSECT",VERTEX,{"derivedFrom":[subQ1,subQ0]});Q309=makeQuery(id+"F0.imprint","IMPRINT",FACE,{"disambiguationData":[TD([[makeQuery(id+"F0.imprint","IMPRINT",EDGE,{"disambiguationData":[TD([[subQ2,-1.0]])],"derivedFrom":subQ1}),1.0]])]});}
            var Q310;
            {var subQ0=sQuery(id+"F0.wireOp",EDGE,"E35");var subQ1=sQuery(id+"F0.wireOp",EDGE,"E9");var subQ2=makeQuery(id+"F0.imprint","INTERSECT",VERTEX,{"derivedFrom":[subQ1,subQ0]});Q310=makeQuery(id+"F0.imprint","IMPRINT",FACE,{"disambiguationData":[TD([[makeQuery(id+"F0.imprint","IMPRINT",EDGE,{"disambiguationData":[TD([[subQ2,-1.0]])],"derivedFrom":subQ1}),1.0]])]});}
            var Q311;
            {var subQ0=sQuery(id+"F0.wireOp",EDGE,"E31");var subQ1=sQuery(id+"F0.wireOp",EDGE,"E7");var subQ2=makeQuery(id+"F0.imprint","INTERSECT",VERTEX,{"derivedFrom":[subQ1,subQ0]});Q311=makeQuery(id+"F0.imprint","IMPRINT",FACE,{"disambiguationData":[TD([[makeQuery(id+"F0.imprint","IMPRINT",EDGE,{"disambiguationData":[TD([[subQ2,-1.0]])],"derivedFrom":subQ1}),1.0]])]});}
            var Q312;
            {var subQ0=sQuery(id+"F0.wireOp",EDGE,"E31");var subQ1=sQuery(id+"F0.wireOp",EDGE,"E13");var subQ2=makeQuery(id+"F0.imprint","INTERSECT",VERTEX,{"derivedFrom":[subQ1,subQ0]});Q312=makeQuery(id+"F0.imprint","IMPRINT",FACE,{"disambiguationData":[TD([[makeQuery(id+"F0.imprint","IMPRINT",EDGE,{"disambiguationData":[TD([[subQ2,-1.0]])],"derivedFrom":subQ1}),1.0]])]});}
            var Q313;
            {var subQ0=sQuery(id+"F0.wireOp",EDGE,"E25");var subQ1=sQuery(id+"F0.wireOp",EDGE,"E5");var subQ2=makeQuery(id+"F0.imprint","INTERSECT",VERTEX,{"derivedFrom":[subQ1,subQ0]});Q313=makeQuery(id+"F0.imprint","IMPRINT",FACE,{"disambiguationData":[TD([[makeQuery(id+"F0.imprint","IMPRINT",EDGE,{"disambiguationData":[TD([[subQ2,-1.0]])],"derivedFrom":subQ1}),1.0]])]});}
            var Q314;
            {var subQ0=sQuery(id+"F0.wireOp",EDGE,"E29");var subQ1=sQuery(id+"F0.wireOp",EDGE,"E5");var subQ2=makeQuery(id+"F0.imprint","INTERSECT",VERTEX,{"derivedFrom":[subQ1,subQ0]});Q314=makeQuery(id+"F0.imprint","IMPRINT",FACE,{"disambiguationData":[TD([[makeQuery(id+"F0.imprint","IMPRINT",EDGE,{"disambiguationData":[TD([[subQ2,-1.0]])],"derivedFrom":subQ1}),1.0]])]});}
            var Q315;
            {var subQ0=sQuery(id+"F0.wireOp",EDGE,"E29");var subQ1=sQuery(id+"F0.wireOp",EDGE,"E11");var subQ2=makeQuery(id+"F0.imprint","INTERSECT",VERTEX,{"derivedFrom":[subQ1,subQ0]});Q315=makeQuery(id+"F0.imprint","IMPRINT",FACE,{"disambiguationData":[TD([[makeQuery(id+"F0.imprint","IMPRINT",EDGE,{"disambiguationData":[TD([[subQ2,-1.0]])],"derivedFrom":subQ1}),1.0]])]});}
            var Q316;
            {var subQ0=sQuery(id+"F0.wireOp",EDGE,"E29");var subQ1=sQuery(id+"F0.wireOp",EDGE,"E7");var subQ2=makeQuery(id+"F0.imprint","INTERSECT",VERTEX,{"derivedFrom":[subQ1,subQ0]});Q316=makeQuery(id+"F0.imprint","IMPRINT",FACE,{"disambiguationData":[TD([[makeQuery(id+"F0.imprint","IMPRINT",EDGE,{"disambiguationData":[TD([[subQ2,-1.0]])],"derivedFrom":subQ1}),1.0]])]});}
            var Q317;
            {var subQ0=sQuery(id+"F0.wireOp",EDGE,"E29");var subQ1=sQuery(id+"F0.wireOp",EDGE,"E13");var subQ2=makeQuery(id+"F0.imprint","INTERSECT",VERTEX,{"derivedFrom":[subQ1,subQ0]});Q317=makeQuery(id+"F0.imprint","IMPRINT",FACE,{"disambiguationData":[TD([[makeQuery(id+"F0.imprint","IMPRINT",EDGE,{"disambiguationData":[TD([[subQ2,-1.0]])],"derivedFrom":subQ1}),1.0]])]});}
            var Q318;
            {var subQ0=sQuery(id+"F0.wireOp",EDGE,"E33");var subQ1=sQuery(id+"F0.wireOp",EDGE,"E9");var subQ2=makeQuery(id+"F0.imprint","INTERSECT",VERTEX,{"derivedFrom":[subQ1,subQ0]});Q318=makeQuery(id+"F0.imprint","IMPRINT",FACE,{"disambiguationData":[TD([[makeQuery(id+"F0.imprint","IMPRINT",EDGE,{"disambiguationData":[TD([[subQ2,-1.0]])],"derivedFrom":subQ1}),1.0]])]});}
            var Q319;
            {var subQ0=sQuery(id+"F0.wireOp",EDGE,"E29");var subQ1=sQuery(id+"F0.wireOp",EDGE,"E9");var subQ2=makeQuery(id+"F0.imprint","INTERSECT",VERTEX,{"derivedFrom":[subQ1,subQ0]});Q319=makeQuery(id+"F0.imprint","IMPRINT",FACE,{"disambiguationData":[TD([[makeQuery(id+"F0.imprint","IMPRINT",EDGE,{"disambiguationData":[TD([[subQ2,-1.0]])],"derivedFrom":subQ1}),1.0]])]});}
            var Q320;
            {var subQ0=sQuery(id+"F0.wireOp",EDGE,"E27");var subQ1=sQuery(id+"F0.wireOp",EDGE,"E7");var subQ2=makeQuery(id+"F0.imprint","INTERSECT",VERTEX,{"derivedFrom":[subQ1,subQ0]});Q320=makeQuery(id+"F0.imprint","IMPRINT",FACE,{"disambiguationData":[TD([[makeQuery(id+"F0.imprint","IMPRINT",EDGE,{"disambiguationData":[TD([[subQ2,-1.0]])],"derivedFrom":subQ1}),1.0]])]});}
            var Q321;
            {var subQ0=sQuery(id+"F0.wireOp",EDGE,"E27");var subQ1=sQuery(id+"F0.wireOp",EDGE,"E5");var subQ2=makeQuery(id+"F0.imprint","INTERSECT",VERTEX,{"derivedFrom":[subQ1,subQ0]});Q321=makeQuery(id+"F0.imprint","IMPRINT",FACE,{"disambiguationData":[TD([[makeQuery(id+"F0.imprint","IMPRINT",EDGE,{"disambiguationData":[TD([[subQ2,-1.0]])],"derivedFrom":subQ1}),1.0]])]});}
            var Q322;
            {var subQ0=sQuery(id+"F0.wireOp",EDGE,"E35");var subQ1=sQuery(id+"F0.wireOp",EDGE,"E11");var subQ2=makeQuery(id+"F0.imprint","INTERSECT",VERTEX,{"derivedFrom":[subQ1,subQ0]});Q322=makeQuery(id+"F0.imprint","IMPRINT",FACE,{"disambiguationData":[TD([[makeQuery(id+"F0.imprint","IMPRINT",EDGE,{"disambiguationData":[TD([[subQ2,-1.0]])],"derivedFrom":subQ1}),1.0]])]});}
            var Q323;
            {var subQ0=sQuery(id+"F0.wireOp",EDGE,"E33");var subQ1=sQuery(id+"F0.wireOp",EDGE,"E11");var subQ2=makeQuery(id+"F0.imprint","INTERSECT",VERTEX,{"derivedFrom":[subQ1,subQ0]});Q323=makeQuery(id+"F0.imprint","IMPRINT",FACE,{"disambiguationData":[TD([[makeQuery(id+"F0.imprint","IMPRINT",EDGE,{"disambiguationData":[TD([[subQ2,-1.0]])],"derivedFrom":subQ1}),1.0]])]});}
            var Q324;
            {var subQ0=sQuery(id+"F0.wireOp",EDGE,"E19");var subQ1=sQuery(id+"F0.wireOp",EDGE,"E11");var subQ2=makeQuery(id+"F0.imprint","INTERSECT",VERTEX,{"derivedFrom":[subQ1,subQ0]});Q324=makeQuery(id+"F0.imprint","IMPRINT",FACE,{"disambiguationData":[TD([[makeQuery(id+"F0.imprint","IMPRINT",EDGE,{"disambiguationData":[TD([[subQ2,-1.0]])],"derivedFrom":subQ1}),1.0]])]});}
            var Q325;
            {var subQ0=sQuery(id+"F0.wireOp",EDGE,"E25");var subQ1=sQuery(id+"F0.wireOp",EDGE,"E9");var subQ2=makeQuery(id+"F0.imprint","INTERSECT",VERTEX,{"derivedFrom":[subQ1,subQ0]});Q325=makeQuery(id+"F0.imprint","IMPRINT",FACE,{"disambiguationData":[TD([[makeQuery(id+"F0.imprint","IMPRINT",EDGE,{"disambiguationData":[TD([[subQ2,-1.0]])],"derivedFrom":subQ1}),1.0]])]});}
            var Q326;
            {var subQ0=sQuery(id+"F0.wireOp",EDGE,"E25");var subQ1=sQuery(id+"F0.wireOp",EDGE,"E7");var subQ2=makeQuery(id+"F0.imprint","INTERSECT",VERTEX,{"derivedFrom":[subQ1,subQ0]});Q326=makeQuery(id+"F0.imprint","IMPRINT",FACE,{"disambiguationData":[TD([[makeQuery(id+"F0.imprint","IMPRINT",EDGE,{"disambiguationData":[TD([[subQ2,-1.0]])],"derivedFrom":subQ1}),1.0]])]});}
            var Q327;
            {var subQ0=sQuery(id+"F0.wireOp",EDGE,"E35");var subQ1=sQuery(id+"F0.wireOp",EDGE,"E13");var subQ2=makeQuery(id+"F0.imprint","INTERSECT",VERTEX,{"derivedFrom":[subQ1,subQ0]});Q327=makeQuery(id+"F0.imprint","IMPRINT",FACE,{"disambiguationData":[TD([[makeQuery(id+"F0.imprint","IMPRINT",EDGE,{"disambiguationData":[TD([[subQ2,-1.0]])],"derivedFrom":subQ1}),1.0]])]});}
            var Q328;
            {var subQ0=sQuery(id+"F0.wireOp",EDGE,"E33");var subQ1=sQuery(id+"F0.wireOp",EDGE,"E13");var subQ2=makeQuery(id+"F0.imprint","INTERSECT",VERTEX,{"derivedFrom":[subQ1,subQ0]});Q328=makeQuery(id+"F0.imprint","IMPRINT",FACE,{"disambiguationData":[TD([[makeQuery(id+"F0.imprint","IMPRINT",EDGE,{"disambiguationData":[TD([[subQ2,-1.0]])],"derivedFrom":subQ1}),1.0]])]});}
            var Q329;
            {var subQ0=sQuery(id+"F0.wireOp",EDGE,"E27");var subQ1=sQuery(id+"F0.wireOp",EDGE,"E9");var subQ2=makeQuery(id+"F0.imprint","INTERSECT",VERTEX,{"derivedFrom":[subQ1,subQ0]});Q329=makeQuery(id+"F0.imprint","IMPRINT",FACE,{"disambiguationData":[TD([[makeQuery(id+"F0.imprint","IMPRINT",EDGE,{"disambiguationData":[TD([[subQ2,-1.0]])],"derivedFrom":subQ1}),1.0]])]});}
            var Q330;
            {var subQ0=sQuery(id+"F0.wireOp",EDGE,"E31");var subQ1=sQuery(id+"F0.wireOp",EDGE,"E3");var subQ2=makeQuery(id+"F0.imprint","INTERSECT",VERTEX,{"derivedFrom":[subQ1,subQ0]});Q330=makeQuery(id+"F0.imprint","IMPRINT",FACE,{"disambiguationData":[TD([[makeQuery(id+"F0.imprint","IMPRINT",EDGE,{"disambiguationData":[TD([[subQ2,-1.0]])],"derivedFrom":subQ1}),1.0]])]});}
            var Q331;
            {var subQ0=sQuery(id+"F0.wireOp",EDGE,"E27");var subQ1=sQuery(id+"F0.wireOp",EDGE,"E3");var subQ2=makeQuery(id+"F0.imprint","INTERSECT",VERTEX,{"derivedFrom":[subQ1,subQ0]});Q331=makeQuery(id+"F0.imprint","IMPRINT",FACE,{"disambiguationData":[TD([[makeQuery(id+"F0.imprint","IMPRINT",EDGE,{"disambiguationData":[TD([[subQ2,-1.0]])],"derivedFrom":subQ1}),1.0]])]});}
            var Q332;
            {var subQ0=sQuery(id+"F0.wireOp",EDGE,"E35");var subQ1=sQuery(id+"F0.wireOp",EDGE,"E3");var subQ2=makeQuery(id+"F0.imprint","INTERSECT",VERTEX,{"derivedFrom":[subQ1,subQ0]});Q332=makeQuery(id+"F0.imprint","IMPRINT",FACE,{"disambiguationData":[TD([[makeQuery(id+"F0.imprint","IMPRINT",EDGE,{"disambiguationData":[TD([[subQ2,-1.0]])],"derivedFrom":subQ1}),1.0]])]});}
            var Q333;
            {var subQ0=sQuery(id+"F0.wireOp",EDGE,"E33");var subQ1=sQuery(id+"F0.wireOp",EDGE,"E3");var subQ2=makeQuery(id+"F0.imprint","INTERSECT",VERTEX,{"derivedFrom":[subQ1,subQ0]});Q333=makeQuery(id+"F0.imprint","IMPRINT",FACE,{"disambiguationData":[TD([[makeQuery(id+"F0.imprint","IMPRINT",EDGE,{"disambiguationData":[TD([[subQ2,-1.0]])],"derivedFrom":subQ1}),1.0]])]});}
            var Q334;
            {var subQ0=sQuery(id+"F0.wireOp",EDGE,"E29");var subQ1=sQuery(id+"F0.wireOp",EDGE,"E3");var subQ2=makeQuery(id+"F0.imprint","INTERSECT",VERTEX,{"derivedFrom":[subQ1,subQ0]});Q334=makeQuery(id+"F0.imprint","IMPRINT",FACE,{"disambiguationData":[TD([[makeQuery(id+"F0.imprint","IMPRINT",EDGE,{"disambiguationData":[TD([[subQ2,-1.0]])],"derivedFrom":subQ1}),1.0]])]});}
            var Q335;
            {var subQ0=sQuery(id+"F0.wireOp",EDGE,"E21");var subQ1=sQuery(id+"F0.wireOp",EDGE,"E3");var subQ2=makeQuery(id+"F0.imprint","INTERSECT",VERTEX,{"derivedFrom":[subQ1,subQ0]});Q335=makeQuery(id+"F0.imprint","IMPRINT",FACE,{"disambiguationData":[TD([[makeQuery(id+"F0.imprint","IMPRINT",EDGE,{"disambiguationData":[TD([[subQ2,-1.0]])],"derivedFrom":subQ1}),1.0]])]});}
            var Q336;
            {var subQ0=sQuery(id+"F0.wireOp",EDGE,"E19");var subQ1=sQuery(id+"F0.wireOp",EDGE,"E3");var subQ2=makeQuery(id+"F0.imprint","INTERSECT",VERTEX,{"derivedFrom":[subQ1,subQ0]});Q336=makeQuery(id+"F0.imprint","IMPRINT",FACE,{"disambiguationData":[TD([[makeQuery(id+"F0.imprint","IMPRINT",EDGE,{"disambiguationData":[TD([[subQ2,-1.0]])],"derivedFrom":subQ1}),1.0]])]});}
            var Q337;
            {var subQ0=sQuery(id+"F0.wireOp",EDGE,"E26");var subQ1=sQuery(id+"F0.wireOp",EDGE,"E4");var subQ2=makeQuery(id+"F0.imprint","INTERSECT",VERTEX,{"derivedFrom":[subQ1,subQ0]});Q337=makeQuery(id+"F0.imprint","IMPRINT",FACE,{"disambiguationData":[TD([[makeQuery(id+"F0.imprint","IMPRINT",EDGE,{"disambiguationData":[TD([[subQ2,-1.0]])],"derivedFrom":subQ1}),1.0]])]});}
            var Q338;
            {var subQ0=sQuery(id+"F0.wireOp",EDGE,"E26");var subQ1=sQuery(id+"F0.wireOp",EDGE,"E3");var subQ2=makeQuery(id+"F0.imprint","INTERSECT",VERTEX,{"derivedFrom":[subQ1,subQ0]});Q338=makeQuery(id+"F0.imprint","IMPRINT",FACE,{"disambiguationData":[TD([[makeQuery(id+"F0.imprint","IMPRINT",EDGE,{"disambiguationData":[TD([[subQ2,-1.0]])],"derivedFrom":subQ1}),1.0]])]});}
            var Q339;
            {var subQ0=sQuery(id+"F0.wireOp",EDGE,"E26");var subQ1=sQuery(id+"F0.wireOp",EDGE,"E2");var subQ2=makeQuery(id+"F0.imprint","INTERSECT",VERTEX,{"derivedFrom":[subQ1,subQ0]});Q339=makeQuery(id+"F0.imprint","IMPRINT",FACE,{"disambiguationData":[TD([[makeQuery(id+"F0.imprint","IMPRINT",EDGE,{"disambiguationData":[TD([[subQ2,-1.0]])],"derivedFrom":subQ1}),1.0]])]});}
            var Q340;
            {var subQ0=sQuery(id+"F0.wireOp",EDGE,"E25");var subQ1=sQuery(id+"F0.wireOp",EDGE,"E3");var subQ2=makeQuery(id+"F0.imprint","INTERSECT",VERTEX,{"derivedFrom":[subQ1,subQ0]});Q340=makeQuery(id+"F0.imprint","IMPRINT",FACE,{"disambiguationData":[TD([[makeQuery(id+"F0.imprint","IMPRINT",EDGE,{"disambiguationData":[TD([[subQ2,-1.0]])],"derivedFrom":subQ1}),1.0]])]});}
            var Q341;
            {var subQ0=sQuery(id+"F0.wireOp",EDGE,"E25");var subQ1=sQuery(id+"F0.wireOp",EDGE,"E4");var subQ2=makeQuery(id+"F0.imprint","INTERSECT",VERTEX,{"derivedFrom":[subQ1,subQ0]});Q341=makeQuery(id+"F0.imprint","IMPRINT",FACE,{"disambiguationData":[TD([[makeQuery(id+"F0.imprint","IMPRINT",EDGE,{"disambiguationData":[TD([[subQ2,-1.0]])],"derivedFrom":subQ1}),1.0]])]});}
            var Q342;
            {var subQ0=sQuery(id+"F0.wireOp",EDGE,"E25");var subQ1=sQuery(id+"F0.wireOp",EDGE,"E2");var subQ2=makeQuery(id+"F0.imprint","INTERSECT",VERTEX,{"derivedFrom":[subQ1,subQ0]});Q342=makeQuery(id+"F0.imprint","IMPRINT",FACE,{"disambiguationData":[TD([[makeQuery(id+"F0.imprint","IMPRINT",EDGE,{"disambiguationData":[TD([[subQ2,-1.0]])],"derivedFrom":subQ1}),1.0]])]});}
            var Q343;
            {var subQ0=sQuery(id+"F0.wireOp",EDGE,"E22");var subQ1=sQuery(id+"F0.wireOp",EDGE,"E2");var subQ2=makeQuery(id+"F0.imprint","INTERSECT",VERTEX,{"derivedFrom":[subQ1,subQ0]});Q343=makeQuery(id+"F0.imprint","IMPRINT",FACE,{"disambiguationData":[TD([[makeQuery(id+"F0.imprint","IMPRINT",EDGE,{"disambiguationData":[TD([[subQ2,-1.0]])],"derivedFrom":subQ1}),1.0]])]});}
            var Q344;
            {var subQ0=sQuery(id+"F0.wireOp",EDGE,"E22");var subQ1=sQuery(id+"F0.wireOp",EDGE,"E3");var subQ2=makeQuery(id+"F0.imprint","INTERSECT",VERTEX,{"derivedFrom":[subQ1,subQ0]});Q344=makeQuery(id+"F0.imprint","IMPRINT",FACE,{"disambiguationData":[TD([[makeQuery(id+"F0.imprint","IMPRINT",EDGE,{"disambiguationData":[TD([[subQ2,-1.0]])],"derivedFrom":subQ1}),1.0]])]});}
            var Q345;
            {var subQ0=sQuery(id+"F0.wireOp",EDGE,"E22");var subQ1=sQuery(id+"F0.wireOp",EDGE,"E4");var subQ2=makeQuery(id+"F0.imprint","INTERSECT",VERTEX,{"derivedFrom":[subQ1,subQ0]});Q345=makeQuery(id+"F0.imprint","IMPRINT",FACE,{"disambiguationData":[TD([[makeQuery(id+"F0.imprint","IMPRINT",EDGE,{"disambiguationData":[TD([[subQ2,-1.0]])],"derivedFrom":subQ1}),1.0]])]});}
            var Q346;
            {var subQ0=sQuery(id+"F0.wireOp",EDGE,"E23");var subQ1=sQuery(id+"F0.wireOp",EDGE,"E2");var subQ2=makeQuery(id+"F0.imprint","INTERSECT",VERTEX,{"derivedFrom":[subQ1,subQ0]});Q346=makeQuery(id+"F0.imprint","IMPRINT",FACE,{"disambiguationData":[TD([[makeQuery(id+"F0.imprint","IMPRINT",EDGE,{"disambiguationData":[TD([[subQ2,-1.0]])],"derivedFrom":subQ1}),1.0]])]});}
            var Q347;
            {var subQ0=sQuery(id+"F0.wireOp",EDGE,"E23");var subQ1=sQuery(id+"F0.wireOp",EDGE,"E3");var subQ2=makeQuery(id+"F0.imprint","INTERSECT",VERTEX,{"derivedFrom":[subQ1,subQ0]});Q347=makeQuery(id+"F0.imprint","IMPRINT",FACE,{"disambiguationData":[TD([[makeQuery(id+"F0.imprint","IMPRINT",EDGE,{"disambiguationData":[TD([[subQ2,-1.0]])],"derivedFrom":subQ1}),1.0]])]});}
            var Q348;
            {var subQ0=sQuery(id+"F0.wireOp",EDGE,"E23");var subQ1=sQuery(id+"F0.wireOp",EDGE,"E4");var subQ2=makeQuery(id+"F0.imprint","INTERSECT",VERTEX,{"derivedFrom":[subQ1,subQ0]});Q348=makeQuery(id+"F0.imprint","IMPRINT",FACE,{"disambiguationData":[TD([[makeQuery(id+"F0.imprint","IMPRINT",EDGE,{"disambiguationData":[TD([[subQ2,-1.0]])],"derivedFrom":subQ1}),1.0]])]});}
            var Q349;
            {var subQ0=sQuery(id+"F0.wireOp",EDGE,"E24");var subQ1=sQuery(id+"F0.wireOp",EDGE,"E2");var subQ2=makeQuery(id+"F0.imprint","INTERSECT",VERTEX,{"derivedFrom":[subQ1,subQ0]});Q349=makeQuery(id+"F0.imprint","IMPRINT",FACE,{"disambiguationData":[TD([[makeQuery(id+"F0.imprint","IMPRINT",EDGE,{"disambiguationData":[TD([[subQ2,-1.0]])],"derivedFrom":subQ1}),1.0]])]});}
            var Q350;
            {var subQ0=sQuery(id+"F0.wireOp",EDGE,"E24");var subQ1=sQuery(id+"F0.wireOp",EDGE,"E3");var subQ2=makeQuery(id+"F0.imprint","INTERSECT",VERTEX,{"derivedFrom":[subQ1,subQ0]});Q350=makeQuery(id+"F0.imprint","IMPRINT",FACE,{"disambiguationData":[TD([[makeQuery(id+"F0.imprint","IMPRINT",EDGE,{"disambiguationData":[TD([[subQ2,-1.0]])],"derivedFrom":subQ1}),1.0]])]});}
            var Q351;
            {var subQ0=sQuery(id+"F0.wireOp",EDGE,"E24");var subQ1=sQuery(id+"F0.wireOp",EDGE,"E4");var subQ2=makeQuery(id+"F0.imprint","INTERSECT",VERTEX,{"derivedFrom":[subQ1,subQ0]});Q351=makeQuery(id+"F0.imprint","IMPRINT",FACE,{"disambiguationData":[TD([[makeQuery(id+"F0.imprint","IMPRINT",EDGE,{"disambiguationData":[TD([[subQ2,-1.0]])],"derivedFrom":subQ1}),1.0]])]});}
            extrude(context, id + "F1", {"entities" : qUnion([Q0, Q1, Q2, Q3, Q4, Q5, Q6, Q7, Q8, Q9, Q10, Q11, Q12, Q13, Q14, Q15, Q16, Q17, Q18, Q19, Q20, Q21, Q22, Q23, Q24, Q25, Q26, Q27, Q28, Q29, Q30, Q31, Q32, Q33, Q34, Q35, Q36, Q37, Q38, Q39, Q40, Q41, Q42, Q43, Q44, Q45, Q46, Q47, Q48, Q49, Q50, Q51, Q52, Q53, Q54, Q55, Q56, Q57, Q58, Q59, Q60, Q61, Q62, Q63, Q64, Q65, Q66, Q67, Q68, Q69, Q70, Q71, Q72, Q73, Q74, Q75, Q76, Q77, Q78, Q79, Q80, Q81, Q82, Q83, Q84, Q85, Q86, Q87, Q88, Q89, Q90, Q91, Q92, Q93, Q94, Q95, Q96, Q97, Q98, Q99, Q100, Q101, Q102, Q103, Q104, Q105, Q106, Q107, Q108, Q109, Q110, Q111, Q112, Q113, Q114, Q115, Q116, Q117, Q118, Q119, Q120, Q121, Q122, Q123, Q124, Q125, Q126, Q127, Q128, Q129, Q130, Q131, Q132, Q133, Q134, Q135, Q136, Q137, Q138, Q139, Q140, Q141, Q142, Q143, Q144, Q145, Q146, Q147, Q148, Q149, Q150, Q151, Q152, Q153, Q154, Q155, Q156, Q157, Q158, Q159, Q160, Q161, Q162, Q163, Q164, Q165, Q166, Q167, Q168, Q169, Q170, Q171, Q172, Q173, Q174, Q175, Q176, Q177, Q178, Q179, Q180, Q181, Q182, Q183, Q184, Q185, Q186, Q187, Q188, Q189, Q190, Q191, Q192, Q193, Q194, Q195, Q196, Q197, Q198, Q199, Q200, Q201, Q202, Q203, Q204, Q205, Q206, Q207, Q208, Q209, Q210, Q211, Q212, Q213, Q214, Q215, Q216, Q217, Q218, Q219, Q220, Q221, Q222, Q223, Q224, Q225, Q226, Q227, Q228, Q229, Q230, Q231, Q232, Q233, Q234, Q235, Q236, Q237, Q238, Q239, Q240, Q241, Q242, Q243, Q244, Q245, Q246, Q247, Q248, Q249, Q250, Q251, Q252, Q253, Q254, Q255, Q256, Q257, Q258, Q259, Q260, Q261, Q262, Q263, Q264, Q265, Q266, Q267, Q268, Q269, Q270, Q271, Q272, Q273, Q274, Q275, Q276, Q277, Q278, Q279, Q280, Q281, Q282, Q283, Q284, Q285, Q286, Q287, Q288, Q289, Q290, Q291, Q292, Q293, Q294, Q295, Q296, Q297, Q298, Q299, Q300, Q301, Q302, Q303, Q304, Q305, Q306, Q307, Q308, Q309, Q310, Q311, Q312, Q313, Q314, Q315, Q316, Q317, Q318, Q319, Q320, Q321, Q322, Q323, Q324, Q325, Q326, Q327, Q328, Q329, Q330, Q331, Q332, Q333, Q334, Q335, Q336, Q337, Q338, Q339, Q340, Q341, Q342, Q343, Q344, Q345, Q346, Q347, Q348, Q349, Q350, Q351]), "depth" : 4 * mm, "offsetDistance" : 25 * mm});
        }
        {
            var Q0;
            Q0=makeQuery(id+"F1.opExtrude","SWEPT_FACE",FACE,{"disambiguationData":[OSD([sQuery(id+"F0.wireOp",EDGE,"E0.left")])]});
            var Q1;
            Q1=makeQuery(id+"F1.opExtrude","SWEPT_FACE",FACE,{"disambiguationData":[OSD([sQuery(id+"F0.wireOp",EDGE,"E0.top")])]});
            var Q2;
            Q2=makeQuery(id+"F1.opExtrude","SWEPT_FACE",FACE,{"disambiguationData":[OSD([sQuery(id+"F0.wireOp",EDGE,"E0.right")])]});
            var Q3;
            Q3=makeQuery(id+"F1.opExtrude","SWEPT_FACE",FACE,{"disambiguationData":[OSD([sQuery(id+"F0.wireOp",EDGE,"E0.bottom")])]});
            fillet(context, id + "F2", {"entities" : qUnion([Q0, Q1, Q2, Q3]), "radius" : 0.1 * mm, "tangentPropagation" : true, "allowEdgeOverflow" : false});
        }
    });
